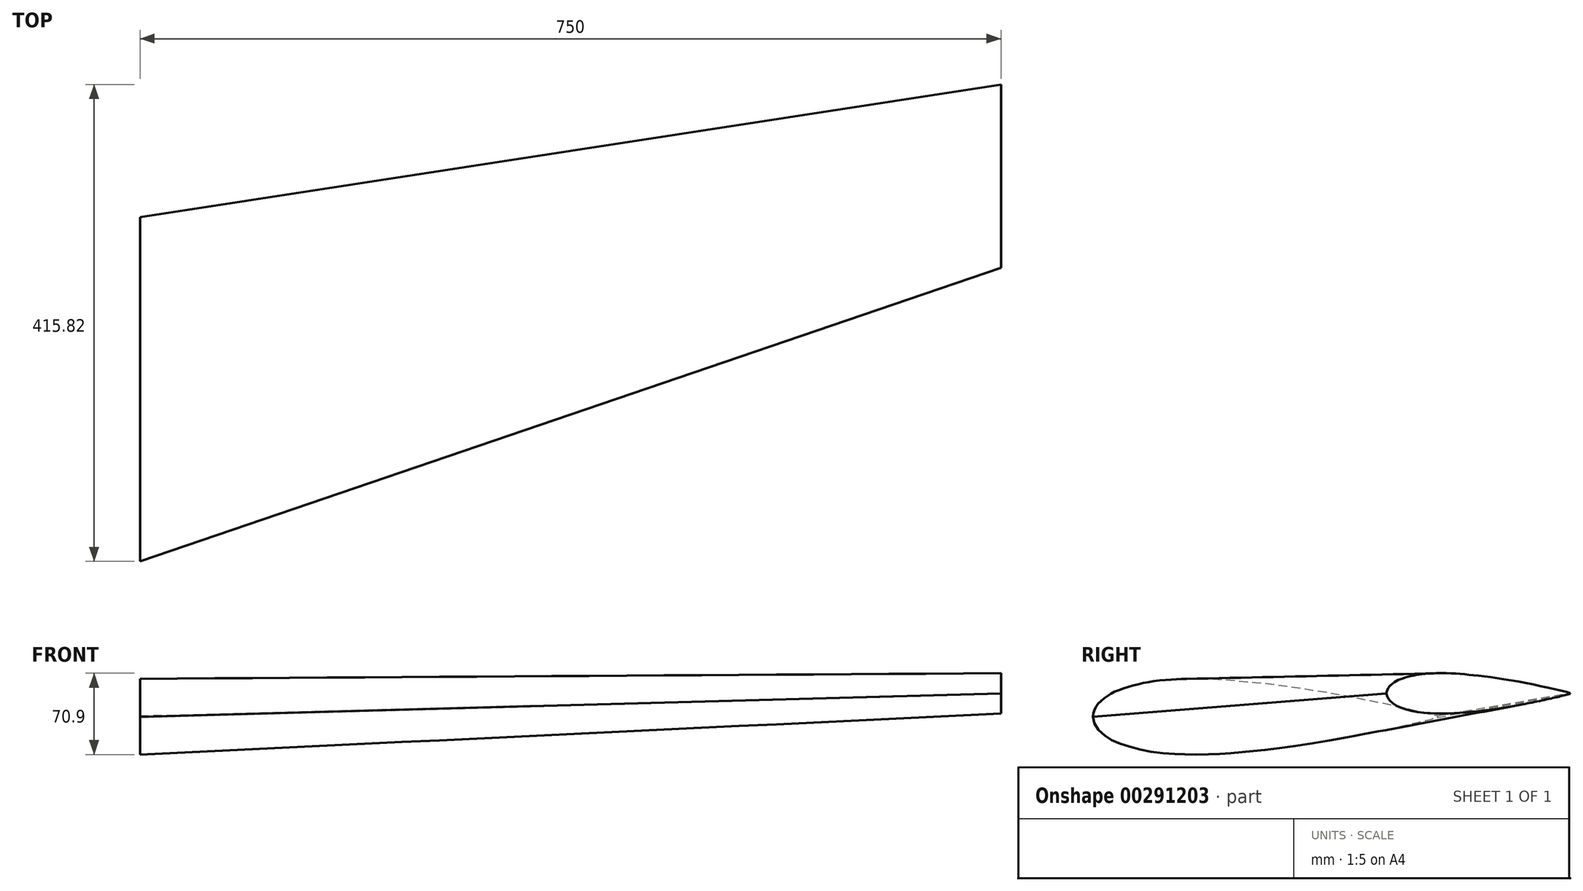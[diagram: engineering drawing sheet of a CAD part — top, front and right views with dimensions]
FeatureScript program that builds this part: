
annotation { "Feature Type Name" : "Feature", "Feature Type Description" : "" }
export const myFeature = defineFeature(function(context is Context, id is Id, definition is map)
    precondition{}
    {
        {
            var Q0;
            Q0=qCreatedBy(makeId("Right.planeOp"),FACE);
            var sketch = newSketch(context, id + "F0", { "sketchPlane" : qUnion([Q0])});
            skLineSegment(sketch, "E0", {"start": v(-150, 0) * mm, "end": v(-150, 0) * mm});
            skLineSegment(sketch, "E1", {"start": v(-150, 0) * mm, "end": v(-150, 0.01) * mm});
            skLineSegment(sketch, "E2", {"start": v(-150, 0.01) * mm, "end": v(-150, 0.02) * mm});
            skLineSegment(sketch, "E3", {"start": v(-150, 0.02) * mm, "end": v(-150, 0.04) * mm});
            skLineSegment(sketch, "E4", {"start": v(-150, 0.04) * mm, "end": v(-150, 0.05) * mm});
            skLineSegment(sketch, "E5", {"start": v(-150, 0.05) * mm, "end": v(-149.99, 0.08) * mm});
            skLineSegment(sketch, "E6", {"start": v(-149.99, 0.08) * mm, "end": v(-149.98, 0.1) * mm});
            skLineSegment(sketch, "E7", {"start": v(-149.98, 0.1) * mm, "end": v(-149.98, 0.14) * mm});
            skLineSegment(sketch, "E8", {"start": v(-149.98, 0.14) * mm, "end": v(-149.97, 0.18) * mm});
            skLineSegment(sketch, "E9", {"start": v(-149.97, 0.18) * mm, "end": v(-149.96, 0.23) * mm});
            skLineSegment(sketch, "E10", {"start": v(-149.96, 0.23) * mm, "end": v(-149.95, 0.29) * mm});
            skLineSegment(sketch, "E11", {"start": v(-149.95, 0.29) * mm, "end": v(-149.94, 0.35) * mm});
            skLineSegment(sketch, "E12", {"start": v(-149.94, 0.35) * mm, "end": v(-149.93, 0.43) * mm});
            skLineSegment(sketch, "E13", {"start": v(-149.93, 0.43) * mm, "end": v(-149.92, 0.51) * mm});
            skLineSegment(sketch, "E14", {"start": v(-149.92, 0.51) * mm, "end": v(-149.9, 0.6) * mm});
            skLineSegment(sketch, "E15", {"start": v(-149.9, 0.6) * mm, "end": v(-149.88, 0.72) * mm});
            skLineSegment(sketch, "E16", {"start": v(-149.88, 0.72) * mm, "end": v(-149.86, 0.84) * mm});
            skLineSegment(sketch, "E17", {"start": v(-149.86, 0.84) * mm, "end": v(-149.84, 0.97) * mm});
            skLineSegment(sketch, "E18", {"start": v(-149.84, 0.97) * mm, "end": v(-149.82, 1.11) * mm});
            skLineSegment(sketch, "E19", {"start": v(-149.82, 1.11) * mm, "end": v(-149.8, 1.27) * mm});
            skLineSegment(sketch, "E20", {"start": v(-149.8, 1.27) * mm, "end": v(-149.76, 1.43) * mm});
            skLineSegment(sketch, "E21", {"start": v(-149.76, 1.43) * mm, "end": v(-149.73, 1.6) * mm});
            skLineSegment(sketch, "E22", {"start": v(-149.73, 1.6) * mm, "end": v(-149.7, 1.79) * mm});
            skLineSegment(sketch, "E23", {"start": v(-149.7, 1.79) * mm, "end": v(-149.66, 1.98) * mm});
            skLineSegment(sketch, "E24", {"start": v(-149.66, 1.98) * mm, "end": v(-149.62, 2.18) * mm});
            skLineSegment(sketch, "E25", {"start": v(-149.62, 2.18) * mm, "end": v(-149.58, 2.4) * mm});
            skLineSegment(sketch, "E26", {"start": v(-149.58, 2.4) * mm, "end": v(-149.54, 2.6) * mm});
            skLineSegment(sketch, "E27", {"start": v(-149.54, 2.6) * mm, "end": v(-149.49, 2.83) * mm});
            skLineSegment(sketch, "E28", {"start": v(-149.49, 2.83) * mm, "end": v(-149.44, 3.05) * mm});
            skLineSegment(sketch, "E29", {"start": v(-149.44, 3.05) * mm, "end": v(-149.38, 3.28) * mm});
            skLineSegment(sketch, "E30", {"start": v(-149.38, 3.28) * mm, "end": v(-149.33, 3.52) * mm});
            skLineSegment(sketch, "E31", {"start": v(-149.33, 3.52) * mm, "end": v(-149.27, 3.76) * mm});
            skLineSegment(sketch, "E32", {"start": v(-149.27, 3.76) * mm, "end": v(-149.2, 4) * mm});
            skLineSegment(sketch, "E33", {"start": v(-149.2, 4) * mm, "end": v(-149.13, 4.24) * mm});
            skLineSegment(sketch, "E34", {"start": v(-149.13, 4.24) * mm, "end": v(-149.06, 4.48) * mm});
            skLineSegment(sketch, "E35", {"start": v(-149.06, 4.48) * mm, "end": v(-148.99, 4.73) * mm});
            skLineSegment(sketch, "E36", {"start": v(-148.99, 4.73) * mm, "end": v(-148.9, 4.97) * mm});
            skLineSegment(sketch, "E37", {"start": v(-148.9, 4.97) * mm, "end": v(-148.82, 5.22) * mm});
            skLineSegment(sketch, "E38", {"start": v(-148.82, 5.22) * mm, "end": v(-148.73, 5.46) * mm});
            skLineSegment(sketch, "E39", {"start": v(-148.73, 5.46) * mm, "end": v(-148.64, 5.7) * mm});
            skLineSegment(sketch, "E40", {"start": v(-148.64, 5.7) * mm, "end": v(-148.54, 5.95) * mm});
            skLineSegment(sketch, "E41", {"start": v(-148.54, 5.95) * mm, "end": v(-148.44, 6.19) * mm});
            skLineSegment(sketch, "E42", {"start": v(-148.44, 6.19) * mm, "end": v(-148.34, 6.43) * mm});
            skLineSegment(sketch, "E43", {"start": v(-148.34, 6.43) * mm, "end": v(-148.23, 6.67) * mm});
            skLineSegment(sketch, "E44", {"start": v(-148.23, 6.67) * mm, "end": v(-148.12, 6.9) * mm});
            skLineSegment(sketch, "E45", {"start": v(-148.12, 6.9) * mm, "end": v(-148, 7.15) * mm});
            skLineSegment(sketch, "E46", {"start": v(-148, 7.15) * mm, "end": v(-147.88, 7.38) * mm});
            skLineSegment(sketch, "E47", {"start": v(-147.88, 7.38) * mm, "end": v(-147.76, 7.62) * mm});
            skLineSegment(sketch, "E48", {"start": v(-147.76, 7.62) * mm, "end": v(-147.63, 7.86) * mm});
            skLineSegment(sketch, "E49", {"start": v(-147.63, 7.86) * mm, "end": v(-147.5, 8.1) * mm});
            skLineSegment(sketch, "E50", {"start": v(-147.5, 8.1) * mm, "end": v(-147.36, 8.33) * mm});
            skLineSegment(sketch, "E51", {"start": v(-147.36, 8.33) * mm, "end": v(-147.22, 8.57) * mm});
            skLineSegment(sketch, "E52", {"start": v(-147.22, 8.57) * mm, "end": v(-147.07, 8.8) * mm});
            skLineSegment(sketch, "E53", {"start": v(-147.07, 8.8) * mm, "end": v(-146.92, 9.03) * mm});
            skLineSegment(sketch, "E54", {"start": v(-146.92, 9.03) * mm, "end": v(-146.77, 9.27) * mm});
            skLineSegment(sketch, "E55", {"start": v(-146.77, 9.27) * mm, "end": v(-146.61, 9.5) * mm});
            skLineSegment(sketch, "E56", {"start": v(-146.61, 9.5) * mm, "end": v(-146.45, 9.73) * mm});
            skLineSegment(sketch, "E57", {"start": v(-146.45, 9.73) * mm, "end": v(-146.29, 9.96) * mm});
            skLineSegment(sketch, "E58", {"start": v(-146.29, 9.96) * mm, "end": v(-146.12, 10.19) * mm});
            skLineSegment(sketch, "E59", {"start": v(-146.12, 10.19) * mm, "end": v(-145.94, 10.42) * mm});
            skLineSegment(sketch, "E60", {"start": v(-145.94, 10.42) * mm, "end": v(-145.77, 10.65) * mm});
            skLineSegment(sketch, "E61", {"start": v(-145.77, 10.65) * mm, "end": v(-145.59, 10.87) * mm});
            skLineSegment(sketch, "E62", {"start": v(-145.59, 10.87) * mm, "end": v(-145.4, 11.1) * mm});
            skLineSegment(sketch, "E63", {"start": v(-145.4, 11.1) * mm, "end": v(-145.21, 11.33) * mm});
            skLineSegment(sketch, "E64", {"start": v(-145.21, 11.33) * mm, "end": v(-145.02, 11.55) * mm});
            skLineSegment(sketch, "E65", {"start": v(-145.02, 11.55) * mm, "end": v(-144.82, 11.77) * mm});
            skLineSegment(sketch, "E66", {"start": v(-144.82, 11.77) * mm, "end": v(-144.62, 12) * mm});
            skLineSegment(sketch, "E67", {"start": v(-144.62, 12) * mm, "end": v(-144.41, 12.22) * mm});
            skLineSegment(sketch, "E68", {"start": v(-144.41, 12.22) * mm, "end": v(-144.2, 12.44) * mm});
            skLineSegment(sketch, "E69", {"start": v(-144.2, 12.44) * mm, "end": v(-144, 12.66) * mm});
            skLineSegment(sketch, "E70", {"start": v(-144, 12.66) * mm, "end": v(-143.78, 12.88) * mm});
            skLineSegment(sketch, "E71", {"start": v(-143.78, 12.88) * mm, "end": v(-143.56, 13.1) * mm});
            skLineSegment(sketch, "E72", {"start": v(-143.56, 13.1) * mm, "end": v(-143.33, 13.32) * mm});
            skLineSegment(sketch, "E73", {"start": v(-143.33, 13.32) * mm, "end": v(-143.1, 13.54) * mm});
            skLineSegment(sketch, "E74", {"start": v(-143.1, 13.54) * mm, "end": v(-142.87, 13.76) * mm});
            skLineSegment(sketch, "E75", {"start": v(-142.87, 13.76) * mm, "end": v(-142.63, 13.97) * mm});
            skLineSegment(sketch, "E76", {"start": v(-142.63, 13.97) * mm, "end": v(-142.4, 14.19) * mm});
            skLineSegment(sketch, "E77", {"start": v(-142.4, 14.19) * mm, "end": v(-142.15, 14.4) * mm});
            skLineSegment(sketch, "E78", {"start": v(-142.15, 14.4) * mm, "end": v(-141.9, 14.62) * mm});
            skLineSegment(sketch, "E79", {"start": v(-141.9, 14.62) * mm, "end": v(-141.65, 14.83) * mm});
            skLineSegment(sketch, "E80", {"start": v(-141.65, 14.83) * mm, "end": v(-141.4, 15.04) * mm});
            skLineSegment(sketch, "E81", {"start": v(-141.4, 15.04) * mm, "end": v(-141.13, 15.25) * mm});
            skLineSegment(sketch, "E82", {"start": v(-141.13, 15.25) * mm, "end": v(-140.87, 15.46) * mm});
            skLineSegment(sketch, "E83", {"start": v(-140.87, 15.46) * mm, "end": v(-140.6, 15.67) * mm});
            skLineSegment(sketch, "E84", {"start": v(-140.6, 15.67) * mm, "end": v(-140.33, 15.88) * mm});
            skLineSegment(sketch, "E85", {"start": v(-140.33, 15.88) * mm, "end": v(-140.05, 16.09) * mm});
            skLineSegment(sketch, "E86", {"start": v(-140.05, 16.09) * mm, "end": v(-139.77, 16.3) * mm});
            skLineSegment(sketch, "E87", {"start": v(-139.77, 16.3) * mm, "end": v(-139.5, 16.5) * mm});
            skLineSegment(sketch, "E88", {"start": v(-139.5, 16.5) * mm, "end": v(-139.2, 16.7) * mm});
            skLineSegment(sketch, "E89", {"start": v(-139.2, 16.7) * mm, "end": v(-138.91, 16.9) * mm});
            skLineSegment(sketch, "E90", {"start": v(-138.91, 16.9) * mm, "end": v(-138.62, 17.1) * mm});
            skLineSegment(sketch, "E91", {"start": v(-138.62, 17.1) * mm, "end": v(-138.32, 17.3) * mm});
            skLineSegment(sketch, "E92", {"start": v(-138.32, 17.3) * mm, "end": v(-138.02, 17.51) * mm});
            skLineSegment(sketch, "E93", {"start": v(-138.02, 17.51) * mm, "end": v(-137.71, 17.7) * mm});
            skLineSegment(sketch, "E94", {"start": v(-137.71, 17.7) * mm, "end": v(-137.4, 17.9) * mm});
            skLineSegment(sketch, "E95", {"start": v(-137.4, 17.9) * mm, "end": v(-137.09, 18.1) * mm});
            skLineSegment(sketch, "E96", {"start": v(-137.09, 18.1) * mm, "end": v(-136.77, 18.3) * mm});
            skLineSegment(sketch, "E97", {"start": v(-136.77, 18.3) * mm, "end": v(-136.45, 18.5) * mm});
            skLineSegment(sketch, "E98", {"start": v(-136.45, 18.5) * mm, "end": v(-136.13, 18.7) * mm});
            skLineSegment(sketch, "E99", {"start": v(-136.13, 18.7) * mm, "end": v(-135.8, 18.89) * mm});
            skLineSegment(sketch, "E100", {"start": v(-135.8, 18.89) * mm, "end": v(-135.46, 19.08) * mm});
            skLineSegment(sketch, "E101", {"start": v(-135.46, 19.08) * mm, "end": v(-135.13, 19.27) * mm});
            skLineSegment(sketch, "E102", {"start": v(-135.13, 19.27) * mm, "end": v(-134.79, 19.46) * mm});
            skLineSegment(sketch, "E103", {"start": v(-134.79, 19.46) * mm, "end": v(-134.45, 19.65) * mm});
            skLineSegment(sketch, "E104", {"start": v(-134.45, 19.65) * mm, "end": v(-134.1, 19.84) * mm});
            skLineSegment(sketch, "E105", {"start": v(-134.1, 19.84) * mm, "end": v(-133.75, 20.02) * mm});
            skLineSegment(sketch, "E106", {"start": v(-133.75, 20.02) * mm, "end": v(-133.4, 20.21) * mm});
            skLineSegment(sketch, "E107", {"start": v(-133.4, 20.21) * mm, "end": v(-133.04, 20.4) * mm});
            skLineSegment(sketch, "E108", {"start": v(-133.04, 20.4) * mm, "end": v(-132.67, 20.58) * mm});
            skLineSegment(sketch, "E109", {"start": v(-132.67, 20.58) * mm, "end": v(-132.3, 20.76) * mm});
            skLineSegment(sketch, "E110", {"start": v(-132.3, 20.76) * mm, "end": v(-131.94, 20.94) * mm});
            skLineSegment(sketch, "E111", {"start": v(-131.94, 20.94) * mm, "end": v(-131.57, 21.12) * mm});
            skLineSegment(sketch, "E112", {"start": v(-131.57, 21.12) * mm, "end": v(-131.2, 21.3) * mm});
            skLineSegment(sketch, "E113", {"start": v(-131.2, 21.3) * mm, "end": v(-130.81, 21.48) * mm});
            skLineSegment(sketch, "E114", {"start": v(-130.81, 21.48) * mm, "end": v(-130.43, 21.66) * mm});
            skLineSegment(sketch, "E115", {"start": v(-130.43, 21.66) * mm, "end": v(-130.04, 21.83) * mm});
            skLineSegment(sketch, "E116", {"start": v(-130.04, 21.83) * mm, "end": v(-129.65, 22) * mm});
            skLineSegment(sketch, "E117", {"start": v(-129.65, 22) * mm, "end": v(-129.26, 22.18) * mm});
            skLineSegment(sketch, "E118", {"start": v(-129.26, 22.18) * mm, "end": v(-128.86, 22.35) * mm});
            skLineSegment(sketch, "E119", {"start": v(-128.86, 22.35) * mm, "end": v(-128.46, 22.53) * mm});
            skLineSegment(sketch, "E120", {"start": v(-128.46, 22.53) * mm, "end": v(-128.05, 22.7) * mm});
            skLineSegment(sketch, "E121", {"start": v(-128.05, 22.7) * mm, "end": v(-127.64, 22.86) * mm});
            skLineSegment(sketch, "E122", {"start": v(-127.64, 22.86) * mm, "end": v(-127.23, 23.03) * mm});
            skLineSegment(sketch, "E123", {"start": v(-127.23, 23.03) * mm, "end": v(-126.82, 23.2) * mm});
            skLineSegment(sketch, "E124", {"start": v(-126.82, 23.2) * mm, "end": v(-126.4, 23.36) * mm});
            skLineSegment(sketch, "E125", {"start": v(-126.4, 23.36) * mm, "end": v(-125.98, 23.53) * mm});
            skLineSegment(sketch, "E126", {"start": v(-125.98, 23.53) * mm, "end": v(-125.55, 23.69) * mm});
            skLineSegment(sketch, "E127", {"start": v(-125.55, 23.69) * mm, "end": v(-125.12, 23.85) * mm});
            skLineSegment(sketch, "E128", {"start": v(-125.12, 23.85) * mm, "end": v(-124.7, 24.01) * mm});
            skLineSegment(sketch, "E129", {"start": v(-124.7, 24.01) * mm, "end": v(-124.25, 24.17) * mm});
            skLineSegment(sketch, "E130", {"start": v(-124.25, 24.17) * mm, "end": v(-123.82, 24.33) * mm});
            skLineSegment(sketch, "E131", {"start": v(-123.82, 24.33) * mm, "end": v(-123.37, 24.48) * mm});
            skLineSegment(sketch, "E132", {"start": v(-123.37, 24.48) * mm, "end": v(-122.93, 24.64) * mm});
            skLineSegment(sketch, "E133", {"start": v(-122.93, 24.64) * mm, "end": v(-122.48, 24.8) * mm});
            skLineSegment(sketch, "E134", {"start": v(-122.48, 24.8) * mm, "end": v(-122.02, 24.95) * mm});
            skLineSegment(sketch, "E135", {"start": v(-122.02, 24.95) * mm, "end": v(-121.57, 25.1) * mm});
            skLineSegment(sketch, "E136", {"start": v(-121.57, 25.1) * mm, "end": v(-121.1, 25.25) * mm});
            skLineSegment(sketch, "E137", {"start": v(-121.1, 25.25) * mm, "end": v(-120.65, 25.4) * mm});
            skLineSegment(sketch, "E138", {"start": v(-120.65, 25.4) * mm, "end": v(-120.18, 25.54) * mm});
            skLineSegment(sketch, "E139", {"start": v(-120.18, 25.54) * mm, "end": v(-119.71, 25.69) * mm});
            skLineSegment(sketch, "E140", {"start": v(-119.71, 25.69) * mm, "end": v(-119.24, 25.83) * mm});
            skLineSegment(sketch, "E141", {"start": v(-119.24, 25.83) * mm, "end": v(-118.76, 25.98) * mm});
            skLineSegment(sketch, "E142", {"start": v(-118.76, 25.98) * mm, "end": v(-118.28, 26.12) * mm});
            skLineSegment(sketch, "E143", {"start": v(-118.28, 26.12) * mm, "end": v(-117.8, 26.26) * mm});
            skLineSegment(sketch, "E144", {"start": v(-117.8, 26.26) * mm, "end": v(-117.31, 26.4) * mm});
            skLineSegment(sketch, "E145", {"start": v(-117.31, 26.4) * mm, "end": v(-116.83, 26.53) * mm});
            skLineSegment(sketch, "E146", {"start": v(-116.83, 26.53) * mm, "end": v(-116.33, 26.67) * mm});
            skLineSegment(sketch, "E147", {"start": v(-116.33, 26.67) * mm, "end": v(-115.84, 26.8) * mm});
            skLineSegment(sketch, "E148", {"start": v(-115.84, 26.8) * mm, "end": v(-115.34, 26.94) * mm});
            skLineSegment(sketch, "E149", {"start": v(-115.34, 26.94) * mm, "end": v(-114.84, 27.07) * mm});
            skLineSegment(sketch, "E150", {"start": v(-114.84, 27.07) * mm, "end": v(-114.33, 27.2) * mm});
            skLineSegment(sketch, "E151", {"start": v(-114.33, 27.2) * mm, "end": v(-113.82, 27.33) * mm});
            skLineSegment(sketch, "E152", {"start": v(-113.82, 27.33) * mm, "end": v(-113.31, 27.46) * mm});
            skLineSegment(sketch, "E153", {"start": v(-113.31, 27.46) * mm, "end": v(-112.8, 27.59) * mm});
            skLineSegment(sketch, "E154", {"start": v(-112.8, 27.59) * mm, "end": v(-112.28, 27.71) * mm});
            skLineSegment(sketch, "E155", {"start": v(-112.28, 27.71) * mm, "end": v(-111.76, 27.84) * mm});
            skLineSegment(sketch, "E156", {"start": v(-111.76, 27.84) * mm, "end": v(-111.24, 27.96) * mm});
            skLineSegment(sketch, "E157", {"start": v(-111.24, 27.96) * mm, "end": v(-110.71, 28.08) * mm});
            skLineSegment(sketch, "E158", {"start": v(-110.71, 28.08) * mm, "end": v(-110.18, 28.2) * mm});
            skLineSegment(sketch, "E159", {"start": v(-110.18, 28.2) * mm, "end": v(-109.65, 28.32) * mm});
            skLineSegment(sketch, "E160", {"start": v(-109.65, 28.32) * mm, "end": v(-109.11, 28.43) * mm});
            skLineSegment(sketch, "E161", {"start": v(-109.11, 28.43) * mm, "end": v(-108.58, 28.55) * mm});
            skLineSegment(sketch, "E162", {"start": v(-108.58, 28.55) * mm, "end": v(-108.03, 28.66) * mm});
            skLineSegment(sketch, "E163", {"start": v(-108.03, 28.66) * mm, "end": v(-107.49, 28.78) * mm});
            skLineSegment(sketch, "E164", {"start": v(-107.49, 28.78) * mm, "end": v(-106.94, 28.89) * mm});
            skLineSegment(sketch, "E165", {"start": v(-106.94, 28.89) * mm, "end": v(-106.4, 29) * mm});
            skLineSegment(sketch, "E166", {"start": v(-106.4, 29) * mm, "end": v(-105.84, 29.1) * mm});
            skLineSegment(sketch, "E167", {"start": v(-105.84, 29.1) * mm, "end": v(-105.28, 29.21) * mm});
            skLineSegment(sketch, "E168", {"start": v(-105.28, 29.21) * mm, "end": v(-104.72, 29.32) * mm});
            skLineSegment(sketch, "E169", {"start": v(-104.72, 29.32) * mm, "end": v(-104.16, 29.42) * mm});
            skLineSegment(sketch, "E170", {"start": v(-104.16, 29.42) * mm, "end": v(-103.6, 29.52) * mm});
            skLineSegment(sketch, "E171", {"start": v(-103.6, 29.52) * mm, "end": v(-103.03, 29.62) * mm});
            skLineSegment(sketch, "E172", {"start": v(-103.03, 29.62) * mm, "end": v(-102.46, 29.72) * mm});
            skLineSegment(sketch, "E173", {"start": v(-102.46, 29.72) * mm, "end": v(-101.89, 29.82) * mm});
            skLineSegment(sketch, "E174", {"start": v(-101.89, 29.82) * mm, "end": v(-101.3, 29.91) * mm});
            skLineSegment(sketch, "E175", {"start": v(-101.3, 29.91) * mm, "end": v(-100.73, 30) * mm});
            skLineSegment(sketch, "E176", {"start": v(-100.73, 30) * mm, "end": v(-100.15, 30.1) * mm});
            skLineSegment(sketch, "E177", {"start": v(-100.15, 30.1) * mm, "end": v(-99.56, 30.2) * mm});
            skLineSegment(sketch, "E178", {"start": v(-99.56, 30.2) * mm, "end": v(-98.98, 30.28) * mm});
            skLineSegment(sketch, "E179", {"start": v(-98.98, 30.28) * mm, "end": v(-98.39, 30.37) * mm});
            skLineSegment(sketch, "E180", {"start": v(-98.39, 30.37) * mm, "end": v(-97.8, 30.46) * mm});
            skLineSegment(sketch, "E181", {"start": v(-97.8, 30.46) * mm, "end": v(-97.2, 30.54) * mm});
            skLineSegment(sketch, "E182", {"start": v(-97.2, 30.54) * mm, "end": v(-96.6, 30.63) * mm});
            skLineSegment(sketch, "E183", {"start": v(-96.6, 30.63) * mm, "end": v(-96, 30.71) * mm});
            skLineSegment(sketch, "E184", {"start": v(-96, 30.71) * mm, "end": v(-95.4, 30.8) * mm});
            skLineSegment(sketch, "E185", {"start": v(-95.4, 30.8) * mm, "end": v(-94.8, 30.87) * mm});
            skLineSegment(sketch, "E186", {"start": v(-94.8, 30.87) * mm, "end": v(-94.18, 30.95) * mm});
            skLineSegment(sketch, "E187", {"start": v(-94.18, 30.95) * mm, "end": v(-93.57, 31.03) * mm});
            skLineSegment(sketch, "E188", {"start": v(-93.57, 31.03) * mm, "end": v(-92.96, 31.1) * mm});
            skLineSegment(sketch, "E189", {"start": v(-92.96, 31.1) * mm, "end": v(-92.34, 31.17) * mm});
            skLineSegment(sketch, "E190", {"start": v(-92.34, 31.17) * mm, "end": v(-91.72, 31.25) * mm});
            skLineSegment(sketch, "E191", {"start": v(-91.72, 31.25) * mm, "end": v(-91.1, 31.32) * mm});
            skLineSegment(sketch, "E192", {"start": v(-91.1, 31.32) * mm, "end": v(-90.48, 31.39) * mm});
            skLineSegment(sketch, "E193", {"start": v(-90.48, 31.39) * mm, "end": v(-89.85, 31.45) * mm});
            skLineSegment(sketch, "E194", {"start": v(-89.85, 31.45) * mm, "end": v(-89.23, 31.52) * mm});
            skLineSegment(sketch, "E195", {"start": v(-89.23, 31.52) * mm, "end": v(-88.6, 31.58) * mm});
            skLineSegment(sketch, "E196", {"start": v(-88.6, 31.58) * mm, "end": v(-87.96, 31.65) * mm});
            skLineSegment(sketch, "E197", {"start": v(-87.96, 31.65) * mm, "end": v(-87.32, 31.7) * mm});
            skLineSegment(sketch, "E198", {"start": v(-87.32, 31.7) * mm, "end": v(-86.69, 31.77) * mm});
            skLineSegment(sketch, "E199", {"start": v(-86.69, 31.77) * mm, "end": v(-86.05, 31.82) * mm});
            skLineSegment(sketch, "E200", {"start": v(-86.05, 31.82) * mm, "end": v(-85.4, 31.88) * mm});
            skLineSegment(sketch, "E201", {"start": v(-85.4, 31.88) * mm, "end": v(-84.76, 31.94) * mm});
            skLineSegment(sketch, "E202", {"start": v(-84.76, 31.94) * mm, "end": v(-84.1, 31.99) * mm});
            skLineSegment(sketch, "E203", {"start": v(-84.1, 31.99) * mm, "end": v(-83.46, 32.04) * mm});
            skLineSegment(sketch, "E204", {"start": v(-83.46, 32.04) * mm, "end": v(-82.8, 32.1) * mm});
            skLineSegment(sketch, "E205", {"start": v(-82.8, 32.1) * mm, "end": v(-82.15, 32.14) * mm});
            skLineSegment(sketch, "E206", {"start": v(-82.15, 32.14) * mm, "end": v(-81.5, 32.19) * mm});
            skLineSegment(sketch, "E207", {"start": v(-81.5, 32.19) * mm, "end": v(-80.84, 32.23) * mm});
            skLineSegment(sketch, "E208", {"start": v(-80.84, 32.23) * mm, "end": v(-80.18, 32.28) * mm});
            skLineSegment(sketch, "E209", {"start": v(-80.18, 32.28) * mm, "end": v(-79.51, 32.32) * mm});
            skLineSegment(sketch, "E210", {"start": v(-79.51, 32.32) * mm, "end": v(-78.85, 32.36) * mm});
            skLineSegment(sketch, "E211", {"start": v(-78.85, 32.36) * mm, "end": v(-78.18, 32.4) * mm});
            skLineSegment(sketch, "E212", {"start": v(-78.18, 32.4) * mm, "end": v(-77.5, 32.44) * mm});
            skLineSegment(sketch, "E213", {"start": v(-77.5, 32.44) * mm, "end": v(-76.84, 32.48) * mm});
            skLineSegment(sketch, "E214", {"start": v(-76.84, 32.48) * mm, "end": v(-76.16, 32.51) * mm});
            skLineSegment(sketch, "E215", {"start": v(-76.16, 32.51) * mm, "end": v(-75.49, 32.55) * mm});
            skLineSegment(sketch, "E216", {"start": v(-75.49, 32.55) * mm, "end": v(-74.8, 32.58) * mm});
            skLineSegment(sketch, "E217", {"start": v(-74.8, 32.58) * mm, "end": v(-74.13, 32.6) * mm});
            skLineSegment(sketch, "E218", {"start": v(-74.13, 32.6) * mm, "end": v(-73.45, 32.64) * mm});
            skLineSegment(sketch, "E219", {"start": v(-73.45, 32.64) * mm, "end": v(-72.76, 32.67) * mm});
            skLineSegment(sketch, "E220", {"start": v(-72.76, 32.67) * mm, "end": v(-72.07, 32.7) * mm});
            skLineSegment(sketch, "E221", {"start": v(-72.07, 32.7) * mm, "end": v(-71.39, 32.72) * mm});
            skLineSegment(sketch, "E222", {"start": v(-71.39, 32.72) * mm, "end": v(-70.7, 32.74) * mm});
            skLineSegment(sketch, "E223", {"start": v(-70.7, 32.74) * mm, "end": v(-70, 32.76) * mm});
            skLineSegment(sketch, "E224", {"start": v(-70, 32.76) * mm, "end": v(-69.3, 32.78) * mm});
            skLineSegment(sketch, "E225", {"start": v(-69.3, 32.78) * mm, "end": v(-68.61, 32.8) * mm});
            skLineSegment(sketch, "E226", {"start": v(-68.61, 32.8) * mm, "end": v(-67.92, 32.82) * mm});
            skLineSegment(sketch, "E227", {"start": v(-67.92, 32.82) * mm, "end": v(-67.22, 32.84) * mm});
            skLineSegment(sketch, "E228", {"start": v(-67.22, 32.84) * mm, "end": v(-66.51, 32.85) * mm});
            skLineSegment(sketch, "E229", {"start": v(-66.51, 32.85) * mm, "end": v(-65.8, 32.86) * mm});
            skLineSegment(sketch, "E230", {"start": v(-65.8, 32.86) * mm, "end": v(-65.1, 32.87) * mm});
            skLineSegment(sketch, "E231", {"start": v(-65.1, 32.87) * mm, "end": v(-64.4, 32.88) * mm});
            skLineSegment(sketch, "E232", {"start": v(-64.4, 32.88) * mm, "end": v(-63.69, 32.9) * mm});
            skLineSegment(sketch, "E233", {"start": v(-63.69, 32.9) * mm, "end": v(-62.98, 32.9) * mm});
            skLineSegment(sketch, "E234", {"start": v(-62.98, 32.9) * mm, "end": v(-62.27, 32.9) * mm});
            skLineSegment(sketch, "E235", {"start": v(-62.27, 32.9) * mm, "end": v(-61.55, 32.9) * mm});
            skLineSegment(sketch, "E236", {"start": v(-61.55, 32.9) * mm, "end": v(-60.84, 32.91) * mm});
            skLineSegment(sketch, "E237", {"start": v(-60.84, 32.91) * mm, "end": v(-60.12, 32.91) * mm});
            skLineSegment(sketch, "E238", {"start": v(-60.12, 32.91) * mm, "end": v(-59.4, 32.91) * mm});
            skLineSegment(sketch, "E239", {"start": v(-59.4, 32.91) * mm, "end": v(-58.68, 32.91) * mm});
            skLineSegment(sketch, "E240", {"start": v(-58.68, 32.91) * mm, "end": v(-57.96, 32.9) * mm});
            skLineSegment(sketch, "E241", {"start": v(-57.96, 32.9) * mm, "end": v(-57.23, 32.9) * mm});
            skLineSegment(sketch, "E242", {"start": v(-57.23, 32.9) * mm, "end": v(-56.5, 32.9) * mm});
            skLineSegment(sketch, "E243", {"start": v(-56.5, 32.9) * mm, "end": v(-55.78, 32.9) * mm});
            skLineSegment(sketch, "E244", {"start": v(-55.78, 32.9) * mm, "end": v(-55.05, 32.88) * mm});
            skLineSegment(sketch, "E245", {"start": v(-55.05, 32.88) * mm, "end": v(-54.32, 32.87) * mm});
            skLineSegment(sketch, "E246", {"start": v(-54.32, 32.87) * mm, "end": v(-53.59, 32.86) * mm});
            skLineSegment(sketch, "E247", {"start": v(-53.59, 32.86) * mm, "end": v(-52.86, 32.85) * mm});
            skLineSegment(sketch, "E248", {"start": v(-52.86, 32.85) * mm, "end": v(-52.12, 32.84) * mm});
            skLineSegment(sketch, "E249", {"start": v(-52.12, 32.84) * mm, "end": v(-51.39, 32.82) * mm});
            skLineSegment(sketch, "E250", {"start": v(-51.39, 32.82) * mm, "end": v(-50.65, 32.8) * mm});
            skLineSegment(sketch, "E251", {"start": v(-50.65, 32.8) * mm, "end": v(-49.9, 32.79) * mm});
            skLineSegment(sketch, "E252", {"start": v(-49.9, 32.79) * mm, "end": v(-49.17, 32.77) * mm});
            skLineSegment(sketch, "E253", {"start": v(-49.17, 32.77) * mm, "end": v(-48.43, 32.75) * mm});
            skLineSegment(sketch, "E254", {"start": v(-48.43, 32.75) * mm, "end": v(-47.69, 32.72) * mm});
            skLineSegment(sketch, "E255", {"start": v(-47.69, 32.72) * mm, "end": v(-46.94, 32.7) * mm});
            skLineSegment(sketch, "E256", {"start": v(-46.94, 32.7) * mm, "end": v(-46.2, 32.68) * mm});
            skLineSegment(sketch, "E257", {"start": v(-46.2, 32.68) * mm, "end": v(-45.45, 32.65) * mm});
            skLineSegment(sketch, "E258", {"start": v(-45.45, 32.65) * mm, "end": v(-44.7, 32.62) * mm});
            skLineSegment(sketch, "E259", {"start": v(-44.7, 32.62) * mm, "end": v(-43.95, 32.6) * mm});
            skLineSegment(sketch, "E260", {"start": v(-43.95, 32.6) * mm, "end": v(-43.2, 32.56) * mm});
            skLineSegment(sketch, "E261", {"start": v(-43.2, 32.56) * mm, "end": v(-42.45, 32.53) * mm});
            skLineSegment(sketch, "E262", {"start": v(-42.45, 32.53) * mm, "end": v(-41.7, 32.5) * mm});
            skLineSegment(sketch, "E263", {"start": v(-41.7, 32.5) * mm, "end": v(-40.94, 32.47) * mm});
            skLineSegment(sketch, "E264", {"start": v(-40.94, 32.47) * mm, "end": v(-40.19, 32.43) * mm});
            skLineSegment(sketch, "E265", {"start": v(-40.19, 32.43) * mm, "end": v(-39.43, 32.4) * mm});
            skLineSegment(sketch, "E266", {"start": v(-39.43, 32.4) * mm, "end": v(-38.68, 32.36) * mm});
            skLineSegment(sketch, "E267", {"start": v(-38.68, 32.36) * mm, "end": v(-37.92, 32.32) * mm});
            skLineSegment(sketch, "E268", {"start": v(-37.92, 32.32) * mm, "end": v(-37.16, 32.28) * mm});
            skLineSegment(sketch, "E269", {"start": v(-37.16, 32.28) * mm, "end": v(-36.4, 32.24) * mm});
            skLineSegment(sketch, "E270", {"start": v(-36.4, 32.24) * mm, "end": v(-35.64, 32.2) * mm});
            skLineSegment(sketch, "E271", {"start": v(-35.64, 32.2) * mm, "end": v(-34.87, 32.15) * mm});
            skLineSegment(sketch, "E272", {"start": v(-34.87, 32.15) * mm, "end": v(-34.11, 32.1) * mm});
            skLineSegment(sketch, "E273", {"start": v(-34.11, 32.1) * mm, "end": v(-33.35, 32.06) * mm});
            skLineSegment(sketch, "E274", {"start": v(-33.35, 32.06) * mm, "end": v(-32.58, 32.01) * mm});
            skLineSegment(sketch, "E275", {"start": v(-32.58, 32.01) * mm, "end": v(-31.82, 31.96) * mm});
            skLineSegment(sketch, "E276", {"start": v(-31.82, 31.96) * mm, "end": v(-31.05, 31.91) * mm});
            skLineSegment(sketch, "E277", {"start": v(-31.05, 31.91) * mm, "end": v(-30.28, 31.86) * mm});
            skLineSegment(sketch, "E278", {"start": v(-30.28, 31.86) * mm, "end": v(-29.51, 31.8) * mm});
            skLineSegment(sketch, "E279", {"start": v(-29.51, 31.8) * mm, "end": v(-28.74, 31.76) * mm});
            skLineSegment(sketch, "E280", {"start": v(-28.74, 31.76) * mm, "end": v(-27.97, 31.7) * mm});
            skLineSegment(sketch, "E281", {"start": v(-27.97, 31.7) * mm, "end": v(-27.2, 31.65) * mm});
            skLineSegment(sketch, "E282", {"start": v(-27.2, 31.65) * mm, "end": v(-26.43, 31.59) * mm});
            skLineSegment(sketch, "E283", {"start": v(-26.43, 31.59) * mm, "end": v(-25.66, 31.53) * mm});
            skLineSegment(sketch, "E284", {"start": v(-25.66, 31.53) * mm, "end": v(-24.89, 31.47) * mm});
            skLineSegment(sketch, "E285", {"start": v(-24.89, 31.47) * mm, "end": v(-24.11, 31.41) * mm});
            skLineSegment(sketch, "E286", {"start": v(-24.11, 31.41) * mm, "end": v(-23.34, 31.35) * mm});
            skLineSegment(sketch, "E287", {"start": v(-23.34, 31.35) * mm, "end": v(-22.56, 31.29) * mm});
            skLineSegment(sketch, "E288", {"start": v(-22.56, 31.29) * mm, "end": v(-21.79, 31.23) * mm});
            skLineSegment(sketch, "E289", {"start": v(-21.79, 31.23) * mm, "end": v(-21.01, 31.16) * mm});
            skLineSegment(sketch, "E290", {"start": v(-21.01, 31.16) * mm, "end": v(-20.23, 31.1) * mm});
            skLineSegment(sketch, "E291", {"start": v(-20.23, 31.1) * mm, "end": v(-19.46, 31.03) * mm});
            skLineSegment(sketch, "E292", {"start": v(-19.46, 31.03) * mm, "end": v(-18.68, 30.96) * mm});
            skLineSegment(sketch, "E293", {"start": v(-18.68, 30.96) * mm, "end": v(-17.9, 30.9) * mm});
            skLineSegment(sketch, "E294", {"start": v(-17.9, 30.9) * mm, "end": v(-17.12, 30.82) * mm});
            skLineSegment(sketch, "E295", {"start": v(-17.12, 30.82) * mm, "end": v(-16.34, 30.75) * mm});
            skLineSegment(sketch, "E296", {"start": v(-16.34, 30.75) * mm, "end": v(-15.56, 30.68) * mm});
            skLineSegment(sketch, "E297", {"start": v(-15.56, 30.68) * mm, "end": v(-14.78, 30.6) * mm});
            skLineSegment(sketch, "E298", {"start": v(-14.78, 30.6) * mm, "end": v(-14, 30.54) * mm});
            skLineSegment(sketch, "E299", {"start": v(-14, 30.54) * mm, "end": v(-13.22, 30.46) * mm});
            skLineSegment(sketch, "E300", {"start": v(-13.22, 30.46) * mm, "end": v(-12.44, 30.39) * mm});
            skLineSegment(sketch, "E301", {"start": v(-12.44, 30.39) * mm, "end": v(-11.66, 30.3) * mm});
            skLineSegment(sketch, "E302", {"start": v(-11.66, 30.3) * mm, "end": v(-10.88, 30.23) * mm});
            skLineSegment(sketch, "E303", {"start": v(-10.88, 30.23) * mm, "end": v(-10.1, 30.15) * mm});
            skLineSegment(sketch, "E304", {"start": v(-10.1, 30.15) * mm, "end": v(-9.31, 30.07) * mm});
            skLineSegment(sketch, "E305", {"start": v(-9.31, 30.07) * mm, "end": v(-8.53, 30) * mm});
            skLineSegment(sketch, "E306", {"start": v(-8.53, 30) * mm, "end": v(-7.74, 29.91) * mm});
            skLineSegment(sketch, "E307", {"start": v(-7.74, 29.91) * mm, "end": v(-6.96, 29.83) * mm});
            skLineSegment(sketch, "E308", {"start": v(-6.96, 29.83) * mm, "end": v(-6.18, 29.75) * mm});
            skLineSegment(sketch, "E309", {"start": v(-6.18, 29.75) * mm, "end": v(-5.4, 29.66) * mm});
            skLineSegment(sketch, "E310", {"start": v(-5.4, 29.66) * mm, "end": v(-4.61, 29.58) * mm});
            skLineSegment(sketch, "E311", {"start": v(-4.61, 29.58) * mm, "end": v(-3.83, 29.5) * mm});
            skLineSegment(sketch, "E312", {"start": v(-3.83, 29.5) * mm, "end": v(-3.04, 29.4) * mm});
            skLineSegment(sketch, "E313", {"start": v(-3.04, 29.4) * mm, "end": v(-2.26, 29.32) * mm});
            skLineSegment(sketch, "E314", {"start": v(-2.26, 29.32) * mm, "end": v(-1.47, 29.23) * mm});
            skLineSegment(sketch, "E315", {"start": v(-1.47, 29.23) * mm, "end": v(-0.69, 29.14) * mm});
            skLineSegment(sketch, "E316", {"start": v(-0.69, 29.14) * mm, "end": v(0.1, 29.05) * mm});
            skLineSegment(sketch, "E317", {"start": v(0.1, 29.05) * mm, "end": v(0.88, 28.96) * mm});
            skLineSegment(sketch, "E318", {"start": v(0.88, 28.96) * mm, "end": v(1.66, 28.87) * mm});
            skLineSegment(sketch, "E319", {"start": v(1.66, 28.87) * mm, "end": v(2.45, 28.78) * mm});
            skLineSegment(sketch, "E320", {"start": v(2.45, 28.78) * mm, "end": v(3.23, 28.68) * mm});
            skLineSegment(sketch, "E321", {"start": v(3.23, 28.68) * mm, "end": v(4.02, 28.59) * mm});
            skLineSegment(sketch, "E322", {"start": v(4.02, 28.59) * mm, "end": v(4.8, 28.5) * mm});
            skLineSegment(sketch, "E323", {"start": v(4.8, 28.5) * mm, "end": v(5.58, 28.4) * mm});
            skLineSegment(sketch, "E324", {"start": v(5.58, 28.4) * mm, "end": v(6.37, 28.3) * mm});
            skLineSegment(sketch, "E325", {"start": v(6.37, 28.3) * mm, "end": v(7.15, 28.2) * mm});
            skLineSegment(sketch, "E326", {"start": v(7.15, 28.2) * mm, "end": v(7.93, 28.1) * mm});
            skLineSegment(sketch, "E327", {"start": v(7.93, 28.1) * mm, "end": v(8.72, 28) * mm});
            skLineSegment(sketch, "E328", {"start": v(8.72, 28) * mm, "end": v(9.5, 27.9) * mm});
            skLineSegment(sketch, "E329", {"start": v(9.5, 27.9) * mm, "end": v(10.28, 27.8) * mm});
            skLineSegment(sketch, "E330", {"start": v(10.28, 27.8) * mm, "end": v(11.06, 27.7) * mm});
            skLineSegment(sketch, "E331", {"start": v(11.06, 27.7) * mm, "end": v(11.85, 27.6) * mm});
            skLineSegment(sketch, "E332", {"start": v(11.85, 27.6) * mm, "end": v(12.63, 27.5) * mm});
            skLineSegment(sketch, "E333", {"start": v(12.63, 27.5) * mm, "end": v(13.4, 27.4) * mm});
            skLineSegment(sketch, "E334", {"start": v(13.4, 27.4) * mm, "end": v(14.2, 27.3) * mm});
            skLineSegment(sketch, "E335", {"start": v(14.2, 27.3) * mm, "end": v(14.97, 27.2) * mm});
            skLineSegment(sketch, "E336", {"start": v(14.97, 27.2) * mm, "end": v(15.75, 27.1) * mm});
            skLineSegment(sketch, "E337", {"start": v(15.75, 27.1) * mm, "end": v(16.53, 26.98) * mm});
            skLineSegment(sketch, "E338", {"start": v(16.53, 26.98) * mm, "end": v(17.31, 26.88) * mm});
            skLineSegment(sketch, "E339", {"start": v(17.31, 26.88) * mm, "end": v(18.09, 26.77) * mm});
            skLineSegment(sketch, "E340", {"start": v(18.09, 26.77) * mm, "end": v(18.87, 26.66) * mm});
            skLineSegment(sketch, "E341", {"start": v(18.87, 26.66) * mm, "end": v(19.64, 26.56) * mm});
            skLineSegment(sketch, "E342", {"start": v(19.64, 26.56) * mm, "end": v(20.42, 26.45) * mm});
            skLineSegment(sketch, "E343", {"start": v(20.42, 26.45) * mm, "end": v(21.2, 26.34) * mm});
            skLineSegment(sketch, "E344", {"start": v(21.2, 26.34) * mm, "end": v(21.97, 26.23) * mm});
            skLineSegment(sketch, "E345", {"start": v(21.97, 26.23) * mm, "end": v(22.75, 26.12) * mm});
            skLineSegment(sketch, "E346", {"start": v(22.75, 26.12) * mm, "end": v(23.53, 26) * mm});
            skLineSegment(sketch, "E347", {"start": v(23.53, 26) * mm, "end": v(24.3, 25.9) * mm});
            skLineSegment(sketch, "E348", {"start": v(24.3, 25.9) * mm, "end": v(25.07, 25.79) * mm});
            skLineSegment(sketch, "E349", {"start": v(25.07, 25.79) * mm, "end": v(25.85, 25.67) * mm});
            skLineSegment(sketch, "E350", {"start": v(25.85, 25.67) * mm, "end": v(26.62, 25.56) * mm});
            skLineSegment(sketch, "E351", {"start": v(26.62, 25.56) * mm, "end": v(27.39, 25.45) * mm});
            skLineSegment(sketch, "E352", {"start": v(27.39, 25.45) * mm, "end": v(28.16, 25.33) * mm});
            skLineSegment(sketch, "E353", {"start": v(28.16, 25.33) * mm, "end": v(28.93, 25.22) * mm});
            skLineSegment(sketch, "E354", {"start": v(28.93, 25.22) * mm, "end": v(29.7, 25.1) * mm});
            skLineSegment(sketch, "E355", {"start": v(29.7, 25.1) * mm, "end": v(30.47, 24.99) * mm});
            skLineSegment(sketch, "E356", {"start": v(30.47, 24.99) * mm, "end": v(31.23, 24.87) * mm});
            skLineSegment(sketch, "E357", {"start": v(31.23, 24.87) * mm, "end": v(32, 24.76) * mm});
            skLineSegment(sketch, "E358", {"start": v(32, 24.76) * mm, "end": v(32.77, 24.64) * mm});
            skLineSegment(sketch, "E359", {"start": v(32.77, 24.64) * mm, "end": v(33.53, 24.52) * mm});
            skLineSegment(sketch, "E360", {"start": v(33.53, 24.52) * mm, "end": v(34.3, 24.4) * mm});
            skLineSegment(sketch, "E361", {"start": v(34.3, 24.4) * mm, "end": v(35.06, 24.29) * mm});
            skLineSegment(sketch, "E362", {"start": v(35.06, 24.29) * mm, "end": v(35.82, 24.17) * mm});
            skLineSegment(sketch, "E363", {"start": v(35.82, 24.17) * mm, "end": v(36.58, 24.05) * mm});
            skLineSegment(sketch, "E364", {"start": v(36.58, 24.05) * mm, "end": v(37.34, 23.93) * mm});
            skLineSegment(sketch, "E365", {"start": v(37.34, 23.93) * mm, "end": v(38.1, 23.8) * mm});
            skLineSegment(sketch, "E366", {"start": v(38.1, 23.8) * mm, "end": v(38.86, 23.69) * mm});
            skLineSegment(sketch, "E367", {"start": v(38.86, 23.69) * mm, "end": v(39.62, 23.57) * mm});
            skLineSegment(sketch, "E368", {"start": v(39.62, 23.57) * mm, "end": v(40.37, 23.45) * mm});
            skLineSegment(sketch, "E369", {"start": v(40.37, 23.45) * mm, "end": v(41.13, 23.33) * mm});
            skLineSegment(sketch, "E370", {"start": v(41.13, 23.33) * mm, "end": v(41.88, 23.2) * mm});
            skLineSegment(sketch, "E371", {"start": v(41.88, 23.2) * mm, "end": v(42.63, 23.08) * mm});
            skLineSegment(sketch, "E372", {"start": v(42.63, 23.08) * mm, "end": v(43.38, 22.96) * mm});
            skLineSegment(sketch, "E373", {"start": v(43.38, 22.96) * mm, "end": v(44.13, 22.84) * mm});
            skLineSegment(sketch, "E374", {"start": v(44.13, 22.84) * mm, "end": v(44.88, 22.71) * mm});
            skLineSegment(sketch, "E375", {"start": v(44.88, 22.71) * mm, "end": v(45.63, 22.6) * mm});
            skLineSegment(sketch, "E376", {"start": v(45.63, 22.6) * mm, "end": v(46.38, 22.47) * mm});
            skLineSegment(sketch, "E377", {"start": v(46.38, 22.47) * mm, "end": v(47.12, 22.34) * mm});
            skLineSegment(sketch, "E378", {"start": v(47.12, 22.34) * mm, "end": v(47.86, 22.22) * mm});
            skLineSegment(sketch, "E379", {"start": v(47.86, 22.22) * mm, "end": v(48.6, 22.1) * mm});
            skLineSegment(sketch, "E380", {"start": v(48.6, 22.1) * mm, "end": v(49.35, 21.97) * mm});
            skLineSegment(sketch, "E381", {"start": v(49.35, 21.97) * mm, "end": v(50.09, 21.84) * mm});
            skLineSegment(sketch, "E382", {"start": v(50.09, 21.84) * mm, "end": v(50.83, 21.72) * mm});
            skLineSegment(sketch, "E383", {"start": v(50.83, 21.72) * mm, "end": v(51.56, 21.6) * mm});
            skLineSegment(sketch, "E384", {"start": v(51.56, 21.6) * mm, "end": v(52.3, 21.47) * mm});
            skLineSegment(sketch, "E385", {"start": v(52.3, 21.47) * mm, "end": v(53.03, 21.34) * mm});
            skLineSegment(sketch, "E386", {"start": v(53.03, 21.34) * mm, "end": v(53.77, 21.22) * mm});
            skLineSegment(sketch, "E387", {"start": v(53.77, 21.22) * mm, "end": v(54.5, 21.09) * mm});
            skLineSegment(sketch, "E388", {"start": v(54.5, 21.09) * mm, "end": v(55.23, 20.96) * mm});
            skLineSegment(sketch, "E389", {"start": v(55.23, 20.96) * mm, "end": v(55.96, 20.84) * mm});
            skLineSegment(sketch, "E390", {"start": v(55.96, 20.84) * mm, "end": v(56.68, 20.7) * mm});
            skLineSegment(sketch, "E391", {"start": v(56.68, 20.7) * mm, "end": v(57.4, 20.58) * mm});
            skLineSegment(sketch, "E392", {"start": v(57.4, 20.58) * mm, "end": v(58.13, 20.45) * mm});
            skLineSegment(sketch, "E393", {"start": v(58.13, 20.45) * mm, "end": v(58.85, 20.33) * mm});
            skLineSegment(sketch, "E394", {"start": v(58.85, 20.33) * mm, "end": v(59.57, 20.2) * mm});
            skLineSegment(sketch, "E395", {"start": v(59.57, 20.2) * mm, "end": v(60.3, 20.07) * mm});
            skLineSegment(sketch, "E396", {"start": v(60.3, 20.07) * mm, "end": v(61, 19.94) * mm});
            skLineSegment(sketch, "E397", {"start": v(61, 19.94) * mm, "end": v(61.72, 19.81) * mm});
            skLineSegment(sketch, "E398", {"start": v(61.72, 19.81) * mm, "end": v(62.44, 19.69) * mm});
            skLineSegment(sketch, "E399", {"start": v(62.44, 19.69) * mm, "end": v(63.15, 19.56) * mm});
            skLineSegment(sketch, "E400", {"start": v(63.15, 19.56) * mm, "end": v(63.86, 19.43) * mm});
            skLineSegment(sketch, "E401", {"start": v(63.86, 19.43) * mm, "end": v(64.57, 19.3) * mm});
            skLineSegment(sketch, "E402", {"start": v(64.57, 19.3) * mm, "end": v(65.27, 19.17) * mm});
            skLineSegment(sketch, "E403", {"start": v(65.27, 19.17) * mm, "end": v(65.98, 19.04) * mm});
            skLineSegment(sketch, "E404", {"start": v(65.98, 19.04) * mm, "end": v(66.68, 18.91) * mm});
            skLineSegment(sketch, "E405", {"start": v(66.68, 18.91) * mm, "end": v(67.38, 18.78) * mm});
            skLineSegment(sketch, "E406", {"start": v(67.38, 18.78) * mm, "end": v(68.08, 18.65) * mm});
            skLineSegment(sketch, "E407", {"start": v(68.08, 18.65) * mm, "end": v(68.78, 18.53) * mm});
            skLineSegment(sketch, "E408", {"start": v(68.78, 18.53) * mm, "end": v(69.48, 18.4) * mm});
            skLineSegment(sketch, "E409", {"start": v(69.48, 18.4) * mm, "end": v(70.17, 18.27) * mm});
            skLineSegment(sketch, "E410", {"start": v(70.17, 18.27) * mm, "end": v(70.86, 18.14) * mm});
            skLineSegment(sketch, "E411", {"start": v(70.86, 18.14) * mm, "end": v(71.55, 18) * mm});
            skLineSegment(sketch, "E412", {"start": v(71.55, 18) * mm, "end": v(72.24, 17.88) * mm});
            skLineSegment(sketch, "E413", {"start": v(72.24, 17.88) * mm, "end": v(72.93, 17.75) * mm});
            skLineSegment(sketch, "E414", {"start": v(72.93, 17.75) * mm, "end": v(73.61, 17.62) * mm});
            skLineSegment(sketch, "E415", {"start": v(73.61, 17.62) * mm, "end": v(74.3, 17.5) * mm});
            skLineSegment(sketch, "E416", {"start": v(74.3, 17.5) * mm, "end": v(74.97, 17.36) * mm});
            skLineSegment(sketch, "E417", {"start": v(74.97, 17.36) * mm, "end": v(75.65, 17.23) * mm});
            skLineSegment(sketch, "E418", {"start": v(75.65, 17.23) * mm, "end": v(76.33, 17.1) * mm});
            skLineSegment(sketch, "E419", {"start": v(76.33, 17.1) * mm, "end": v(77, 16.97) * mm});
            skLineSegment(sketch, "E420", {"start": v(77, 16.97) * mm, "end": v(77.67, 16.84) * mm});
            skLineSegment(sketch, "E421", {"start": v(77.67, 16.84) * mm, "end": v(78.34, 16.72) * mm});
            skLineSegment(sketch, "E422", {"start": v(78.34, 16.72) * mm, "end": v(79, 16.59) * mm});
            skLineSegment(sketch, "E423", {"start": v(79, 16.59) * mm, "end": v(79.67, 16.46) * mm});
            skLineSegment(sketch, "E424", {"start": v(79.67, 16.46) * mm, "end": v(80.34, 16.33) * mm});
            skLineSegment(sketch, "E425", {"start": v(80.34, 16.33) * mm, "end": v(81, 16.2) * mm});
            skLineSegment(sketch, "E426", {"start": v(81, 16.2) * mm, "end": v(81.66, 16.07) * mm});
            skLineSegment(sketch, "E427", {"start": v(81.66, 16.07) * mm, "end": v(82.31, 15.94) * mm});
            skLineSegment(sketch, "E428", {"start": v(82.31, 15.94) * mm, "end": v(82.97, 15.81) * mm});
            skLineSegment(sketch, "E429", {"start": v(82.97, 15.81) * mm, "end": v(83.62, 15.68) * mm});
            skLineSegment(sketch, "E430", {"start": v(83.62, 15.68) * mm, "end": v(84.27, 15.56) * mm});
            skLineSegment(sketch, "E431", {"start": v(84.27, 15.56) * mm, "end": v(84.91, 15.43) * mm});
            skLineSegment(sketch, "E432", {"start": v(84.91, 15.43) * mm, "end": v(85.56, 15.3) * mm});
            skLineSegment(sketch, "E433", {"start": v(85.56, 15.3) * mm, "end": v(86.2, 15.17) * mm});
            skLineSegment(sketch, "E434", {"start": v(86.2, 15.17) * mm, "end": v(86.84, 15.04) * mm});
            skLineSegment(sketch, "E435", {"start": v(86.84, 15.04) * mm, "end": v(87.48, 14.91) * mm});
            skLineSegment(sketch, "E436", {"start": v(87.48, 14.91) * mm, "end": v(88.11, 14.79) * mm});
            skLineSegment(sketch, "E437", {"start": v(88.11, 14.79) * mm, "end": v(88.75, 14.66) * mm});
            skLineSegment(sketch, "E438", {"start": v(88.75, 14.66) * mm, "end": v(89.38, 14.53) * mm});
            skLineSegment(sketch, "E439", {"start": v(89.38, 14.53) * mm, "end": v(90, 14.4) * mm});
            skLineSegment(sketch, "E440", {"start": v(90, 14.4) * mm, "end": v(90.63, 14.28) * mm});
            skLineSegment(sketch, "E441", {"start": v(90.63, 14.28) * mm, "end": v(91.25, 14.15) * mm});
            skLineSegment(sketch, "E442", {"start": v(91.25, 14.15) * mm, "end": v(91.87, 14.02) * mm});
            skLineSegment(sketch, "E443", {"start": v(91.87, 14.02) * mm, "end": v(92.5, 13.9) * mm});
            skLineSegment(sketch, "E444", {"start": v(92.5, 13.9) * mm, "end": v(93.1, 13.77) * mm});
            skLineSegment(sketch, "E445", {"start": v(93.1, 13.77) * mm, "end": v(93.72, 13.65) * mm});
            skLineSegment(sketch, "E446", {"start": v(93.72, 13.65) * mm, "end": v(94.33, 13.52) * mm});
            skLineSegment(sketch, "E447", {"start": v(94.33, 13.52) * mm, "end": v(94.94, 13.4) * mm});
            skLineSegment(sketch, "E448", {"start": v(94.94, 13.4) * mm, "end": v(95.54, 13.27) * mm});
            skLineSegment(sketch, "E449", {"start": v(95.54, 13.27) * mm, "end": v(96.15, 13.14) * mm});
            skLineSegment(sketch, "E450", {"start": v(96.15, 13.14) * mm, "end": v(96.75, 13.02) * mm});
            skLineSegment(sketch, "E451", {"start": v(96.75, 13.02) * mm, "end": v(97.34, 12.9) * mm});
            skLineSegment(sketch, "E452", {"start": v(97.34, 12.9) * mm, "end": v(97.94, 12.77) * mm});
            skLineSegment(sketch, "E453", {"start": v(97.94, 12.77) * mm, "end": v(98.53, 12.65) * mm});
            skLineSegment(sketch, "E454", {"start": v(98.53, 12.65) * mm, "end": v(99.12, 12.52) * mm});
            skLineSegment(sketch, "E455", {"start": v(99.12, 12.52) * mm, "end": v(99.7, 12.4) * mm});
            skLineSegment(sketch, "E456", {"start": v(99.7, 12.4) * mm, "end": v(100.29, 12.28) * mm});
            skLineSegment(sketch, "E457", {"start": v(100.29, 12.28) * mm, "end": v(100.87, 12.15) * mm});
            skLineSegment(sketch, "E458", {"start": v(100.87, 12.15) * mm, "end": v(101.45, 12.03) * mm});
            skLineSegment(sketch, "E459", {"start": v(101.45, 12.03) * mm, "end": v(102.02, 11.9) * mm});
            skLineSegment(sketch, "E460", {"start": v(102.02, 11.9) * mm, "end": v(102.6, 11.79) * mm});
            skLineSegment(sketch, "E461", {"start": v(102.6, 11.79) * mm, "end": v(103.17, 11.66) * mm});
            skLineSegment(sketch, "E462", {"start": v(103.17, 11.66) * mm, "end": v(103.73, 11.54) * mm});
            skLineSegment(sketch, "E463", {"start": v(103.73, 11.54) * mm, "end": v(104.3, 11.42) * mm});
            skLineSegment(sketch, "E464", {"start": v(104.3, 11.42) * mm, "end": v(104.86, 11.3) * mm});
            skLineSegment(sketch, "E465", {"start": v(104.86, 11.3) * mm, "end": v(105.42, 11.18) * mm});
            skLineSegment(sketch, "E466", {"start": v(105.42, 11.18) * mm, "end": v(105.97, 11.06) * mm});
            skLineSegment(sketch, "E467", {"start": v(105.97, 11.06) * mm, "end": v(106.53, 10.94) * mm});
            skLineSegment(sketch, "E468", {"start": v(106.53, 10.94) * mm, "end": v(107.07, 10.82) * mm});
            skLineSegment(sketch, "E469", {"start": v(107.07, 10.82) * mm, "end": v(107.62, 10.7) * mm});
            skLineSegment(sketch, "E470", {"start": v(107.62, 10.7) * mm, "end": v(108.17, 10.59) * mm});
            skLineSegment(sketch, "E471", {"start": v(108.17, 10.59) * mm, "end": v(108.7, 10.47) * mm});
            skLineSegment(sketch, "E472", {"start": v(108.7, 10.47) * mm, "end": v(109.24, 10.35) * mm});
            skLineSegment(sketch, "E473", {"start": v(109.24, 10.35) * mm, "end": v(109.78, 10.23) * mm});
            skLineSegment(sketch, "E474", {"start": v(109.78, 10.23) * mm, "end": v(110.31, 10.12) * mm});
            skLineSegment(sketch, "E475", {"start": v(110.31, 10.12) * mm, "end": v(110.84, 10) * mm});
            skLineSegment(sketch, "E476", {"start": v(110.84, 10) * mm, "end": v(111.37, 9.89) * mm});
            skLineSegment(sketch, "E477", {"start": v(111.37, 9.89) * mm, "end": v(111.89, 9.77) * mm});
            skLineSegment(sketch, "E478", {"start": v(111.89, 9.77) * mm, "end": v(112.4, 9.65) * mm});
            skLineSegment(sketch, "E479", {"start": v(112.4, 9.65) * mm, "end": v(112.92, 9.54) * mm});
            skLineSegment(sketch, "E480", {"start": v(112.92, 9.54) * mm, "end": v(113.44, 9.43) * mm});
            skLineSegment(sketch, "E481", {"start": v(113.44, 9.43) * mm, "end": v(113.95, 9.31) * mm});
            skLineSegment(sketch, "E482", {"start": v(113.95, 9.31) * mm, "end": v(114.45, 9.2) * mm});
            skLineSegment(sketch, "E483", {"start": v(114.45, 9.2) * mm, "end": v(114.96, 9.09) * mm});
            skLineSegment(sketch, "E484", {"start": v(114.96, 9.09) * mm, "end": v(115.46, 8.98) * mm});
            skLineSegment(sketch, "E485", {"start": v(115.46, 8.98) * mm, "end": v(115.96, 8.86) * mm});
            skLineSegment(sketch, "E486", {"start": v(115.96, 8.86) * mm, "end": v(116.45, 8.75) * mm});
            skLineSegment(sketch, "E487", {"start": v(116.45, 8.75) * mm, "end": v(116.94, 8.64) * mm});
            skLineSegment(sketch, "E488", {"start": v(116.94, 8.64) * mm, "end": v(117.43, 8.53) * mm});
            skLineSegment(sketch, "E489", {"start": v(117.43, 8.53) * mm, "end": v(117.92, 8.42) * mm});
            skLineSegment(sketch, "E490", {"start": v(117.92, 8.42) * mm, "end": v(118.4, 8.31) * mm});
            skLineSegment(sketch, "E491", {"start": v(118.4, 8.31) * mm, "end": v(118.88, 8.2) * mm});
            skLineSegment(sketch, "E492", {"start": v(118.88, 8.2) * mm, "end": v(119.35, 8.1) * mm});
            skLineSegment(sketch, "E493", {"start": v(119.35, 8.1) * mm, "end": v(119.82, 7.99) * mm});
            skLineSegment(sketch, "E494", {"start": v(119.82, 7.99) * mm, "end": v(120.3, 7.88) * mm});
            skLineSegment(sketch, "E495", {"start": v(120.3, 7.88) * mm, "end": v(120.76, 7.78) * mm});
            skLineSegment(sketch, "E496", {"start": v(120.76, 7.78) * mm, "end": v(121.22, 7.67) * mm});
            skLineSegment(sketch, "E497", {"start": v(121.22, 7.67) * mm, "end": v(121.68, 7.57) * mm});
            skLineSegment(sketch, "E498", {"start": v(121.68, 7.57) * mm, "end": v(122.13, 7.46) * mm});
            skLineSegment(sketch, "E499", {"start": v(122.13, 7.46) * mm, "end": v(122.59, 7.36) * mm});
            skLineSegment(sketch, "E500", {"start": v(122.59, 7.36) * mm, "end": v(123.03, 7.25) * mm});
            skLineSegment(sketch, "E501", {"start": v(123.03, 7.25) * mm, "end": v(123.48, 7.15) * mm});
            skLineSegment(sketch, "E502", {"start": v(123.48, 7.15) * mm, "end": v(123.92, 7.05) * mm});
            skLineSegment(sketch, "E503", {"start": v(123.92, 7.05) * mm, "end": v(124.36, 6.95) * mm});
            skLineSegment(sketch, "E504", {"start": v(124.36, 6.95) * mm, "end": v(124.8, 6.85) * mm});
            skLineSegment(sketch, "E505", {"start": v(124.8, 6.85) * mm, "end": v(125.23, 6.75) * mm});
            skLineSegment(sketch, "E506", {"start": v(125.23, 6.75) * mm, "end": v(125.65, 6.65) * mm});
            skLineSegment(sketch, "E507", {"start": v(125.65, 6.65) * mm, "end": v(126.08, 6.55) * mm});
            skLineSegment(sketch, "E508", {"start": v(126.08, 6.55) * mm, "end": v(126.5, 6.45) * mm});
            skLineSegment(sketch, "E509", {"start": v(126.5, 6.45) * mm, "end": v(126.92, 6.35) * mm});
            skLineSegment(sketch, "E510", {"start": v(126.92, 6.35) * mm, "end": v(127.33, 6.25) * mm});
            skLineSegment(sketch, "E511", {"start": v(127.33, 6.25) * mm, "end": v(127.74, 6.16) * mm});
            skLineSegment(sketch, "E512", {"start": v(127.74, 6.16) * mm, "end": v(128.15, 6.06) * mm});
            skLineSegment(sketch, "E513", {"start": v(128.15, 6.06) * mm, "end": v(128.56, 5.97) * mm});
            skLineSegment(sketch, "E514", {"start": v(128.56, 5.97) * mm, "end": v(128.96, 5.87) * mm});
            skLineSegment(sketch, "E515", {"start": v(128.96, 5.87) * mm, "end": v(129.35, 5.78) * mm});
            skLineSegment(sketch, "E516", {"start": v(129.35, 5.78) * mm, "end": v(129.75, 5.69) * mm});
            skLineSegment(sketch, "E517", {"start": v(129.75, 5.69) * mm, "end": v(130.13, 5.6) * mm});
            skLineSegment(sketch, "E518", {"start": v(130.13, 5.6) * mm, "end": v(130.52, 5.5) * mm});
            skLineSegment(sketch, "E519", {"start": v(130.52, 5.5) * mm, "end": v(130.9, 5.41) * mm});
            skLineSegment(sketch, "E520", {"start": v(130.9, 5.41) * mm, "end": v(131.28, 5.32) * mm});
            skLineSegment(sketch, "E521", {"start": v(131.28, 5.32) * mm, "end": v(131.66, 5.23) * mm});
            skLineSegment(sketch, "E522", {"start": v(131.66, 5.23) * mm, "end": v(132.03, 5.14) * mm});
            skLineSegment(sketch, "E523", {"start": v(132.03, 5.14) * mm, "end": v(132.4, 5.05) * mm});
            skLineSegment(sketch, "E524", {"start": v(132.4, 5.05) * mm, "end": v(132.76, 4.97) * mm});
            skLineSegment(sketch, "E525", {"start": v(132.76, 4.97) * mm, "end": v(133.12, 4.88) * mm});
            skLineSegment(sketch, "E526", {"start": v(133.12, 4.88) * mm, "end": v(133.48, 4.8) * mm});
            skLineSegment(sketch, "E527", {"start": v(133.48, 4.8) * mm, "end": v(133.83, 4.7) * mm});
            skLineSegment(sketch, "E528", {"start": v(133.83, 4.7) * mm, "end": v(134.18, 4.63) * mm});
            skLineSegment(sketch, "E529", {"start": v(134.18, 4.63) * mm, "end": v(134.53, 4.54) * mm});
            skLineSegment(sketch, "E530", {"start": v(134.53, 4.54) * mm, "end": v(134.87, 4.46) * mm});
            skLineSegment(sketch, "E531", {"start": v(134.87, 4.46) * mm, "end": v(135.21, 4.38) * mm});
            skLineSegment(sketch, "E532", {"start": v(135.21, 4.38) * mm, "end": v(135.55, 4.3) * mm});
            skLineSegment(sketch, "E533", {"start": v(135.55, 4.3) * mm, "end": v(135.88, 4.22) * mm});
            skLineSegment(sketch, "E534", {"start": v(135.88, 4.22) * mm, "end": v(136.2, 4.14) * mm});
            skLineSegment(sketch, "E535", {"start": v(136.2, 4.14) * mm, "end": v(136.53, 4.06) * mm});
            skLineSegment(sketch, "E536", {"start": v(136.53, 4.06) * mm, "end": v(136.85, 3.98) * mm});
            skLineSegment(sketch, "E537", {"start": v(136.85, 3.98) * mm, "end": v(137.16, 3.9) * mm});
            skLineSegment(sketch, "E538", {"start": v(137.16, 3.9) * mm, "end": v(137.48, 3.83) * mm});
            skLineSegment(sketch, "E539", {"start": v(137.48, 3.83) * mm, "end": v(137.79, 3.75) * mm});
            skLineSegment(sketch, "E540", {"start": v(137.79, 3.75) * mm, "end": v(138.1, 3.68) * mm});
            skLineSegment(sketch, "E541", {"start": v(138.1, 3.68) * mm, "end": v(138.4, 3.6) * mm});
            skLineSegment(sketch, "E542", {"start": v(138.4, 3.6) * mm, "end": v(138.69, 3.53) * mm});
            skLineSegment(sketch, "E543", {"start": v(138.69, 3.53) * mm, "end": v(138.98, 3.46) * mm});
            skLineSegment(sketch, "E544", {"start": v(138.98, 3.46) * mm, "end": v(139.27, 3.39) * mm});
            skLineSegment(sketch, "E545", {"start": v(139.27, 3.39) * mm, "end": v(139.56, 3.32) * mm});
            skLineSegment(sketch, "E546", {"start": v(139.56, 3.32) * mm, "end": v(139.84, 3.25) * mm});
            skLineSegment(sketch, "E547", {"start": v(139.84, 3.25) * mm, "end": v(140.12, 3.18) * mm});
            skLineSegment(sketch, "E548", {"start": v(140.12, 3.18) * mm, "end": v(140.4, 3.11) * mm});
            skLineSegment(sketch, "E549", {"start": v(140.4, 3.11) * mm, "end": v(140.66, 3.04) * mm});
            skLineSegment(sketch, "E550", {"start": v(140.66, 3.04) * mm, "end": v(140.93, 2.98) * mm});
            skLineSegment(sketch, "E551", {"start": v(140.93, 2.98) * mm, "end": v(141.2, 2.91) * mm});
            skLineSegment(sketch, "E552", {"start": v(141.2, 2.91) * mm, "end": v(141.45, 2.85) * mm});
            skLineSegment(sketch, "E553", {"start": v(141.45, 2.85) * mm, "end": v(141.7, 2.79) * mm});
            skLineSegment(sketch, "E554", {"start": v(141.7, 2.79) * mm, "end": v(141.96, 2.72) * mm});
            skLineSegment(sketch, "E555", {"start": v(141.96, 2.72) * mm, "end": v(142.2, 2.66) * mm});
            skLineSegment(sketch, "E556", {"start": v(142.2, 2.66) * mm, "end": v(142.45, 2.6) * mm});
            skLineSegment(sketch, "E557", {"start": v(142.45, 2.6) * mm, "end": v(142.69, 2.54) * mm});
            skLineSegment(sketch, "E558", {"start": v(142.69, 2.54) * mm, "end": v(142.93, 2.48) * mm});
            skLineSegment(sketch, "E559", {"start": v(142.93, 2.48) * mm, "end": v(143.16, 2.43) * mm});
            skLineSegment(sketch, "E560", {"start": v(143.16, 2.43) * mm, "end": v(143.39, 2.37) * mm});
            skLineSegment(sketch, "E561", {"start": v(143.39, 2.37) * mm, "end": v(143.6, 2.31) * mm});
            skLineSegment(sketch, "E562", {"start": v(143.6, 2.31) * mm, "end": v(143.83, 2.26) * mm});
            skLineSegment(sketch, "E563", {"start": v(143.83, 2.26) * mm, "end": v(144.04, 2.2) * mm});
            skLineSegment(sketch, "E564", {"start": v(144.04, 2.2) * mm, "end": v(144.26, 2.15) * mm});
            skLineSegment(sketch, "E565", {"start": v(144.26, 2.15) * mm, "end": v(144.46, 2.1) * mm});
            skLineSegment(sketch, "E566", {"start": v(144.46, 2.1) * mm, "end": v(144.67, 2.05) * mm});
            skLineSegment(sketch, "E567", {"start": v(144.67, 2.05) * mm, "end": v(144.87, 2) * mm});
            skLineSegment(sketch, "E568", {"start": v(144.87, 2) * mm, "end": v(145.07, 1.95) * mm});
            skLineSegment(sketch, "E569", {"start": v(145.07, 1.95) * mm, "end": v(145.26, 1.9) * mm});
            skLineSegment(sketch, "E570", {"start": v(145.26, 1.9) * mm, "end": v(145.45, 1.85) * mm});
            skLineSegment(sketch, "E571", {"start": v(145.45, 1.85) * mm, "end": v(145.63, 1.8) * mm});
            skLineSegment(sketch, "E572", {"start": v(145.63, 1.8) * mm, "end": v(145.8, 1.76) * mm});
            skLineSegment(sketch, "E573", {"start": v(145.8, 1.76) * mm, "end": v(145.99, 1.71) * mm});
            skLineSegment(sketch, "E574", {"start": v(145.99, 1.71) * mm, "end": v(146.16, 1.67) * mm});
            skLineSegment(sketch, "E575", {"start": v(146.16, 1.67) * mm, "end": v(146.33, 1.63) * mm});
            skLineSegment(sketch, "E576", {"start": v(146.33, 1.63) * mm, "end": v(146.5, 1.59) * mm});
            skLineSegment(sketch, "E577", {"start": v(146.5, 1.59) * mm, "end": v(146.65, 1.55) * mm});
            skLineSegment(sketch, "E578", {"start": v(146.65, 1.55) * mm, "end": v(146.8, 1.5) * mm});
            skLineSegment(sketch, "E579", {"start": v(146.8, 1.5) * mm, "end": v(146.96, 1.47) * mm});
            skLineSegment(sketch, "E580", {"start": v(146.96, 1.47) * mm, "end": v(147.1, 1.43) * mm});
            skLineSegment(sketch, "E581", {"start": v(147.1, 1.43) * mm, "end": v(147.25, 1.4) * mm});
            skLineSegment(sketch, "E582", {"start": v(147.25, 1.4) * mm, "end": v(147.39, 1.36) * mm});
            skLineSegment(sketch, "E583", {"start": v(147.39, 1.36) * mm, "end": v(147.52, 1.33) * mm});
            skLineSegment(sketch, "E584", {"start": v(147.52, 1.33) * mm, "end": v(147.65, 1.3) * mm});
            skLineSegment(sketch, "E585", {"start": v(147.65, 1.3) * mm, "end": v(147.77, 1.26) * mm});
            skLineSegment(sketch, "E586", {"start": v(147.77, 1.26) * mm, "end": v(147.9, 1.23) * mm});
            skLineSegment(sketch, "E587", {"start": v(147.9, 1.23) * mm, "end": v(148, 1.2) * mm});
            skLineSegment(sketch, "E588", {"start": v(148, 1.2) * mm, "end": v(148.12, 1.17) * mm});
            skLineSegment(sketch, "E589", {"start": v(148.12, 1.17) * mm, "end": v(148.22, 1.15) * mm});
            skLineSegment(sketch, "E590", {"start": v(148.22, 1.15) * mm, "end": v(148.32, 1.12) * mm});
            skLineSegment(sketch, "E591", {"start": v(148.32, 1.12) * mm, "end": v(148.41, 1.1) * mm});
            skLineSegment(sketch, "E592", {"start": v(148.41, 1.1) * mm, "end": v(148.5, 1.08) * mm});
            skLineSegment(sketch, "E593", {"start": v(148.5, 1.08) * mm, "end": v(148.58, 1.06) * mm});
            skLineSegment(sketch, "E594", {"start": v(148.58, 1.06) * mm, "end": v(148.66, 1.04) * mm});
            skLineSegment(sketch, "E595", {"start": v(148.66, 1.04) * mm, "end": v(148.73, 1.02) * mm});
            skLineSegment(sketch, "E596", {"start": v(148.73, 1.02) * mm, "end": v(148.8, 1) * mm});
            skLineSegment(sketch, "E597", {"start": v(148.8, 1) * mm, "end": v(148.85, 0.99) * mm});
            skLineSegment(sketch, "E598", {"start": v(148.85, 0.99) * mm, "end": v(148.9, 0.97) * mm});
            skLineSegment(sketch, "E599", {"start": v(148.9, 0.97) * mm, "end": v(148.95, 0.96) * mm});
            skLineSegment(sketch, "E600", {"start": v(148.95, 0.96) * mm, "end": v(148.99, 0.95) * mm});
            skLineSegment(sketch, "E601", {"start": v(148.99, 0.95) * mm, "end": v(149.03, 0.94) * mm});
            skLineSegment(sketch, "E602", {"start": v(149.03, 0.94) * mm, "end": v(149.06, 0.93) * mm});
            skLineSegment(sketch, "E603", {"start": v(149.06, 0.93) * mm, "end": v(149.09, 0.93) * mm});
            skLineSegment(sketch, "E604", {"start": v(149.09, 0.93) * mm, "end": v(149.1, 0.92) * mm});
            skLineSegment(sketch, "E605", {"start": v(149.1, 0.92) * mm, "end": v(149.13, 0.92) * mm});
            skLineSegment(sketch, "E606", {"start": v(149.13, 0.92) * mm, "end": v(149.15, 0.91) * mm});
            skLineSegment(sketch, "E607", {"start": v(149.15, 0.91) * mm, "end": v(149.16, 0.9) * mm});
            skLineSegment(sketch, "E608", {"start": v(149.16, 0.9) * mm, "end": v(149.17, 0.9) * mm});
            skLineSegment(sketch, "E609", {"start": v(149.17, 0.9) * mm, "end": v(149.18, 0.9) * mm});
            skLineSegment(sketch, "E610", {"start": v(149.18, 0.9) * mm, "end": v(149.19, 0.9) * mm});
            skLineSegment(sketch, "E611", {"start": v(149.19, 0.9) * mm, "end": v(149.2, 0.9) * mm});
            skLineSegment(sketch, "E612", {"start": v(149.2, 0.9) * mm, "end": v(149.2, 0.9) * mm});
            skLineSegment(sketch, "E613", {"start": v(149.2, 0.9) * mm, "end": v(150, 0.7) * mm});
            skLineSegment(sketch, "E614", {"start": v(-150, 0) * mm, "end": v(-150, -0.01) * mm});
            skLineSegment(sketch, "E615", {"start": v(-150, -0.01) * mm, "end": v(-150, -0.02) * mm});
            skLineSegment(sketch, "E616", {"start": v(-150, -0.02) * mm, "end": v(-150, -0.04) * mm});
            skLineSegment(sketch, "E617", {"start": v(-150, -0.04) * mm, "end": v(-150, -0.05) * mm});
            skLineSegment(sketch, "E618", {"start": v(-150, -0.05) * mm, "end": v(-149.99, -0.08) * mm});
            skLineSegment(sketch, "E619", {"start": v(-149.99, -0.08) * mm, "end": v(-149.98, -0.1) * mm});
            skLineSegment(sketch, "E620", {"start": v(-149.98, -0.1) * mm, "end": v(-149.98, -0.14) * mm});
            skLineSegment(sketch, "E621", {"start": v(-149.98, -0.14) * mm, "end": v(-149.97, -0.18) * mm});
            skLineSegment(sketch, "E622", {"start": v(-149.97, -0.18) * mm, "end": v(-149.96, -0.23) * mm});
            skLineSegment(sketch, "E623", {"start": v(-149.96, -0.23) * mm, "end": v(-149.95, -0.29) * mm});
            skLineSegment(sketch, "E624", {"start": v(-149.95, -0.29) * mm, "end": v(-149.94, -0.35) * mm});
            skLineSegment(sketch, "E625", {"start": v(-149.94, -0.35) * mm, "end": v(-149.93, -0.43) * mm});
            skLineSegment(sketch, "E626", {"start": v(-149.93, -0.43) * mm, "end": v(-149.92, -0.51) * mm});
            skLineSegment(sketch, "E627", {"start": v(-149.92, -0.51) * mm, "end": v(-149.9, -0.6) * mm});
            skLineSegment(sketch, "E628", {"start": v(-149.9, -0.6) * mm, "end": v(-149.88, -0.72) * mm});
            skLineSegment(sketch, "E629", {"start": v(-149.88, -0.72) * mm, "end": v(-149.86, -0.84) * mm});
            skLineSegment(sketch, "E630", {"start": v(-149.86, -0.84) * mm, "end": v(-149.84, -0.97) * mm});
            skLineSegment(sketch, "E631", {"start": v(-149.84, -0.97) * mm, "end": v(-149.82, -1.11) * mm});
            skLineSegment(sketch, "E632", {"start": v(-149.82, -1.11) * mm, "end": v(-149.8, -1.27) * mm});
            skLineSegment(sketch, "E633", {"start": v(-149.8, -1.27) * mm, "end": v(-149.76, -1.43) * mm});
            skLineSegment(sketch, "E634", {"start": v(-149.76, -1.43) * mm, "end": v(-149.73, -1.6) * mm});
            skLineSegment(sketch, "E635", {"start": v(-149.73, -1.6) * mm, "end": v(-149.7, -1.79) * mm});
            skLineSegment(sketch, "E636", {"start": v(-149.7, -1.79) * mm, "end": v(-149.66, -1.98) * mm});
            skLineSegment(sketch, "E637", {"start": v(-149.66, -1.98) * mm, "end": v(-149.62, -2.18) * mm});
            skLineSegment(sketch, "E638", {"start": v(-149.62, -2.18) * mm, "end": v(-149.58, -2.4) * mm});
            skLineSegment(sketch, "E639", {"start": v(-149.58, -2.4) * mm, "end": v(-149.54, -2.6) * mm});
            skLineSegment(sketch, "E640", {"start": v(-149.54, -2.6) * mm, "end": v(-149.49, -2.83) * mm});
            skLineSegment(sketch, "E641", {"start": v(-149.49, -2.83) * mm, "end": v(-149.44, -3.05) * mm});
            skLineSegment(sketch, "E642", {"start": v(-149.44, -3.05) * mm, "end": v(-149.38, -3.28) * mm});
            skLineSegment(sketch, "E643", {"start": v(-149.38, -3.28) * mm, "end": v(-149.33, -3.52) * mm});
            skLineSegment(sketch, "E644", {"start": v(-149.33, -3.52) * mm, "end": v(-149.27, -3.76) * mm});
            skLineSegment(sketch, "E645", {"start": v(-149.27, -3.76) * mm, "end": v(-149.2, -4) * mm});
            skLineSegment(sketch, "E646", {"start": v(-149.2, -4) * mm, "end": v(-149.13, -4.24) * mm});
            skLineSegment(sketch, "E647", {"start": v(-149.13, -4.24) * mm, "end": v(-149.06, -4.48) * mm});
            skLineSegment(sketch, "E648", {"start": v(-149.06, -4.48) * mm, "end": v(-148.99, -4.73) * mm});
            skLineSegment(sketch, "E649", {"start": v(-148.99, -4.73) * mm, "end": v(-148.9, -4.97) * mm});
            skLineSegment(sketch, "E650", {"start": v(-148.9, -4.97) * mm, "end": v(-148.82, -5.22) * mm});
            skLineSegment(sketch, "E651", {"start": v(-148.82, -5.22) * mm, "end": v(-148.73, -5.46) * mm});
            skLineSegment(sketch, "E652", {"start": v(-148.73, -5.46) * mm, "end": v(-148.64, -5.7) * mm});
            skLineSegment(sketch, "E653", {"start": v(-148.64, -5.7) * mm, "end": v(-148.54, -5.95) * mm});
            skLineSegment(sketch, "E654", {"start": v(-148.54, -5.95) * mm, "end": v(-148.44, -6.19) * mm});
            skLineSegment(sketch, "E655", {"start": v(-148.44, -6.19) * mm, "end": v(-148.34, -6.43) * mm});
            skLineSegment(sketch, "E656", {"start": v(-148.34, -6.43) * mm, "end": v(-148.23, -6.67) * mm});
            skLineSegment(sketch, "E657", {"start": v(-148.23, -6.67) * mm, "end": v(-148.12, -6.9) * mm});
            skLineSegment(sketch, "E658", {"start": v(-148.12, -6.9) * mm, "end": v(-148, -7.15) * mm});
            skLineSegment(sketch, "E659", {"start": v(-148, -7.15) * mm, "end": v(-147.88, -7.38) * mm});
            skLineSegment(sketch, "E660", {"start": v(-147.88, -7.38) * mm, "end": v(-147.76, -7.62) * mm});
            skLineSegment(sketch, "E661", {"start": v(-147.76, -7.62) * mm, "end": v(-147.63, -7.86) * mm});
            skLineSegment(sketch, "E662", {"start": v(-147.63, -7.86) * mm, "end": v(-147.5, -8.1) * mm});
            skLineSegment(sketch, "E663", {"start": v(-147.5, -8.1) * mm, "end": v(-147.36, -8.33) * mm});
            skLineSegment(sketch, "E664", {"start": v(-147.36, -8.33) * mm, "end": v(-147.22, -8.57) * mm});
            skLineSegment(sketch, "E665", {"start": v(-147.22, -8.57) * mm, "end": v(-147.07, -8.8) * mm});
            skLineSegment(sketch, "E666", {"start": v(-147.07, -8.8) * mm, "end": v(-146.92, -9.03) * mm});
            skLineSegment(sketch, "E667", {"start": v(-146.92, -9.03) * mm, "end": v(-146.77, -9.27) * mm});
            skLineSegment(sketch, "E668", {"start": v(-146.77, -9.27) * mm, "end": v(-146.61, -9.5) * mm});
            skLineSegment(sketch, "E669", {"start": v(-146.61, -9.5) * mm, "end": v(-146.45, -9.73) * mm});
            skLineSegment(sketch, "E670", {"start": v(-146.45, -9.73) * mm, "end": v(-146.29, -9.96) * mm});
            skLineSegment(sketch, "E671", {"start": v(-146.29, -9.96) * mm, "end": v(-146.12, -10.19) * mm});
            skLineSegment(sketch, "E672", {"start": v(-146.12, -10.19) * mm, "end": v(-145.94, -10.42) * mm});
            skLineSegment(sketch, "E673", {"start": v(-145.94, -10.42) * mm, "end": v(-145.77, -10.65) * mm});
            skLineSegment(sketch, "E674", {"start": v(-145.77, -10.65) * mm, "end": v(-145.59, -10.87) * mm});
            skLineSegment(sketch, "E675", {"start": v(-145.59, -10.87) * mm, "end": v(-145.4, -11.1) * mm});
            skLineSegment(sketch, "E676", {"start": v(-145.4, -11.1) * mm, "end": v(-145.21, -11.33) * mm});
            skLineSegment(sketch, "E677", {"start": v(-145.21, -11.33) * mm, "end": v(-145.02, -11.55) * mm});
            skLineSegment(sketch, "E678", {"start": v(-145.02, -11.55) * mm, "end": v(-144.82, -11.77) * mm});
            skLineSegment(sketch, "E679", {"start": v(-144.82, -11.77) * mm, "end": v(-144.62, -12) * mm});
            skLineSegment(sketch, "E680", {"start": v(-144.62, -12) * mm, "end": v(-144.41, -12.22) * mm});
            skLineSegment(sketch, "E681", {"start": v(-144.41, -12.22) * mm, "end": v(-144.2, -12.44) * mm});
            skLineSegment(sketch, "E682", {"start": v(-144.2, -12.44) * mm, "end": v(-144, -12.66) * mm});
            skLineSegment(sketch, "E683", {"start": v(-144, -12.66) * mm, "end": v(-143.78, -12.88) * mm});
            skLineSegment(sketch, "E684", {"start": v(-143.78, -12.88) * mm, "end": v(-143.56, -13.1) * mm});
            skLineSegment(sketch, "E685", {"start": v(-143.56, -13.1) * mm, "end": v(-143.33, -13.32) * mm});
            skLineSegment(sketch, "E686", {"start": v(-143.33, -13.32) * mm, "end": v(-143.1, -13.54) * mm});
            skLineSegment(sketch, "E687", {"start": v(-143.1, -13.54) * mm, "end": v(-142.87, -13.76) * mm});
            skLineSegment(sketch, "E688", {"start": v(-142.87, -13.76) * mm, "end": v(-142.63, -13.97) * mm});
            skLineSegment(sketch, "E689", {"start": v(-142.63, -13.97) * mm, "end": v(-142.4, -14.19) * mm});
            skLineSegment(sketch, "E690", {"start": v(-142.4, -14.19) * mm, "end": v(-142.15, -14.4) * mm});
            skLineSegment(sketch, "E691", {"start": v(-142.15, -14.4) * mm, "end": v(-141.9, -14.62) * mm});
            skLineSegment(sketch, "E692", {"start": v(-141.9, -14.62) * mm, "end": v(-141.65, -14.83) * mm});
            skLineSegment(sketch, "E693", {"start": v(-141.65, -14.83) * mm, "end": v(-141.4, -15.04) * mm});
            skLineSegment(sketch, "E694", {"start": v(-141.4, -15.04) * mm, "end": v(-141.13, -15.25) * mm});
            skLineSegment(sketch, "E695", {"start": v(-141.13, -15.25) * mm, "end": v(-140.87, -15.46) * mm});
            skLineSegment(sketch, "E696", {"start": v(-140.45, -13.88) * mm, "end": v(-140.2, -14.08) * mm});
            skLineSegment(sketch, "E697", {"start": v(-140.87, -15.46) * mm, "end": v(-140.6, -15.67) * mm});
            skLineSegment(sketch, "E698", {"start": v(-140.2, -14.08) * mm, "end": v(-139.94, -14.28) * mm});
            skLineSegment(sketch, "E699", {"start": v(-140.6, -15.67) * mm, "end": v(-140.33, -15.88) * mm});
            skLineSegment(sketch, "E700", {"start": v(-139.94, -14.28) * mm, "end": v(-139.69, -14.48) * mm});
            skLineSegment(sketch, "E701", {"start": v(-140.33, -15.88) * mm, "end": v(-140.05, -16.09) * mm});
            skLineSegment(sketch, "E702", {"start": v(-139.69, -14.48) * mm, "end": v(-139.43, -14.68) * mm});
            skLineSegment(sketch, "E703", {"start": v(-140.05, -16.09) * mm, "end": v(-139.77, -16.3) * mm});
            skLineSegment(sketch, "E704", {"start": v(-139.43, -14.68) * mm, "end": v(-139.16, -14.88) * mm});
            skLineSegment(sketch, "E705", {"start": v(-139.77, -16.3) * mm, "end": v(-139.5, -16.5) * mm});
            skLineSegment(sketch, "E706", {"start": v(-139.16, -14.88) * mm, "end": v(-138.9, -15.08) * mm});
            skLineSegment(sketch, "E707", {"start": v(-139.5, -16.5) * mm, "end": v(-139.2, -16.7) * mm});
            skLineSegment(sketch, "E708", {"start": v(-138.9, -15.08) * mm, "end": v(-138.62, -15.28) * mm});
            skLineSegment(sketch, "E709", {"start": v(-139.2, -16.7) * mm, "end": v(-138.91, -16.9) * mm});
            skLineSegment(sketch, "E710", {"start": v(-138.62, -15.28) * mm, "end": v(-138.34, -15.47) * mm});
            skLineSegment(sketch, "E711", {"start": v(-138.91, -16.9) * mm, "end": v(-138.62, -17.1) * mm});
            skLineSegment(sketch, "E712", {"start": v(-138.34, -15.47) * mm, "end": v(-138.06, -15.67) * mm});
            skLineSegment(sketch, "E713", {"start": v(-138.62, -17.1) * mm, "end": v(-138.32, -17.3) * mm});
            skLineSegment(sketch, "E714", {"start": v(-138.06, -15.67) * mm, "end": v(-137.78, -15.87) * mm});
            skLineSegment(sketch, "E715", {"start": v(-138.32, -17.3) * mm, "end": v(-138.02, -17.51) * mm});
            skLineSegment(sketch, "E716", {"start": v(-137.78, -15.87) * mm, "end": v(-137.5, -16.06) * mm});
            skLineSegment(sketch, "E717", {"start": v(-138.02, -17.51) * mm, "end": v(-137.71, -17.7) * mm});
            skLineSegment(sketch, "E718", {"start": v(-137.5, -16.06) * mm, "end": v(-137.2, -16.25) * mm});
            skLineSegment(sketch, "E719", {"start": v(-137.71, -17.7) * mm, "end": v(-137.4, -17.9) * mm});
            skLineSegment(sketch, "E720", {"start": v(-137.2, -16.25) * mm, "end": v(-136.9, -16.45) * mm});
            skLineSegment(sketch, "E721", {"start": v(-137.4, -17.9) * mm, "end": v(-137.09, -18.1) * mm});
            skLineSegment(sketch, "E722", {"start": v(-136.9, -16.45) * mm, "end": v(-136.6, -16.64) * mm});
            skLineSegment(sketch, "E723", {"start": v(-137.09, -18.1) * mm, "end": v(-136.77, -18.3) * mm});
            skLineSegment(sketch, "E724", {"start": v(-136.6, -16.64) * mm, "end": v(-136.3, -16.83) * mm});
            skLineSegment(sketch, "E725", {"start": v(-136.77, -18.3) * mm, "end": v(-136.45, -18.5) * mm});
            skLineSegment(sketch, "E726", {"start": v(-136.3, -16.83) * mm, "end": v(-136, -17.02) * mm});
            skLineSegment(sketch, "E727", {"start": v(-136.45, -18.5) * mm, "end": v(-136.13, -18.7) * mm});
            skLineSegment(sketch, "E728", {"start": v(-136, -17.02) * mm, "end": v(-135.68, -17.21) * mm});
            skLineSegment(sketch, "E729", {"start": v(-136.13, -18.7) * mm, "end": v(-135.8, -18.89) * mm});
            skLineSegment(sketch, "E730", {"start": v(-135.68, -17.21) * mm, "end": v(-135.36, -17.4) * mm});
            skLineSegment(sketch, "E731", {"start": v(-135.8, -18.89) * mm, "end": v(-135.46, -19.08) * mm});
            skLineSegment(sketch, "E732", {"start": v(-135.36, -17.4) * mm, "end": v(-135.05, -17.59) * mm});
            skLineSegment(sketch, "E733", {"start": v(-135.46, -19.08) * mm, "end": v(-135.13, -19.27) * mm});
            skLineSegment(sketch, "E734", {"start": v(-135.05, -17.59) * mm, "end": v(-134.72, -17.77) * mm});
            skLineSegment(sketch, "E735", {"start": v(-135.13, -19.27) * mm, "end": v(-134.79, -19.46) * mm});
            skLineSegment(sketch, "E736", {"start": v(-134.72, -17.77) * mm, "end": v(-134.4, -17.96) * mm});
            skLineSegment(sketch, "E737", {"start": v(-134.79, -19.46) * mm, "end": v(-134.45, -19.65) * mm});
            skLineSegment(sketch, "E738", {"start": v(-134.4, -17.96) * mm, "end": v(-134.07, -18.15) * mm});
            skLineSegment(sketch, "E739", {"start": v(-134.45, -19.65) * mm, "end": v(-134.1, -19.84) * mm});
            skLineSegment(sketch, "E740", {"start": v(-134.07, -18.15) * mm, "end": v(-133.73, -18.33) * mm});
            skLineSegment(sketch, "E741", {"start": v(-134.1, -19.84) * mm, "end": v(-133.75, -20.02) * mm});
            skLineSegment(sketch, "E742", {"start": v(-133.73, -18.33) * mm, "end": v(-133.4, -18.51) * mm});
            skLineSegment(sketch, "E743", {"start": v(-133.75, -20.02) * mm, "end": v(-133.4, -20.21) * mm});
            skLineSegment(sketch, "E744", {"start": v(-133.4, -18.51) * mm, "end": v(-133.05, -18.7) * mm});
            skLineSegment(sketch, "E745", {"start": v(-133.4, -20.21) * mm, "end": v(-133.04, -20.4) * mm});
            skLineSegment(sketch, "E746", {"start": v(-133.05, -18.7) * mm, "end": v(-132.7, -18.88) * mm});
            skLineSegment(sketch, "E747", {"start": v(-133.04, -20.4) * mm, "end": v(-132.67, -20.58) * mm});
            skLineSegment(sketch, "E748", {"start": v(-132.7, -18.88) * mm, "end": v(-132.36, -19.06) * mm});
            skLineSegment(sketch, "E749", {"start": v(-132.67, -20.58) * mm, "end": v(-132.3, -20.76) * mm});
            skLineSegment(sketch, "E750", {"start": v(-132.36, -19.06) * mm, "end": v(-132, -19.24) * mm});
            skLineSegment(sketch, "E751", {"start": v(-132.3, -20.76) * mm, "end": v(-131.94, -20.94) * mm});
            skLineSegment(sketch, "E752", {"start": v(-132, -19.24) * mm, "end": v(-131.65, -19.42) * mm});
            skLineSegment(sketch, "E753", {"start": v(-131.94, -20.94) * mm, "end": v(-131.57, -21.12) * mm});
            skLineSegment(sketch, "E754", {"start": v(-131.65, -19.42) * mm, "end": v(-131.29, -19.6) * mm});
            skLineSegment(sketch, "E755", {"start": v(-131.57, -21.12) * mm, "end": v(-131.2, -21.3) * mm});
            skLineSegment(sketch, "E756", {"start": v(-131.29, -19.6) * mm, "end": v(-130.92, -19.77) * mm});
            skLineSegment(sketch, "E757", {"start": v(-131.2, -21.3) * mm, "end": v(-130.81, -21.48) * mm});
            skLineSegment(sketch, "E758", {"start": v(-130.92, -19.77) * mm, "end": v(-130.55, -19.94) * mm});
            skLineSegment(sketch, "E759", {"start": v(-130.81, -21.48) * mm, "end": v(-130.43, -21.66) * mm});
            skLineSegment(sketch, "E760", {"start": v(-130.55, -19.94) * mm, "end": v(-130.18, -20.12) * mm});
            skLineSegment(sketch, "E761", {"start": v(-130.43, -21.66) * mm, "end": v(-130.04, -21.83) * mm});
            skLineSegment(sketch, "E762", {"start": v(-130.18, -20.12) * mm, "end": v(-129.8, -20.3) * mm});
            skLineSegment(sketch, "E763", {"start": v(-130.04, -21.83) * mm, "end": v(-129.65, -22) * mm});
            skLineSegment(sketch, "E764", {"start": v(-129.8, -20.3) * mm, "end": v(-129.43, -20.46) * mm});
            skLineSegment(sketch, "E765", {"start": v(-129.65, -22) * mm, "end": v(-129.26, -22.18) * mm});
            skLineSegment(sketch, "E766", {"start": v(-129.43, -20.46) * mm, "end": v(-129.05, -20.64) * mm});
            skLineSegment(sketch, "E767", {"start": v(-129.26, -22.18) * mm, "end": v(-128.86, -22.35) * mm});
            skLineSegment(sketch, "E768", {"start": v(-129.05, -20.64) * mm, "end": v(-128.66, -20.8) * mm});
            skLineSegment(sketch, "E769", {"start": v(-128.86, -22.35) * mm, "end": v(-128.46, -22.53) * mm});
            skLineSegment(sketch, "E770", {"start": v(-128.66, -20.8) * mm, "end": v(-128.27, -20.97) * mm});
            skLineSegment(sketch, "E771", {"start": v(-128.46, -22.53) * mm, "end": v(-128.05, -22.7) * mm});
            skLineSegment(sketch, "E772", {"start": v(-128.27, -20.97) * mm, "end": v(-127.88, -21.14) * mm});
            skLineSegment(sketch, "E773", {"start": v(-128.05, -22.7) * mm, "end": v(-127.64, -22.86) * mm});
            skLineSegment(sketch, "E774", {"start": v(-127.88, -21.14) * mm, "end": v(-127.48, -21.3) * mm});
            skLineSegment(sketch, "E775", {"start": v(-127.64, -22.86) * mm, "end": v(-127.23, -23.03) * mm});
            skLineSegment(sketch, "E776", {"start": v(-127.48, -21.3) * mm, "end": v(-127.08, -21.47) * mm});
            skLineSegment(sketch, "E777", {"start": v(-127.23, -23.03) * mm, "end": v(-126.82, -23.2) * mm});
            skLineSegment(sketch, "E778", {"start": v(-127.08, -21.47) * mm, "end": v(-126.68, -21.64) * mm});
            skLineSegment(sketch, "E779", {"start": v(-126.82, -23.2) * mm, "end": v(-126.4, -23.36) * mm});
            skLineSegment(sketch, "E780", {"start": v(-126.68, -21.64) * mm, "end": v(-126.27, -21.8) * mm});
            skLineSegment(sketch, "E781", {"start": v(-126.4, -23.36) * mm, "end": v(-125.98, -23.53) * mm});
            skLineSegment(sketch, "E782", {"start": v(-126.27, -21.8) * mm, "end": v(-125.86, -21.96) * mm});
            skLineSegment(sketch, "E783", {"start": v(-125.98, -23.53) * mm, "end": v(-125.55, -23.69) * mm});
            skLineSegment(sketch, "E784", {"start": v(-125.86, -21.96) * mm, "end": v(-125.44, -22.13) * mm});
            skLineSegment(sketch, "E785", {"start": v(-125.55, -23.69) * mm, "end": v(-125.12, -23.85) * mm});
            skLineSegment(sketch, "E786", {"start": v(-125.44, -22.13) * mm, "end": v(-125.02, -22.29) * mm});
            skLineSegment(sketch, "E787", {"start": v(-125.12, -23.85) * mm, "end": v(-124.7, -24.01) * mm});
            skLineSegment(sketch, "E788", {"start": v(-125.02, -22.29) * mm, "end": v(-124.6, -22.44) * mm});
            skLineSegment(sketch, "E789", {"start": v(-124.7, -24.01) * mm, "end": v(-124.25, -24.17) * mm});
            skLineSegment(sketch, "E790", {"start": v(-124.6, -22.44) * mm, "end": v(-124.18, -22.6) * mm});
            skLineSegment(sketch, "E791", {"start": v(-124.25, -24.17) * mm, "end": v(-123.82, -24.33) * mm});
            skLineSegment(sketch, "E792", {"start": v(-124.18, -22.6) * mm, "end": v(-123.75, -22.76) * mm});
            skLineSegment(sketch, "E793", {"start": v(-123.82, -24.33) * mm, "end": v(-123.37, -24.48) * mm});
            skLineSegment(sketch, "E794", {"start": v(-123.75, -22.76) * mm, "end": v(-123.32, -22.91) * mm});
            skLineSegment(sketch, "E795", {"start": v(-123.37, -24.48) * mm, "end": v(-122.93, -24.64) * mm});
            skLineSegment(sketch, "E796", {"start": v(-123.32, -22.91) * mm, "end": v(-122.88, -23.07) * mm});
            skLineSegment(sketch, "E797", {"start": v(-122.93, -24.64) * mm, "end": v(-122.48, -24.8) * mm});
            skLineSegment(sketch, "E798", {"start": v(-122.88, -23.07) * mm, "end": v(-122.44, -23.22) * mm});
            skLineSegment(sketch, "E799", {"start": v(-122.48, -24.8) * mm, "end": v(-122.02, -24.95) * mm});
            skLineSegment(sketch, "E800", {"start": v(-122.44, -23.22) * mm, "end": v(-122, -23.37) * mm});
            skLineSegment(sketch, "E801", {"start": v(-122.02, -24.95) * mm, "end": v(-121.57, -25.1) * mm});
            skLineSegment(sketch, "E802", {"start": v(-122, -23.37) * mm, "end": v(-121.55, -23.52) * mm});
            skLineSegment(sketch, "E803", {"start": v(-121.57, -25.1) * mm, "end": v(-121.1, -25.25) * mm});
            skLineSegment(sketch, "E804", {"start": v(-121.55, -23.52) * mm, "end": v(-121.1, -23.67) * mm});
            skLineSegment(sketch, "E805", {"start": v(-121.1, -25.25) * mm, "end": v(-120.65, -25.4) * mm});
            skLineSegment(sketch, "E806", {"start": v(-121.1, -23.67) * mm, "end": v(-120.65, -23.82) * mm});
            skLineSegment(sketch, "E807", {"start": v(-120.65, -25.4) * mm, "end": v(-120.18, -25.54) * mm});
            skLineSegment(sketch, "E808", {"start": v(-120.65, -23.82) * mm, "end": v(-120.2, -23.96) * mm});
            skLineSegment(sketch, "E809", {"start": v(-120.18, -25.54) * mm, "end": v(-119.71, -25.69) * mm});
            skLineSegment(sketch, "E810", {"start": v(-120.2, -23.96) * mm, "end": v(-119.73, -24.1) * mm});
            skLineSegment(sketch, "E811", {"start": v(-119.71, -25.69) * mm, "end": v(-119.24, -25.83) * mm});
            skLineSegment(sketch, "E812", {"start": v(-119.73, -24.1) * mm, "end": v(-119.27, -24.25) * mm});
            skLineSegment(sketch, "E813", {"start": v(-119.24, -25.83) * mm, "end": v(-118.76, -25.98) * mm});
            skLineSegment(sketch, "E814", {"start": v(-119.27, -24.25) * mm, "end": v(-118.8, -24.4) * mm});
            skLineSegment(sketch, "E815", {"start": v(-118.76, -25.98) * mm, "end": v(-118.28, -26.12) * mm});
            skLineSegment(sketch, "E816", {"start": v(-118.8, -24.4) * mm, "end": v(-118.34, -24.54) * mm});
            skLineSegment(sketch, "E817", {"start": v(-118.28, -26.12) * mm, "end": v(-117.8, -26.26) * mm});
            skLineSegment(sketch, "E818", {"start": v(-118.34, -24.54) * mm, "end": v(-117.86, -24.68) * mm});
            skLineSegment(sketch, "E819", {"start": v(-117.8, -26.26) * mm, "end": v(-117.31, -26.4) * mm});
            skLineSegment(sketch, "E820", {"start": v(-117.86, -24.68) * mm, "end": v(-117.39, -24.82) * mm});
            skLineSegment(sketch, "E821", {"start": v(-117.31, -26.4) * mm, "end": v(-116.83, -26.53) * mm});
            skLineSegment(sketch, "E822", {"start": v(-117.39, -24.82) * mm, "end": v(-116.9, -24.95) * mm});
            skLineSegment(sketch, "E823", {"start": v(-116.83, -26.53) * mm, "end": v(-116.33, -26.67) * mm});
            skLineSegment(sketch, "E824", {"start": v(-116.9, -24.95) * mm, "end": v(-116.42, -25.09) * mm});
            skLineSegment(sketch, "E825", {"start": v(-116.33, -26.67) * mm, "end": v(-115.84, -26.8) * mm});
            skLineSegment(sketch, "E826", {"start": v(-116.42, -25.09) * mm, "end": v(-115.94, -25.22) * mm});
            skLineSegment(sketch, "E827", {"start": v(-115.84, -26.8) * mm, "end": v(-115.34, -26.94) * mm});
            skLineSegment(sketch, "E828", {"start": v(-115.94, -25.22) * mm, "end": v(-115.45, -25.36) * mm});
            skLineSegment(sketch, "E829", {"start": v(-115.34, -26.94) * mm, "end": v(-114.84, -27.07) * mm});
            skLineSegment(sketch, "E830", {"start": v(-115.45, -25.36) * mm, "end": v(-114.96, -25.49) * mm});
            skLineSegment(sketch, "E831", {"start": v(-114.84, -27.07) * mm, "end": v(-114.33, -27.2) * mm});
            skLineSegment(sketch, "E832", {"start": v(-114.96, -25.49) * mm, "end": v(-114.46, -25.62) * mm});
            skLineSegment(sketch, "E833", {"start": v(-114.33, -27.2) * mm, "end": v(-113.82, -27.33) * mm});
            skLineSegment(sketch, "E834", {"start": v(-114.46, -25.62) * mm, "end": v(-113.96, -25.75) * mm});
            skLineSegment(sketch, "E835", {"start": v(-113.82, -27.33) * mm, "end": v(-113.31, -27.46) * mm});
            skLineSegment(sketch, "E836", {"start": v(-113.96, -25.75) * mm, "end": v(-113.46, -25.88) * mm});
            skLineSegment(sketch, "E837", {"start": v(-113.31, -27.46) * mm, "end": v(-112.8, -27.59) * mm});
            skLineSegment(sketch, "E838", {"start": v(-113.46, -25.88) * mm, "end": v(-112.95, -26) * mm});
            skLineSegment(sketch, "E839", {"start": v(-112.8, -27.59) * mm, "end": v(-112.28, -27.71) * mm});
            skLineSegment(sketch, "E840", {"start": v(-112.95, -26) * mm, "end": v(-112.45, -26.13) * mm});
            skLineSegment(sketch, "E841", {"start": v(-112.28, -27.71) * mm, "end": v(-111.76, -27.84) * mm});
            skLineSegment(sketch, "E842", {"start": v(-112.45, -26.13) * mm, "end": v(-111.93, -26.25) * mm});
            skLineSegment(sketch, "E843", {"start": v(-111.76, -27.84) * mm, "end": v(-111.24, -27.96) * mm});
            skLineSegment(sketch, "E844", {"start": v(-111.93, -26.25) * mm, "end": v(-111.42, -26.38) * mm});
            skLineSegment(sketch, "E845", {"start": v(-111.24, -27.96) * mm, "end": v(-110.71, -28.08) * mm});
            skLineSegment(sketch, "E846", {"start": v(-111.42, -26.38) * mm, "end": v(-110.9, -26.5) * mm});
            skLineSegment(sketch, "E847", {"start": v(-110.71, -28.08) * mm, "end": v(-110.18, -28.2) * mm});
            skLineSegment(sketch, "E848", {"start": v(-110.9, -26.5) * mm, "end": v(-110.38, -26.62) * mm});
            skLineSegment(sketch, "E849", {"start": v(-110.18, -28.2) * mm, "end": v(-109.65, -28.32) * mm});
            skLineSegment(sketch, "E850", {"start": v(-110.38, -26.62) * mm, "end": v(-109.86, -26.74) * mm});
            skLineSegment(sketch, "E851", {"start": v(-109.65, -28.32) * mm, "end": v(-109.11, -28.43) * mm});
            skLineSegment(sketch, "E852", {"start": v(-109.86, -26.74) * mm, "end": v(-109.33, -26.85) * mm});
            skLineSegment(sketch, "E853", {"start": v(-109.11, -28.43) * mm, "end": v(-108.58, -28.55) * mm});
            skLineSegment(sketch, "E854", {"start": v(-109.33, -26.85) * mm, "end": v(-108.8, -26.97) * mm});
            skLineSegment(sketch, "E855", {"start": v(-108.58, -28.55) * mm, "end": v(-108.03, -28.66) * mm});
            skLineSegment(sketch, "E856", {"start": v(-108.8, -26.97) * mm, "end": v(-108.27, -27.08) * mm});
            skLineSegment(sketch, "E857", {"start": v(-108.03, -28.66) * mm, "end": v(-107.49, -28.78) * mm});
            skLineSegment(sketch, "E858", {"start": v(-108.27, -27.08) * mm, "end": v(-107.73, -27.2) * mm});
            skLineSegment(sketch, "E859", {"start": v(-107.49, -28.78) * mm, "end": v(-106.94, -28.89) * mm});
            skLineSegment(sketch, "E860", {"start": v(-107.73, -27.2) * mm, "end": v(-107.2, -27.3) * mm});
            skLineSegment(sketch, "E861", {"start": v(-106.94, -28.89) * mm, "end": v(-106.4, -29) * mm});
            skLineSegment(sketch, "E862", {"start": v(-107.2, -27.3) * mm, "end": v(-106.65, -27.42) * mm});
            skLineSegment(sketch, "E863", {"start": v(-106.4, -29) * mm, "end": v(-105.84, -29.1) * mm});
            skLineSegment(sketch, "E864", {"start": v(-106.65, -27.42) * mm, "end": v(-106.1, -27.52) * mm});
            skLineSegment(sketch, "E865", {"start": v(-105.84, -29.1) * mm, "end": v(-105.28, -29.21) * mm});
            skLineSegment(sketch, "E866", {"start": v(-106.1, -27.52) * mm, "end": v(-105.56, -27.63) * mm});
            skLineSegment(sketch, "E867", {"start": v(-105.28, -29.21) * mm, "end": v(-104.72, -29.32) * mm});
            skLineSegment(sketch, "E868", {"start": v(-105.56, -27.63) * mm, "end": v(-105, -27.74) * mm});
            skLineSegment(sketch, "E869", {"start": v(-104.72, -29.32) * mm, "end": v(-104.16, -29.42) * mm});
            skLineSegment(sketch, "E870", {"start": v(-105, -27.74) * mm, "end": v(-104.45, -27.84) * mm});
            skLineSegment(sketch, "E871", {"start": v(-104.16, -29.42) * mm, "end": v(-103.6, -29.52) * mm});
            skLineSegment(sketch, "E872", {"start": v(-104.45, -27.84) * mm, "end": v(-103.9, -27.94) * mm});
            skLineSegment(sketch, "E873", {"start": v(-103.6, -29.52) * mm, "end": v(-103.03, -29.62) * mm});
            skLineSegment(sketch, "E874", {"start": v(-103.9, -27.94) * mm, "end": v(-103.34, -28.04) * mm});
            skLineSegment(sketch, "E875", {"start": v(-103.03, -29.62) * mm, "end": v(-102.46, -29.72) * mm});
            skLineSegment(sketch, "E876", {"start": v(-103.34, -28.04) * mm, "end": v(-102.77, -28.14) * mm});
            skLineSegment(sketch, "E877", {"start": v(-102.46, -29.72) * mm, "end": v(-101.89, -29.82) * mm});
            skLineSegment(sketch, "E878", {"start": v(-102.77, -28.14) * mm, "end": v(-102.2, -28.24) * mm});
            skLineSegment(sketch, "E879", {"start": v(-101.89, -29.82) * mm, "end": v(-101.3, -29.91) * mm});
            skLineSegment(sketch, "E880", {"start": v(-102.2, -28.24) * mm, "end": v(-101.64, -28.34) * mm});
            skLineSegment(sketch, "E881", {"start": v(-101.3, -29.91) * mm, "end": v(-100.73, -30) * mm});
            skLineSegment(sketch, "E882", {"start": v(-101.64, -28.34) * mm, "end": v(-101.07, -28.43) * mm});
            skLineSegment(sketch, "E883", {"start": v(-100.73, -30) * mm, "end": v(-100.15, -30.1) * mm});
            skLineSegment(sketch, "E884", {"start": v(-101.07, -28.43) * mm, "end": v(-100.5, -28.53) * mm});
            skLineSegment(sketch, "E885", {"start": v(-100.15, -30.1) * mm, "end": v(-99.56, -30.2) * mm});
            skLineSegment(sketch, "E886", {"start": v(-100.5, -28.53) * mm, "end": v(-99.92, -28.62) * mm});
            skLineSegment(sketch, "E887", {"start": v(-99.56, -30.2) * mm, "end": v(-98.98, -30.28) * mm});
            skLineSegment(sketch, "E888", {"start": v(-99.92, -28.62) * mm, "end": v(-99.34, -28.71) * mm});
            skLineSegment(sketch, "E889", {"start": v(-98.98, -30.28) * mm, "end": v(-98.39, -30.37) * mm});
            skLineSegment(sketch, "E890", {"start": v(-99.34, -28.71) * mm, "end": v(-98.75, -28.8) * mm});
            skLineSegment(sketch, "E891", {"start": v(-98.39, -30.37) * mm, "end": v(-97.8, -30.46) * mm});
            skLineSegment(sketch, "E892", {"start": v(-98.75, -28.8) * mm, "end": v(-98.17, -28.89) * mm});
            skLineSegment(sketch, "E893", {"start": v(-97.8, -30.46) * mm, "end": v(-97.2, -30.54) * mm});
            skLineSegment(sketch, "E894", {"start": v(-98.17, -28.89) * mm, "end": v(-97.58, -28.97) * mm});
            skLineSegment(sketch, "E895", {"start": v(-97.2, -30.54) * mm, "end": v(-96.6, -30.63) * mm});
            skLineSegment(sketch, "E896", {"start": v(-97.58, -28.97) * mm, "end": v(-97, -29.06) * mm});
            skLineSegment(sketch, "E897", {"start": v(-96.6, -30.63) * mm, "end": v(-96, -30.71) * mm});
            skLineSegment(sketch, "E898", {"start": v(-97, -29.06) * mm, "end": v(-96.4, -29.14) * mm});
            skLineSegment(sketch, "E899", {"start": v(-96, -30.71) * mm, "end": v(-95.4, -30.8) * mm});
            skLineSegment(sketch, "E900", {"start": v(-96.4, -29.14) * mm, "end": v(-95.8, -29.22) * mm});
            skLineSegment(sketch, "E901", {"start": v(-95.4, -30.8) * mm, "end": v(-94.8, -30.87) * mm});
            skLineSegment(sketch, "E902", {"start": v(-95.8, -29.22) * mm, "end": v(-95.2, -29.3) * mm});
            skLineSegment(sketch, "E903", {"start": v(-94.8, -30.87) * mm, "end": v(-94.18, -30.95) * mm});
            skLineSegment(sketch, "E904", {"start": v(-95.2, -29.3) * mm, "end": v(-94.6, -29.38) * mm});
            skLineSegment(sketch, "E905", {"start": v(-94.18, -30.95) * mm, "end": v(-93.57, -31.03) * mm});
            skLineSegment(sketch, "E906", {"start": v(-94.6, -29.38) * mm, "end": v(-94, -29.46) * mm});
            skLineSegment(sketch, "E907", {"start": v(-93.57, -31.03) * mm, "end": v(-92.96, -31.1) * mm});
            skLineSegment(sketch, "E908", {"start": v(-94, -29.46) * mm, "end": v(-93.4, -29.54) * mm});
            skLineSegment(sketch, "E909", {"start": v(-92.96, -31.1) * mm, "end": v(-92.34, -31.17) * mm});
            skLineSegment(sketch, "E910", {"start": v(-93.4, -29.54) * mm, "end": v(-92.78, -29.61) * mm});
            skLineSegment(sketch, "E911", {"start": v(-92.34, -31.17) * mm, "end": v(-91.72, -31.25) * mm});
            skLineSegment(sketch, "E912", {"start": v(-92.78, -29.61) * mm, "end": v(-92.17, -29.68) * mm});
            skLineSegment(sketch, "E913", {"start": v(-91.72, -31.25) * mm, "end": v(-91.1, -31.32) * mm});
            skLineSegment(sketch, "E914", {"start": v(-92.17, -29.68) * mm, "end": v(-91.56, -29.76) * mm});
            skLineSegment(sketch, "E915", {"start": v(-91.1, -31.32) * mm, "end": v(-90.48, -31.39) * mm});
            skLineSegment(sketch, "E916", {"start": v(-91.56, -29.76) * mm, "end": v(-90.94, -29.83) * mm});
            skLineSegment(sketch, "E917", {"start": v(-90.48, -31.39) * mm, "end": v(-89.85, -31.45) * mm});
            skLineSegment(sketch, "E918", {"start": v(-90.94, -29.83) * mm, "end": v(-90.32, -29.9) * mm});
            skLineSegment(sketch, "E919", {"start": v(-89.85, -31.45) * mm, "end": v(-89.23, -31.52) * mm});
            skLineSegment(sketch, "E920", {"start": v(-90.32, -29.9) * mm, "end": v(-89.7, -29.96) * mm});
            skLineSegment(sketch, "E921", {"start": v(-89.23, -31.52) * mm, "end": v(-88.6, -31.58) * mm});
            skLineSegment(sketch, "E922", {"start": v(-89.7, -29.96) * mm, "end": v(-89.07, -30.03) * mm});
            skLineSegment(sketch, "E923", {"start": v(-88.6, -31.58) * mm, "end": v(-87.96, -31.65) * mm});
            skLineSegment(sketch, "E924", {"start": v(-89.07, -30.03) * mm, "end": v(-88.45, -30.09) * mm});
            skLineSegment(sketch, "E925", {"start": v(-87.96, -31.65) * mm, "end": v(-87.32, -31.7) * mm});
            skLineSegment(sketch, "E926", {"start": v(-88.45, -30.09) * mm, "end": v(-87.82, -30.15) * mm});
            skLineSegment(sketch, "E927", {"start": v(-87.32, -31.7) * mm, "end": v(-86.69, -31.77) * mm});
            skLineSegment(sketch, "E928", {"start": v(-87.82, -30.15) * mm, "end": v(-87.19, -30.21) * mm});
            skLineSegment(sketch, "E929", {"start": v(-86.69, -31.77) * mm, "end": v(-86.05, -31.82) * mm});
            skLineSegment(sketch, "E930", {"start": v(-87.19, -30.21) * mm, "end": v(-86.55, -30.27) * mm});
            skLineSegment(sketch, "E931", {"start": v(-86.05, -31.82) * mm, "end": v(-85.4, -31.88) * mm});
            skLineSegment(sketch, "E932", {"start": v(-86.55, -30.27) * mm, "end": v(-85.91, -30.33) * mm});
            skLineSegment(sketch, "E933", {"start": v(-85.4, -31.88) * mm, "end": v(-84.76, -31.94) * mm});
            skLineSegment(sketch, "E934", {"start": v(-85.91, -30.33) * mm, "end": v(-85.28, -30.39) * mm});
            skLineSegment(sketch, "E935", {"start": v(-84.76, -31.94) * mm, "end": v(-84.1, -31.99) * mm});
            skLineSegment(sketch, "E936", {"start": v(-85.28, -30.39) * mm, "end": v(-84.63, -30.44) * mm});
            skLineSegment(sketch, "E937", {"start": v(-84.1, -31.99) * mm, "end": v(-83.46, -32.04) * mm});
            skLineSegment(sketch, "E938", {"start": v(-84.63, -30.44) * mm, "end": v(-84, -30.5) * mm});
            skLineSegment(sketch, "E939", {"start": v(-83.46, -32.04) * mm, "end": v(-82.8, -32.1) * mm});
            skLineSegment(sketch, "E940", {"start": v(-84, -30.5) * mm, "end": v(-83.34, -30.55) * mm});
            skLineSegment(sketch, "E941", {"start": v(-82.8, -32.1) * mm, "end": v(-82.15, -32.14) * mm});
            skLineSegment(sketch, "E942", {"start": v(-83.34, -30.55) * mm, "end": v(-82.7, -30.6) * mm});
            skLineSegment(sketch, "E943", {"start": v(-82.15, -32.14) * mm, "end": v(-81.5, -32.19) * mm});
            skLineSegment(sketch, "E944", {"start": v(-82.7, -30.6) * mm, "end": v(-82.04, -30.64) * mm});
            skLineSegment(sketch, "E945", {"start": v(-81.5, -32.19) * mm, "end": v(-80.84, -32.23) * mm});
            skLineSegment(sketch, "E946", {"start": v(-82.04, -30.64) * mm, "end": v(-81.4, -30.7) * mm});
            skLineSegment(sketch, "E947", {"start": v(-80.84, -32.23) * mm, "end": v(-80.18, -32.28) * mm});
            skLineSegment(sketch, "E948", {"start": v(-81.4, -30.7) * mm, "end": v(-80.74, -30.74) * mm});
            skLineSegment(sketch, "E949", {"start": v(-80.18, -32.28) * mm, "end": v(-79.51, -32.32) * mm});
            skLineSegment(sketch, "E950", {"start": v(-80.74, -30.74) * mm, "end": v(-80.08, -30.78) * mm});
            skLineSegment(sketch, "E951", {"start": v(-79.51, -32.32) * mm, "end": v(-78.85, -32.36) * mm});
            skLineSegment(sketch, "E952", {"start": v(-80.08, -30.78) * mm, "end": v(-79.42, -30.82) * mm});
            skLineSegment(sketch, "E953", {"start": v(-78.85, -32.36) * mm, "end": v(-78.18, -32.4) * mm});
            skLineSegment(sketch, "E954", {"start": v(-79.42, -30.82) * mm, "end": v(-78.76, -30.87) * mm});
            skLineSegment(sketch, "E955", {"start": v(-78.18, -32.4) * mm, "end": v(-77.5, -32.44) * mm});
            skLineSegment(sketch, "E956", {"start": v(-78.76, -30.87) * mm, "end": v(-78.1, -30.9) * mm});
            skLineSegment(sketch, "E957", {"start": v(-77.5, -32.44) * mm, "end": v(-76.84, -32.48) * mm});
            skLineSegment(sketch, "E958", {"start": v(-78.1, -30.9) * mm, "end": v(-77.43, -30.94) * mm});
            skLineSegment(sketch, "E959", {"start": v(-76.84, -32.48) * mm, "end": v(-76.16, -32.51) * mm});
            skLineSegment(sketch, "E960", {"start": v(-77.43, -30.94) * mm, "end": v(-76.76, -30.98) * mm});
            skLineSegment(sketch, "E961", {"start": v(-76.16, -32.51) * mm, "end": v(-75.49, -32.55) * mm});
            skLineSegment(sketch, "E962", {"start": v(-76.76, -30.98) * mm, "end": v(-76.09, -31.01) * mm});
            skLineSegment(sketch, "E963", {"start": v(-75.49, -32.55) * mm, "end": v(-74.8, -32.58) * mm});
            skLineSegment(sketch, "E964", {"start": v(-76.09, -31.01) * mm, "end": v(-75.42, -31.05) * mm});
            skLineSegment(sketch, "E965", {"start": v(-74.8, -32.58) * mm, "end": v(-74.13, -32.6) * mm});
            skLineSegment(sketch, "E966", {"start": v(-75.42, -31.05) * mm, "end": v(-74.74, -31.08) * mm});
            skLineSegment(sketch, "E967", {"start": v(-74.13, -32.6) * mm, "end": v(-73.45, -32.64) * mm});
            skLineSegment(sketch, "E968", {"start": v(-74.74, -31.08) * mm, "end": v(-74.06, -31.11) * mm});
            skLineSegment(sketch, "E969", {"start": v(-73.45, -32.64) * mm, "end": v(-72.76, -32.67) * mm});
            skLineSegment(sketch, "E970", {"start": v(-74.06, -31.11) * mm, "end": v(-73.38, -31.14) * mm});
            skLineSegment(sketch, "E971", {"start": v(-72.76, -32.67) * mm, "end": v(-72.07, -32.7) * mm});
            skLineSegment(sketch, "E972", {"start": v(-73.38, -31.14) * mm, "end": v(-72.7, -31.17) * mm});
            skLineSegment(sketch, "E973", {"start": v(-72.07, -32.7) * mm, "end": v(-71.39, -32.72) * mm});
            skLineSegment(sketch, "E974", {"start": v(-72.7, -31.17) * mm, "end": v(-72.02, -31.2) * mm});
            skLineSegment(sketch, "E975", {"start": v(-71.39, -32.72) * mm, "end": v(-70.7, -32.74) * mm});
            skLineSegment(sketch, "E976", {"start": v(-72.02, -31.2) * mm, "end": v(-71.34, -31.22) * mm});
            skLineSegment(sketch, "E977", {"start": v(-70.7, -32.74) * mm, "end": v(-70, -32.76) * mm});
            skLineSegment(sketch, "E978", {"start": v(-71.34, -31.22) * mm, "end": v(-70.65, -31.24) * mm});
            skLineSegment(sketch, "E979", {"start": v(-70, -32.76) * mm, "end": v(-69.3, -32.78) * mm});
            skLineSegment(sketch, "E980", {"start": v(-70.65, -31.24) * mm, "end": v(-69.96, -31.26) * mm});
            skLineSegment(sketch, "E981", {"start": v(-69.3, -32.78) * mm, "end": v(-68.61, -32.8) * mm});
            skLineSegment(sketch, "E982", {"start": v(-69.96, -31.26) * mm, "end": v(-69.27, -31.28) * mm});
            skLineSegment(sketch, "E983", {"start": v(-68.61, -32.8) * mm, "end": v(-67.92, -32.82) * mm});
            skLineSegment(sketch, "E984", {"start": v(-69.27, -31.28) * mm, "end": v(-68.58, -31.3) * mm});
            skLineSegment(sketch, "E985", {"start": v(-67.92, -32.82) * mm, "end": v(-67.22, -32.84) * mm});
            skLineSegment(sketch, "E986", {"start": v(-68.58, -31.3) * mm, "end": v(-67.88, -31.32) * mm});
            skLineSegment(sketch, "E987", {"start": v(-67.22, -32.84) * mm, "end": v(-66.51, -32.85) * mm});
            skLineSegment(sketch, "E988", {"start": v(-67.88, -31.32) * mm, "end": v(-67.18, -31.34) * mm});
            skLineSegment(sketch, "E989", {"start": v(-66.51, -32.85) * mm, "end": v(-65.8, -32.86) * mm});
            skLineSegment(sketch, "E990", {"start": v(-67.18, -31.34) * mm, "end": v(-66.49, -31.35) * mm});
            skLineSegment(sketch, "E991", {"start": v(-65.8, -32.86) * mm, "end": v(-65.1, -32.87) * mm});
            skLineSegment(sketch, "E992", {"start": v(-66.49, -31.35) * mm, "end": v(-65.79, -31.36) * mm});
            skLineSegment(sketch, "E993", {"start": v(-65.1, -32.87) * mm, "end": v(-64.4, -32.88) * mm});
            skLineSegment(sketch, "E994", {"start": v(-65.79, -31.36) * mm, "end": v(-65.08, -31.37) * mm});
            skLineSegment(sketch, "E995", {"start": v(-64.4, -32.88) * mm, "end": v(-63.69, -32.9) * mm});
            skLineSegment(sketch, "E996", {"start": v(-65.08, -31.37) * mm, "end": v(-64.38, -31.38) * mm});
            skLineSegment(sketch, "E997", {"start": v(-63.69, -32.9) * mm, "end": v(-62.98, -32.9) * mm});
            skLineSegment(sketch, "E998", {"start": v(-64.38, -31.38) * mm, "end": v(-63.67, -31.4) * mm});
            skLineSegment(sketch, "E999", {"start": v(-62.98, -32.9) * mm, "end": v(-62.27, -32.9) * mm});
            skLineSegment(sketch, "E1000", {"start": v(-63.67, -31.4) * mm, "end": v(-62.97, -31.4) * mm});
            skLineSegment(sketch, "E1001", {"start": v(-62.27, -32.9) * mm, "end": v(-61.55, -32.9) * mm});
            skLineSegment(sketch, "E1002", {"start": v(-62.97, -31.4) * mm, "end": v(-62.26, -31.4) * mm});
            skLineSegment(sketch, "E1003", {"start": v(-61.55, -32.9) * mm, "end": v(-60.84, -32.91) * mm});
            skLineSegment(sketch, "E1004", {"start": v(-62.26, -31.4) * mm, "end": v(-61.55, -31.4) * mm});
            skLineSegment(sketch, "E1005", {"start": v(-60.84, -32.91) * mm, "end": v(-60.12, -32.91) * mm});
            skLineSegment(sketch, "E1006", {"start": v(-61.55, -31.4) * mm, "end": v(-60.83, -31.41) * mm});
            skLineSegment(sketch, "E1007", {"start": v(-60.12, -32.91) * mm, "end": v(-59.4, -32.91) * mm});
            skLineSegment(sketch, "E1008", {"start": v(-60.83, -31.41) * mm, "end": v(-60.12, -31.41) * mm});
            skLineSegment(sketch, "E1009", {"start": v(-59.4, -32.91) * mm, "end": v(-58.68, -32.91) * mm});
            skLineSegment(sketch, "E1010", {"start": v(-60.12, -31.41) * mm, "end": v(-59.4, -31.41) * mm});
            skLineSegment(sketch, "E1011", {"start": v(-58.68, -32.91) * mm, "end": v(-57.96, -32.9) * mm});
            skLineSegment(sketch, "E1012", {"start": v(-59.4, -31.41) * mm, "end": v(-58.67, -31.41) * mm});
            skLineSegment(sketch, "E1013", {"start": v(-57.96, -32.9) * mm, "end": v(-57.23, -32.9) * mm});
            skLineSegment(sketch, "E1014", {"start": v(-58.67, -31.41) * mm, "end": v(-57.95, -31.4) * mm});
            skLineSegment(sketch, "E1015", {"start": v(-57.23, -32.9) * mm, "end": v(-56.5, -32.9) * mm});
            skLineSegment(sketch, "E1016", {"start": v(-57.95, -31.4) * mm, "end": v(-57.22, -31.4) * mm});
            skLineSegment(sketch, "E1017", {"start": v(-56.5, -32.9) * mm, "end": v(-55.78, -32.9) * mm});
            skLineSegment(sketch, "E1018", {"start": v(-57.22, -31.4) * mm, "end": v(-56.5, -31.4) * mm});
            skLineSegment(sketch, "E1019", {"start": v(-55.78, -32.9) * mm, "end": v(-55.05, -32.88) * mm});
            skLineSegment(sketch, "E1020", {"start": v(-56.5, -31.4) * mm, "end": v(-55.76, -31.4) * mm});
            skLineSegment(sketch, "E1021", {"start": v(-55.05, -32.88) * mm, "end": v(-54.32, -32.87) * mm});
            skLineSegment(sketch, "E1022", {"start": v(-55.76, -31.4) * mm, "end": v(-55.03, -31.38) * mm});
            skLineSegment(sketch, "E1023", {"start": v(-54.32, -32.87) * mm, "end": v(-53.59, -32.86) * mm});
            skLineSegment(sketch, "E1024", {"start": v(-55.03, -31.38) * mm, "end": v(-54.3, -31.37) * mm});
            skLineSegment(sketch, "E1025", {"start": v(-53.59, -32.86) * mm, "end": v(-52.86, -32.85) * mm});
            skLineSegment(sketch, "E1026", {"start": v(-54.3, -31.37) * mm, "end": v(-53.56, -31.36) * mm});
            skLineSegment(sketch, "E1027", {"start": v(-52.86, -32.85) * mm, "end": v(-52.12, -32.84) * mm});
            skLineSegment(sketch, "E1028", {"start": v(-53.56, -31.36) * mm, "end": v(-52.83, -31.35) * mm});
            skLineSegment(sketch, "E1029", {"start": v(-52.12, -32.84) * mm, "end": v(-51.39, -32.82) * mm});
            skLineSegment(sketch, "E1030", {"start": v(-52.83, -31.35) * mm, "end": v(-52.1, -31.34) * mm});
            skLineSegment(sketch, "E1031", {"start": v(-51.39, -32.82) * mm, "end": v(-50.65, -32.8) * mm});
            skLineSegment(sketch, "E1032", {"start": v(-52.1, -31.34) * mm, "end": v(-51.35, -31.32) * mm});
            skLineSegment(sketch, "E1033", {"start": v(-50.65, -32.8) * mm, "end": v(-49.9, -32.79) * mm});
            skLineSegment(sketch, "E1034", {"start": v(-51.35, -31.32) * mm, "end": v(-50.61, -31.3) * mm});
            skLineSegment(sketch, "E1035", {"start": v(-49.9, -32.79) * mm, "end": v(-49.17, -32.77) * mm});
            skLineSegment(sketch, "E1036", {"start": v(-50.61, -31.3) * mm, "end": v(-49.87, -31.29) * mm});
            skLineSegment(sketch, "E1037", {"start": v(-49.17, -32.77) * mm, "end": v(-48.43, -32.75) * mm});
            skLineSegment(sketch, "E1038", {"start": v(-49.87, -31.29) * mm, "end": v(-49.13, -31.27) * mm});
            skLineSegment(sketch, "E1039", {"start": v(-48.43, -32.75) * mm, "end": v(-47.69, -32.72) * mm});
            skLineSegment(sketch, "E1040", {"start": v(-49.13, -31.27) * mm, "end": v(-48.38, -31.25) * mm});
            skLineSegment(sketch, "E1041", {"start": v(-47.69, -32.72) * mm, "end": v(-46.94, -32.7) * mm});
            skLineSegment(sketch, "E1042", {"start": v(-48.38, -31.25) * mm, "end": v(-47.64, -31.22) * mm});
            skLineSegment(sketch, "E1043", {"start": v(-46.94, -32.7) * mm, "end": v(-46.2, -32.68) * mm});
            skLineSegment(sketch, "E1044", {"start": v(-47.64, -31.22) * mm, "end": v(-46.9, -31.2) * mm});
            skLineSegment(sketch, "E1045", {"start": v(-46.2, -32.68) * mm, "end": v(-45.45, -32.65) * mm});
            skLineSegment(sketch, "E1046", {"start": v(-46.9, -31.2) * mm, "end": v(-46.14, -31.18) * mm});
            skLineSegment(sketch, "E1047", {"start": v(-45.45, -32.65) * mm, "end": v(-44.7, -32.62) * mm});
            skLineSegment(sketch, "E1048", {"start": v(-46.14, -31.18) * mm, "end": v(-45.4, -31.15) * mm});
            skLineSegment(sketch, "E1049", {"start": v(-44.7, -32.62) * mm, "end": v(-43.95, -32.6) * mm});
            skLineSegment(sketch, "E1050", {"start": v(-45.4, -31.15) * mm, "end": v(-44.64, -31.12) * mm});
            skLineSegment(sketch, "E1051", {"start": v(-43.95, -32.6) * mm, "end": v(-43.2, -32.56) * mm});
            skLineSegment(sketch, "E1052", {"start": v(-44.64, -31.12) * mm, "end": v(-43.9, -31.1) * mm});
            skLineSegment(sketch, "E1053", {"start": v(-43.2, -32.56) * mm, "end": v(-42.45, -32.53) * mm});
            skLineSegment(sketch, "E1054", {"start": v(-43.9, -31.1) * mm, "end": v(-43.14, -31.06) * mm});
            skLineSegment(sketch, "E1055", {"start": v(-42.45, -32.53) * mm, "end": v(-41.7, -32.5) * mm});
            skLineSegment(sketch, "E1056", {"start": v(-43.14, -31.06) * mm, "end": v(-42.39, -31.03) * mm});
            skLineSegment(sketch, "E1057", {"start": v(-41.7, -32.5) * mm, "end": v(-40.94, -32.47) * mm});
            skLineSegment(sketch, "E1058", {"start": v(-42.39, -31.03) * mm, "end": v(-41.63, -31) * mm});
            skLineSegment(sketch, "E1059", {"start": v(-40.94, -32.47) * mm, "end": v(-40.19, -32.43) * mm});
            skLineSegment(sketch, "E1060", {"start": v(-41.63, -31) * mm, "end": v(-40.87, -30.97) * mm});
            skLineSegment(sketch, "E1061", {"start": v(-40.19, -32.43) * mm, "end": v(-39.43, -32.4) * mm});
            skLineSegment(sketch, "E1062", {"start": v(-40.87, -30.97) * mm, "end": v(-40.12, -30.93) * mm});
            skLineSegment(sketch, "E1063", {"start": v(-39.43, -32.4) * mm, "end": v(-38.68, -32.36) * mm});
            skLineSegment(sketch, "E1064", {"start": v(-40.12, -30.93) * mm, "end": v(-39.36, -30.9) * mm});
            skLineSegment(sketch, "E1065", {"start": v(-38.68, -32.36) * mm, "end": v(-37.92, -32.32) * mm});
            skLineSegment(sketch, "E1066", {"start": v(-39.36, -30.9) * mm, "end": v(-38.6, -30.86) * mm});
            skLineSegment(sketch, "E1067", {"start": v(-37.92, -32.32) * mm, "end": v(-37.16, -32.28) * mm});
            skLineSegment(sketch, "E1068", {"start": v(-38.6, -30.86) * mm, "end": v(-37.84, -30.82) * mm});
            skLineSegment(sketch, "E1069", {"start": v(-37.16, -32.28) * mm, "end": v(-36.4, -32.24) * mm});
            skLineSegment(sketch, "E1070", {"start": v(-37.84, -30.82) * mm, "end": v(-37.08, -30.78) * mm});
            skLineSegment(sketch, "E1071", {"start": v(-36.4, -32.24) * mm, "end": v(-35.64, -32.2) * mm});
            skLineSegment(sketch, "E1072", {"start": v(-37.08, -30.78) * mm, "end": v(-36.31, -30.74) * mm});
            skLineSegment(sketch, "E1073", {"start": v(-35.64, -32.2) * mm, "end": v(-34.87, -32.15) * mm});
            skLineSegment(sketch, "E1074", {"start": v(-36.31, -30.74) * mm, "end": v(-35.55, -30.7) * mm});
            skLineSegment(sketch, "E1075", {"start": v(-34.87, -32.15) * mm, "end": v(-34.11, -32.1) * mm});
            skLineSegment(sketch, "E1076", {"start": v(-35.55, -30.7) * mm, "end": v(-34.79, -30.65) * mm});
            skLineSegment(sketch, "E1077", {"start": v(-34.11, -32.1) * mm, "end": v(-33.35, -32.06) * mm});
            skLineSegment(sketch, "E1078", {"start": v(-34.79, -30.65) * mm, "end": v(-34.02, -30.6) * mm});
            skLineSegment(sketch, "E1079", {"start": v(-33.35, -32.06) * mm, "end": v(-32.58, -32.01) * mm});
            skLineSegment(sketch, "E1080", {"start": v(-34.02, -30.6) * mm, "end": v(-33.25, -30.56) * mm});
            skLineSegment(sketch, "E1081", {"start": v(-32.58, -32.01) * mm, "end": v(-31.82, -31.96) * mm});
            skLineSegment(sketch, "E1082", {"start": v(-33.25, -30.56) * mm, "end": v(-32.49, -30.51) * mm});
            skLineSegment(sketch, "E1083", {"start": v(-31.82, -31.96) * mm, "end": v(-31.05, -31.91) * mm});
            skLineSegment(sketch, "E1084", {"start": v(-32.49, -30.51) * mm, "end": v(-31.72, -30.47) * mm});
            skLineSegment(sketch, "E1085", {"start": v(-31.05, -31.91) * mm, "end": v(-30.28, -31.86) * mm});
            skLineSegment(sketch, "E1086", {"start": v(-31.72, -30.47) * mm, "end": v(-30.95, -30.42) * mm});
            skLineSegment(sketch, "E1087", {"start": v(-30.28, -31.86) * mm, "end": v(-29.51, -31.8) * mm});
            skLineSegment(sketch, "E1088", {"start": v(-30.95, -30.42) * mm, "end": v(-30.18, -30.37) * mm});
            skLineSegment(sketch, "E1089", {"start": v(-29.51, -31.8) * mm, "end": v(-28.74, -31.76) * mm});
            skLineSegment(sketch, "E1090", {"start": v(-30.18, -30.37) * mm, "end": v(-29.4, -30.31) * mm});
            skLineSegment(sketch, "E1091", {"start": v(-28.74, -31.76) * mm, "end": v(-27.97, -31.7) * mm});
            skLineSegment(sketch, "E1092", {"start": v(-29.4, -30.31) * mm, "end": v(-28.64, -30.26) * mm});
            skLineSegment(sketch, "E1093", {"start": v(-27.97, -31.7) * mm, "end": v(-27.2, -31.65) * mm});
            skLineSegment(sketch, "E1094", {"start": v(-28.64, -30.26) * mm, "end": v(-27.87, -30.2) * mm});
            skLineSegment(sketch, "E1095", {"start": v(-27.2, -31.65) * mm, "end": v(-26.43, -31.59) * mm});
            skLineSegment(sketch, "E1096", {"start": v(-27.87, -30.2) * mm, "end": v(-27.1, -30.15) * mm});
            skLineSegment(sketch, "E1097", {"start": v(-26.43, -31.59) * mm, "end": v(-25.66, -31.53) * mm});
            skLineSegment(sketch, "E1098", {"start": v(-27.1, -30.15) * mm, "end": v(-26.32, -30.1) * mm});
            skLineSegment(sketch, "E1099", {"start": v(-25.66, -31.53) * mm, "end": v(-24.89, -31.47) * mm});
            skLineSegment(sketch, "E1100", {"start": v(-26.32, -30.1) * mm, "end": v(-25.55, -30.04) * mm});
            skLineSegment(sketch, "E1101", {"start": v(-24.89, -31.47) * mm, "end": v(-24.11, -31.41) * mm});
            skLineSegment(sketch, "E1102", {"start": v(-25.55, -30.04) * mm, "end": v(-24.77, -29.98) * mm});
            skLineSegment(sketch, "E1103", {"start": v(-24.11, -31.41) * mm, "end": v(-23.34, -31.35) * mm});
            skLineSegment(sketch, "E1104", {"start": v(-24.77, -29.98) * mm, "end": v(-24, -29.92) * mm});
            skLineSegment(sketch, "E1105", {"start": v(-23.34, -31.35) * mm, "end": v(-22.56, -31.29) * mm});
            skLineSegment(sketch, "E1106", {"start": v(-24, -29.92) * mm, "end": v(-23.22, -29.86) * mm});
            skLineSegment(sketch, "E1107", {"start": v(-22.56, -31.29) * mm, "end": v(-21.79, -31.23) * mm});
            skLineSegment(sketch, "E1108", {"start": v(-23.22, -29.86) * mm, "end": v(-22.44, -29.8) * mm});
            skLineSegment(sketch, "E1109", {"start": v(-21.79, -31.23) * mm, "end": v(-21.01, -31.16) * mm});
            skLineSegment(sketch, "E1110", {"start": v(-22.44, -29.8) * mm, "end": v(-21.66, -29.73) * mm});
            skLineSegment(sketch, "E1111", {"start": v(-21.01, -31.16) * mm, "end": v(-20.23, -31.1) * mm});
            skLineSegment(sketch, "E1112", {"start": v(-21.66, -29.73) * mm, "end": v(-20.89, -29.67) * mm});
            skLineSegment(sketch, "E1113", {"start": v(-20.23, -31.1) * mm, "end": v(-19.46, -31.03) * mm});
            skLineSegment(sketch, "E1114", {"start": v(-20.89, -29.67) * mm, "end": v(-20.1, -29.6) * mm});
            skLineSegment(sketch, "E1115", {"start": v(-19.46, -31.03) * mm, "end": v(-18.68, -30.96) * mm});
            skLineSegment(sketch, "E1116", {"start": v(-20.1, -29.6) * mm, "end": v(-19.33, -29.54) * mm});
            skLineSegment(sketch, "E1117", {"start": v(-18.68, -30.96) * mm, "end": v(-17.9, -30.9) * mm});
            skLineSegment(sketch, "E1118", {"start": v(-19.33, -29.54) * mm, "end": v(-18.55, -29.47) * mm});
            skLineSegment(sketch, "E1119", {"start": v(-17.9, -30.9) * mm, "end": v(-17.12, -30.82) * mm});
            skLineSegment(sketch, "E1120", {"start": v(-18.55, -29.47) * mm, "end": v(-17.77, -29.4) * mm});
            skLineSegment(sketch, "E1121", {"start": v(-17.12, -30.82) * mm, "end": v(-16.34, -30.75) * mm});
            skLineSegment(sketch, "E1122", {"start": v(-17.77, -29.4) * mm, "end": v(-16.99, -29.33) * mm});
            skLineSegment(sketch, "E1123", {"start": v(-16.34, -30.75) * mm, "end": v(-15.56, -30.68) * mm});
            skLineSegment(sketch, "E1124", {"start": v(-16.99, -29.33) * mm, "end": v(-16.2, -29.26) * mm});
            skLineSegment(sketch, "E1125", {"start": v(-15.56, -30.68) * mm, "end": v(-14.78, -30.6) * mm});
            skLineSegment(sketch, "E1126", {"start": v(-16.2, -29.26) * mm, "end": v(-15.42, -29.19) * mm});
            skLineSegment(sketch, "E1127", {"start": v(-14.78, -30.6) * mm, "end": v(-14, -30.54) * mm});
            skLineSegment(sketch, "E1128", {"start": v(-15.42, -29.19) * mm, "end": v(-14.64, -29.12) * mm});
            skLineSegment(sketch, "E1129", {"start": v(-14, -30.54) * mm, "end": v(-13.22, -30.46) * mm});
            skLineSegment(sketch, "E1130", {"start": v(-14.64, -29.12) * mm, "end": v(-13.86, -29.04) * mm});
            skLineSegment(sketch, "E1131", {"start": v(-13.22, -30.46) * mm, "end": v(-12.44, -30.39) * mm});
            skLineSegment(sketch, "E1132", {"start": v(-13.86, -29.04) * mm, "end": v(-13.08, -28.97) * mm});
            skLineSegment(sketch, "E1133", {"start": v(-12.44, -30.39) * mm, "end": v(-11.66, -30.3) * mm});
            skLineSegment(sketch, "E1134", {"start": v(-13.08, -28.97) * mm, "end": v(-12.3, -28.9) * mm});
            skLineSegment(sketch, "E1135", {"start": v(-11.66, -30.3) * mm, "end": v(-10.88, -30.23) * mm});
            skLineSegment(sketch, "E1136", {"start": v(-12.3, -28.9) * mm, "end": v(-11.5, -28.82) * mm});
            skLineSegment(sketch, "E1137", {"start": v(-10.88, -30.23) * mm, "end": v(-10.1, -30.15) * mm});
            skLineSegment(sketch, "E1138", {"start": v(-11.5, -28.82) * mm, "end": v(-10.73, -28.74) * mm});
            skLineSegment(sketch, "E1139", {"start": v(-10.1, -30.15) * mm, "end": v(-9.31, -30.07) * mm});
            skLineSegment(sketch, "E1140", {"start": v(-10.73, -28.74) * mm, "end": v(-9.94, -28.66) * mm});
            skLineSegment(sketch, "E1141", {"start": v(-9.31, -30.07) * mm, "end": v(-8.53, -30) * mm});
            skLineSegment(sketch, "E1142", {"start": v(-9.94, -28.66) * mm, "end": v(-9.16, -28.58) * mm});
            skLineSegment(sketch, "E1143", {"start": v(-8.53, -30) * mm, "end": v(-7.74, -29.91) * mm});
            skLineSegment(sketch, "E1144", {"start": v(-9.16, -28.58) * mm, "end": v(-8.37, -28.5) * mm});
            skLineSegment(sketch, "E1145", {"start": v(-7.74, -29.91) * mm, "end": v(-6.96, -29.83) * mm});
            skLineSegment(sketch, "E1146", {"start": v(-8.37, -28.5) * mm, "end": v(-7.59, -28.42) * mm});
            skLineSegment(sketch, "E1147", {"start": v(-6.96, -29.83) * mm, "end": v(-6.18, -29.75) * mm});
            skLineSegment(sketch, "E1148", {"start": v(-7.59, -28.42) * mm, "end": v(-6.8, -28.34) * mm});
            skLineSegment(sketch, "E1149", {"start": v(-6.18, -29.75) * mm, "end": v(-5.4, -29.66) * mm});
            skLineSegment(sketch, "E1150", {"start": v(-6.8, -28.34) * mm, "end": v(-6.02, -28.26) * mm});
            skLineSegment(sketch, "E1151", {"start": v(-5.4, -29.66) * mm, "end": v(-4.61, -29.58) * mm});
            skLineSegment(sketch, "E1152", {"start": v(-6.02, -28.26) * mm, "end": v(-5.23, -28.17) * mm});
            skLineSegment(sketch, "E1153", {"start": v(-4.61, -29.58) * mm, "end": v(-3.83, -29.5) * mm});
            skLineSegment(sketch, "E1154", {"start": v(-5.23, -28.17) * mm, "end": v(-4.45, -28.09) * mm});
            skLineSegment(sketch, "E1155", {"start": v(-3.83, -29.5) * mm, "end": v(-3.04, -29.4) * mm});
            skLineSegment(sketch, "E1156", {"start": v(-4.45, -28.09) * mm, "end": v(-3.66, -28) * mm});
            skLineSegment(sketch, "E1157", {"start": v(-3.04, -29.4) * mm, "end": v(-2.26, -29.32) * mm});
            skLineSegment(sketch, "E1158", {"start": v(-3.66, -28) * mm, "end": v(-2.88, -27.92) * mm});
            skLineSegment(sketch, "E1159", {"start": v(-2.26, -29.32) * mm, "end": v(-1.47, -29.23) * mm});
            skLineSegment(sketch, "E1160", {"start": v(-2.88, -27.92) * mm, "end": v(-2.1, -27.83) * mm});
            skLineSegment(sketch, "E1161", {"start": v(-1.47, -29.23) * mm, "end": v(-0.69, -29.14) * mm});
            skLineSegment(sketch, "E1162", {"start": v(-2.1, -27.83) * mm, "end": v(-1.3, -27.74) * mm});
            skLineSegment(sketch, "E1163", {"start": v(-0.69, -29.14) * mm, "end": v(0.1, -29.05) * mm});
            skLineSegment(sketch, "E1164", {"start": v(-1.3, -27.74) * mm, "end": v(-0.52, -27.65) * mm});
            skLineSegment(sketch, "E1165", {"start": v(0.1, -29.05) * mm, "end": v(0.88, -28.96) * mm});
            skLineSegment(sketch, "E1166", {"start": v(-0.52, -27.65) * mm, "end": v(0.27, -27.56) * mm});
            skLineSegment(sketch, "E1167", {"start": v(0.88, -28.96) * mm, "end": v(1.66, -28.87) * mm});
            skLineSegment(sketch, "E1168", {"start": v(0.27, -27.56) * mm, "end": v(1.05, -27.47) * mm});
            skLineSegment(sketch, "E1169", {"start": v(1.66, -28.87) * mm, "end": v(2.45, -28.78) * mm});
            skLineSegment(sketch, "E1170", {"start": v(1.05, -27.47) * mm, "end": v(1.84, -27.38) * mm});
            skLineSegment(sketch, "E1171", {"start": v(2.45, -28.78) * mm, "end": v(3.23, -28.68) * mm});
            skLineSegment(sketch, "E1172", {"start": v(1.84, -27.38) * mm, "end": v(2.62, -27.29) * mm});
            skLineSegment(sketch, "E1173", {"start": v(3.23, -28.68) * mm, "end": v(4.02, -28.59) * mm});
            skLineSegment(sketch, "E1174", {"start": v(2.62, -27.29) * mm, "end": v(3.41, -27.2) * mm});
            skLineSegment(sketch, "E1175", {"start": v(4.02, -28.59) * mm, "end": v(4.8, -28.5) * mm});
            skLineSegment(sketch, "E1176", {"start": v(3.41, -27.2) * mm, "end": v(4.2, -27.1) * mm});
            skLineSegment(sketch, "E1177", {"start": v(4.8, -28.5) * mm, "end": v(5.58, -28.4) * mm});
            skLineSegment(sketch, "E1178", {"start": v(4.2, -27.1) * mm, "end": v(4.98, -27) * mm});
            skLineSegment(sketch, "E1179", {"start": v(5.58, -28.4) * mm, "end": v(6.37, -28.3) * mm});
            skLineSegment(sketch, "E1180", {"start": v(4.98, -27) * mm, "end": v(5.77, -26.9) * mm});
            skLineSegment(sketch, "E1181", {"start": v(6.37, -28.3) * mm, "end": v(7.15, -28.2) * mm});
            skLineSegment(sketch, "E1182", {"start": v(5.77, -26.9) * mm, "end": v(6.55, -26.81) * mm});
            skLineSegment(sketch, "E1183", {"start": v(7.15, -28.2) * mm, "end": v(7.93, -28.1) * mm});
            skLineSegment(sketch, "E1184", {"start": v(6.55, -26.81) * mm, "end": v(7.34, -26.72) * mm});
            skLineSegment(sketch, "E1185", {"start": v(7.93, -28.1) * mm, "end": v(8.72, -28) * mm});
            skLineSegment(sketch, "E1186", {"start": v(7.34, -26.72) * mm, "end": v(8.12, -26.62) * mm});
            skLineSegment(sketch, "E1187", {"start": v(8.72, -28) * mm, "end": v(9.5, -27.9) * mm});
            skLineSegment(sketch, "E1188", {"start": v(8.12, -26.62) * mm, "end": v(8.9, -26.52) * mm});
            skLineSegment(sketch, "E1189", {"start": v(9.5, -27.9) * mm, "end": v(10.28, -27.8) * mm});
            skLineSegment(sketch, "E1190", {"start": v(8.9, -26.52) * mm, "end": v(9.69, -26.42) * mm});
            skLineSegment(sketch, "E1191", {"start": v(10.28, -27.8) * mm, "end": v(11.06, -27.7) * mm});
            skLineSegment(sketch, "E1192", {"start": v(9.69, -26.42) * mm, "end": v(10.47, -26.32) * mm});
            skLineSegment(sketch, "E1193", {"start": v(11.06, -27.7) * mm, "end": v(11.85, -27.6) * mm});
            skLineSegment(sketch, "E1194", {"start": v(10.47, -26.32) * mm, "end": v(11.26, -26.22) * mm});
            skLineSegment(sketch, "E1195", {"start": v(11.85, -27.6) * mm, "end": v(12.63, -27.5) * mm});
            skLineSegment(sketch, "E1196", {"start": v(11.26, -26.22) * mm, "end": v(12.04, -26.12) * mm});
            skLineSegment(sketch, "E1197", {"start": v(12.63, -27.5) * mm, "end": v(13.4, -27.4) * mm});
            skLineSegment(sketch, "E1198", {"start": v(12.04, -26.12) * mm, "end": v(12.82, -26.02) * mm});
            skLineSegment(sketch, "E1199", {"start": v(13.4, -27.4) * mm, "end": v(14.2, -27.3) * mm});
            skLineSegment(sketch, "E1200", {"start": v(12.82, -26.02) * mm, "end": v(13.6, -25.92) * mm});
            skLineSegment(sketch, "E1201", {"start": v(14.2, -27.3) * mm, "end": v(14.97, -27.2) * mm});
            skLineSegment(sketch, "E1202", {"start": v(13.6, -25.92) * mm, "end": v(14.39, -25.81) * mm});
            skLineSegment(sketch, "E1203", {"start": v(14.97, -27.2) * mm, "end": v(15.75, -27.1) * mm});
            skLineSegment(sketch, "E1204", {"start": v(14.39, -25.81) * mm, "end": v(15.17, -25.7) * mm});
            skLineSegment(sketch, "E1205", {"start": v(15.75, -27.1) * mm, "end": v(16.53, -26.98) * mm});
            skLineSegment(sketch, "E1206", {"start": v(15.17, -25.7) * mm, "end": v(15.95, -25.6) * mm});
            skLineSegment(sketch, "E1207", {"start": v(16.53, -26.98) * mm, "end": v(17.31, -26.88) * mm});
            skLineSegment(sketch, "E1208", {"start": v(15.95, -25.6) * mm, "end": v(16.73, -25.5) * mm});
            skLineSegment(sketch, "E1209", {"start": v(17.31, -26.88) * mm, "end": v(18.09, -26.77) * mm});
            skLineSegment(sketch, "E1210", {"start": v(16.73, -25.5) * mm, "end": v(17.51, -25.4) * mm});
            skLineSegment(sketch, "E1211", {"start": v(18.09, -26.77) * mm, "end": v(18.87, -26.66) * mm});
            skLineSegment(sketch, "E1212", {"start": v(17.51, -25.4) * mm, "end": v(18.3, -25.29) * mm});
            skLineSegment(sketch, "E1213", {"start": v(18.87, -26.66) * mm, "end": v(19.64, -26.56) * mm});
            skLineSegment(sketch, "E1214", {"start": v(18.3, -25.29) * mm, "end": v(19.07, -25.18) * mm});
            skLineSegment(sketch, "E1215", {"start": v(19.64, -26.56) * mm, "end": v(20.42, -26.45) * mm});
            skLineSegment(sketch, "E1216", {"start": v(19.07, -25.18) * mm, "end": v(19.85, -25.07) * mm});
            skLineSegment(sketch, "E1217", {"start": v(20.42, -26.45) * mm, "end": v(21.2, -26.34) * mm});
            skLineSegment(sketch, "E1218", {"start": v(19.85, -25.07) * mm, "end": v(20.63, -24.96) * mm});
            skLineSegment(sketch, "E1219", {"start": v(21.2, -26.34) * mm, "end": v(21.97, -26.23) * mm});
            skLineSegment(sketch, "E1220", {"start": v(20.63, -24.96) * mm, "end": v(21.4, -24.85) * mm});
            skLineSegment(sketch, "E1221", {"start": v(21.97, -26.23) * mm, "end": v(22.75, -26.12) * mm});
            skLineSegment(sketch, "E1222", {"start": v(21.4, -24.85) * mm, "end": v(22.19, -24.74) * mm});
            skLineSegment(sketch, "E1223", {"start": v(22.75, -26.12) * mm, "end": v(23.53, -26) * mm});
            skLineSegment(sketch, "E1224", {"start": v(22.19, -24.74) * mm, "end": v(22.96, -24.63) * mm});
            skLineSegment(sketch, "E1225", {"start": v(23.53, -26) * mm, "end": v(24.3, -25.9) * mm});
            skLineSegment(sketch, "E1226", {"start": v(22.96, -24.63) * mm, "end": v(23.74, -24.52) * mm});
            skLineSegment(sketch, "E1227", {"start": v(24.3, -25.9) * mm, "end": v(25.07, -25.79) * mm});
            skLineSegment(sketch, "E1228", {"start": v(23.74, -24.52) * mm, "end": v(24.51, -24.41) * mm});
            skLineSegment(sketch, "E1229", {"start": v(25.07, -25.79) * mm, "end": v(25.85, -25.67) * mm});
            skLineSegment(sketch, "E1230", {"start": v(24.51, -24.41) * mm, "end": v(25.29, -24.3) * mm});
            skLineSegment(sketch, "E1231", {"start": v(25.85, -25.67) * mm, "end": v(26.62, -25.56) * mm});
            skLineSegment(sketch, "E1232", {"start": v(25.29, -24.3) * mm, "end": v(26.06, -24.19) * mm});
            skLineSegment(sketch, "E1233", {"start": v(26.62, -25.56) * mm, "end": v(27.39, -25.45) * mm});
            skLineSegment(sketch, "E1234", {"start": v(26.06, -24.19) * mm, "end": v(26.84, -24.08) * mm});
            skLineSegment(sketch, "E1235", {"start": v(27.39, -25.45) * mm, "end": v(28.16, -25.33) * mm});
            skLineSegment(sketch, "E1236", {"start": v(26.84, -24.08) * mm, "end": v(27.6, -23.96) * mm});
            skLineSegment(sketch, "E1237", {"start": v(28.16, -25.33) * mm, "end": v(28.93, -25.22) * mm});
            skLineSegment(sketch, "E1238", {"start": v(27.6, -23.96) * mm, "end": v(28.38, -23.85) * mm});
            skLineSegment(sketch, "E1239", {"start": v(28.93, -25.22) * mm, "end": v(29.7, -25.1) * mm});
            skLineSegment(sketch, "E1240", {"start": v(28.38, -23.85) * mm, "end": v(29.15, -23.73) * mm});
            skLineSegment(sketch, "E1241", {"start": v(29.7, -25.1) * mm, "end": v(30.47, -24.99) * mm});
            skLineSegment(sketch, "E1242", {"start": v(29.15, -23.73) * mm, "end": v(29.92, -23.62) * mm});
            skLineSegment(sketch, "E1243", {"start": v(30.47, -24.99) * mm, "end": v(31.23, -24.87) * mm});
            skLineSegment(sketch, "E1244", {"start": v(29.92, -23.62) * mm, "end": v(30.7, -23.5) * mm});
            skLineSegment(sketch, "E1245", {"start": v(31.23, -24.87) * mm, "end": v(32, -24.76) * mm});
            skLineSegment(sketch, "E1246", {"start": v(30.7, -23.5) * mm, "end": v(31.46, -23.39) * mm});
            skLineSegment(sketch, "E1247", {"start": v(32, -24.76) * mm, "end": v(32.77, -24.64) * mm});
            skLineSegment(sketch, "E1248", {"start": v(31.46, -23.39) * mm, "end": v(32.23, -23.27) * mm});
            skLineSegment(sketch, "E1249", {"start": v(32.77, -24.64) * mm, "end": v(33.53, -24.52) * mm});
            skLineSegment(sketch, "E1250", {"start": v(32.23, -23.27) * mm, "end": v(33, -23.16) * mm});
            skLineSegment(sketch, "E1251", {"start": v(33.53, -24.52) * mm, "end": v(34.3, -24.4) * mm});
            skLineSegment(sketch, "E1252", {"start": v(33, -23.16) * mm, "end": v(33.76, -23.04) * mm});
            skLineSegment(sketch, "E1253", {"start": v(34.3, -24.4) * mm, "end": v(35.06, -24.29) * mm});
            skLineSegment(sketch, "E1254", {"start": v(33.76, -23.04) * mm, "end": v(34.53, -22.92) * mm});
            skLineSegment(sketch, "E1255", {"start": v(35.06, -24.29) * mm, "end": v(35.82, -24.17) * mm});
            skLineSegment(sketch, "E1256", {"start": v(34.53, -22.92) * mm, "end": v(35.29, -22.8) * mm});
            skLineSegment(sketch, "E1257", {"start": v(35.82, -24.17) * mm, "end": v(36.58, -24.05) * mm});
            skLineSegment(sketch, "E1258", {"start": v(35.29, -22.8) * mm, "end": v(36.05, -22.68) * mm});
            skLineSegment(sketch, "E1259", {"start": v(36.58, -24.05) * mm, "end": v(37.34, -23.93) * mm});
            skLineSegment(sketch, "E1260", {"start": v(36.05, -22.68) * mm, "end": v(36.81, -22.57) * mm});
            skLineSegment(sketch, "E1261", {"start": v(37.34, -23.93) * mm, "end": v(38.1, -23.8) * mm});
            skLineSegment(sketch, "E1262", {"start": v(36.81, -22.57) * mm, "end": v(37.58, -22.45) * mm});
            skLineSegment(sketch, "E1263", {"start": v(38.1, -23.8) * mm, "end": v(38.86, -23.69) * mm});
            skLineSegment(sketch, "E1264", {"start": v(37.58, -22.45) * mm, "end": v(38.34, -22.33) * mm});
            skLineSegment(sketch, "E1265", {"start": v(38.86, -23.69) * mm, "end": v(39.62, -23.57) * mm});
            skLineSegment(sketch, "E1266", {"start": v(38.34, -22.33) * mm, "end": v(39.1, -22.2) * mm});
            skLineSegment(sketch, "E1267", {"start": v(39.62, -23.57) * mm, "end": v(40.37, -23.45) * mm});
            skLineSegment(sketch, "E1268", {"start": v(39.1, -22.2) * mm, "end": v(39.85, -22.09) * mm});
            skLineSegment(sketch, "E1269", {"start": v(40.37, -23.45) * mm, "end": v(41.13, -23.33) * mm});
            skLineSegment(sketch, "E1270", {"start": v(39.85, -22.09) * mm, "end": v(40.6, -21.97) * mm});
            skLineSegment(sketch, "E1271", {"start": v(41.13, -23.33) * mm, "end": v(41.88, -23.2) * mm});
            skLineSegment(sketch, "E1272", {"start": v(40.6, -21.97) * mm, "end": v(41.36, -21.84) * mm});
            skLineSegment(sketch, "E1273", {"start": v(41.88, -23.2) * mm, "end": v(42.63, -23.08) * mm});
            skLineSegment(sketch, "E1274", {"start": v(41.36, -21.84) * mm, "end": v(42.12, -21.72) * mm});
            skLineSegment(sketch, "E1275", {"start": v(42.63, -23.08) * mm, "end": v(43.38, -22.96) * mm});
            skLineSegment(sketch, "E1276", {"start": v(42.12, -21.72) * mm, "end": v(42.87, -21.6) * mm});
            skLineSegment(sketch, "E1277", {"start": v(43.38, -22.96) * mm, "end": v(44.13, -22.84) * mm});
            skLineSegment(sketch, "E1278", {"start": v(42.87, -21.6) * mm, "end": v(43.63, -21.48) * mm});
            skLineSegment(sketch, "E1279", {"start": v(44.13, -22.84) * mm, "end": v(44.88, -22.71) * mm});
            skLineSegment(sketch, "E1280", {"start": v(43.63, -21.48) * mm, "end": v(44.38, -21.36) * mm});
            skLineSegment(sketch, "E1281", {"start": v(44.88, -22.71) * mm, "end": v(45.63, -22.6) * mm});
            skLineSegment(sketch, "E1282", {"start": v(44.38, -21.36) * mm, "end": v(45.13, -21.23) * mm});
            skLineSegment(sketch, "E1283", {"start": v(45.63, -22.6) * mm, "end": v(46.38, -22.47) * mm});
            skLineSegment(sketch, "E1284", {"start": v(45.13, -21.23) * mm, "end": v(45.87, -21.11) * mm});
            skLineSegment(sketch, "E1285", {"start": v(46.38, -22.47) * mm, "end": v(47.12, -22.34) * mm});
            skLineSegment(sketch, "E1286", {"start": v(45.87, -21.11) * mm, "end": v(46.62, -20.99) * mm});
            skLineSegment(sketch, "E1287", {"start": v(47.12, -22.34) * mm, "end": v(47.86, -22.22) * mm});
            skLineSegment(sketch, "E1288", {"start": v(46.62, -20.99) * mm, "end": v(47.37, -20.86) * mm});
            skLineSegment(sketch, "E1289", {"start": v(47.86, -22.22) * mm, "end": v(48.6, -22.1) * mm});
            skLineSegment(sketch, "E1290", {"start": v(47.37, -20.86) * mm, "end": v(48.11, -20.74) * mm});
            skLineSegment(sketch, "E1291", {"start": v(48.6, -22.1) * mm, "end": v(49.35, -21.97) * mm});
            skLineSegment(sketch, "E1292", {"start": v(48.11, -20.74) * mm, "end": v(48.86, -20.61) * mm});
            skLineSegment(sketch, "E1293", {"start": v(49.35, -21.97) * mm, "end": v(50.09, -21.84) * mm});
            skLineSegment(sketch, "E1294", {"start": v(48.86, -20.61) * mm, "end": v(49.6, -20.5) * mm});
            skLineSegment(sketch, "E1295", {"start": v(50.09, -21.84) * mm, "end": v(50.83, -21.72) * mm});
            skLineSegment(sketch, "E1296", {"start": v(49.6, -20.5) * mm, "end": v(50.34, -20.37) * mm});
            skLineSegment(sketch, "E1297", {"start": v(50.83, -21.72) * mm, "end": v(51.56, -21.6) * mm});
            skLineSegment(sketch, "E1298", {"start": v(50.34, -20.37) * mm, "end": v(51.08, -20.24) * mm});
            skLineSegment(sketch, "E1299", {"start": v(51.56, -21.6) * mm, "end": v(52.3, -21.47) * mm});
            skLineSegment(sketch, "E1300", {"start": v(51.08, -20.24) * mm, "end": v(51.82, -20.11) * mm});
            skLineSegment(sketch, "E1301", {"start": v(52.3, -21.47) * mm, "end": v(53.03, -21.34) * mm});
            skLineSegment(sketch, "E1302", {"start": v(51.82, -20.11) * mm, "end": v(52.55, -19.99) * mm});
            skLineSegment(sketch, "E1303", {"start": v(53.03, -21.34) * mm, "end": v(53.77, -21.22) * mm});
            skLineSegment(sketch, "E1304", {"start": v(52.55, -19.99) * mm, "end": v(53.29, -19.86) * mm});
            skLineSegment(sketch, "E1305", {"start": v(53.77, -21.22) * mm, "end": v(54.5, -21.09) * mm});
            skLineSegment(sketch, "E1306", {"start": v(53.29, -19.86) * mm, "end": v(54.02, -19.74) * mm});
            skLineSegment(sketch, "E1307", {"start": v(54.5, -21.09) * mm, "end": v(55.23, -20.96) * mm});
            skLineSegment(sketch, "E1308", {"start": v(54.02, -19.74) * mm, "end": v(54.75, -19.61) * mm});
            skLineSegment(sketch, "E1309", {"start": v(55.23, -20.96) * mm, "end": v(55.96, -20.84) * mm});
            skLineSegment(sketch, "E1310", {"start": v(54.75, -19.61) * mm, "end": v(55.48, -19.48) * mm});
            skLineSegment(sketch, "E1311", {"start": v(55.96, -20.84) * mm, "end": v(56.68, -20.7) * mm});
            skLineSegment(sketch, "E1312", {"start": v(55.48, -19.48) * mm, "end": v(56.21, -19.36) * mm});
            skLineSegment(sketch, "E1313", {"start": v(56.68, -20.7) * mm, "end": v(57.4, -20.58) * mm});
            skLineSegment(sketch, "E1314", {"start": v(56.21, -19.36) * mm, "end": v(56.94, -19.23) * mm});
            skLineSegment(sketch, "E1315", {"start": v(57.4, -20.58) * mm, "end": v(58.13, -20.45) * mm});
            skLineSegment(sketch, "E1316", {"start": v(56.94, -19.23) * mm, "end": v(57.67, -19.1) * mm});
            skLineSegment(sketch, "E1317", {"start": v(58.13, -20.45) * mm, "end": v(58.85, -20.33) * mm});
            skLineSegment(sketch, "E1318", {"start": v(57.67, -19.1) * mm, "end": v(58.4, -18.98) * mm});
            skLineSegment(sketch, "E1319", {"start": v(58.85, -20.33) * mm, "end": v(59.57, -20.2) * mm});
            skLineSegment(sketch, "E1320", {"start": v(58.4, -18.98) * mm, "end": v(59.11, -18.85) * mm});
            skLineSegment(sketch, "E1321", {"start": v(59.57, -20.2) * mm, "end": v(60.3, -20.07) * mm});
            skLineSegment(sketch, "E1322", {"start": v(59.11, -18.85) * mm, "end": v(59.84, -18.72) * mm});
            skLineSegment(sketch, "E1323", {"start": v(60.3, -20.07) * mm, "end": v(61, -19.94) * mm});
            skLineSegment(sketch, "E1324", {"start": v(59.84, -18.72) * mm, "end": v(60.56, -18.6) * mm});
            skLineSegment(sketch, "E1325", {"start": v(61, -19.94) * mm, "end": v(61.72, -19.81) * mm});
            skLineSegment(sketch, "E1326", {"start": v(60.56, -18.6) * mm, "end": v(61.27, -18.47) * mm});
            skLineSegment(sketch, "E1327", {"start": v(61.72, -19.81) * mm, "end": v(62.44, -19.69) * mm});
            skLineSegment(sketch, "E1328", {"start": v(61.27, -18.47) * mm, "end": v(61.99, -18.34) * mm});
            skLineSegment(sketch, "E1329", {"start": v(62.44, -19.69) * mm, "end": v(63.15, -19.56) * mm});
            skLineSegment(sketch, "E1330", {"start": v(61.99, -18.34) * mm, "end": v(62.7, -18.2) * mm});
            skLineSegment(sketch, "E1331", {"start": v(63.15, -19.56) * mm, "end": v(63.86, -19.43) * mm});
            skLineSegment(sketch, "E1332", {"start": v(62.7, -18.2) * mm, "end": v(63.42, -18.08) * mm});
            skLineSegment(sketch, "E1333", {"start": v(63.86, -19.43) * mm, "end": v(64.57, -19.3) * mm});
            skLineSegment(sketch, "E1334", {"start": v(63.42, -18.08) * mm, "end": v(64.13, -17.95) * mm});
            skLineSegment(sketch, "E1335", {"start": v(64.57, -19.3) * mm, "end": v(65.27, -19.17) * mm});
            skLineSegment(sketch, "E1336", {"start": v(64.13, -17.95) * mm, "end": v(64.84, -17.82) * mm});
            skLineSegment(sketch, "E1337", {"start": v(65.27, -19.17) * mm, "end": v(65.98, -19.04) * mm});
            skLineSegment(sketch, "E1338", {"start": v(64.84, -17.82) * mm, "end": v(65.54, -17.7) * mm});
            skLineSegment(sketch, "E1339", {"start": v(65.98, -19.04) * mm, "end": v(66.68, -18.91) * mm});
            skLineSegment(sketch, "E1340", {"start": v(65.54, -17.7) * mm, "end": v(66.25, -17.57) * mm});
            skLineSegment(sketch, "E1341", {"start": v(66.68, -18.91) * mm, "end": v(67.38, -18.78) * mm});
            skLineSegment(sketch, "E1342", {"start": v(66.25, -17.57) * mm, "end": v(66.95, -17.44) * mm});
            skLineSegment(sketch, "E1343", {"start": v(67.38, -18.78) * mm, "end": v(68.08, -18.65) * mm});
            skLineSegment(sketch, "E1344", {"start": v(66.95, -17.44) * mm, "end": v(67.66, -17.3) * mm});
            skLineSegment(sketch, "E1345", {"start": v(68.08, -18.65) * mm, "end": v(68.78, -18.53) * mm});
            skLineSegment(sketch, "E1346", {"start": v(67.66, -17.3) * mm, "end": v(68.36, -17.18) * mm});
            skLineSegment(sketch, "E1347", {"start": v(68.78, -18.53) * mm, "end": v(69.48, -18.4) * mm});
            skLineSegment(sketch, "E1348", {"start": v(68.36, -17.18) * mm, "end": v(69.06, -17.05) * mm});
            skLineSegment(sketch, "E1349", {"start": v(69.48, -18.4) * mm, "end": v(70.17, -18.27) * mm});
            skLineSegment(sketch, "E1350", {"start": v(69.06, -17.05) * mm, "end": v(69.75, -16.92) * mm});
            skLineSegment(sketch, "E1351", {"start": v(70.17, -18.27) * mm, "end": v(70.86, -18.14) * mm});
            skLineSegment(sketch, "E1352", {"start": v(69.75, -16.92) * mm, "end": v(70.45, -16.8) * mm});
            skLineSegment(sketch, "E1353", {"start": v(70.86, -18.14) * mm, "end": v(71.55, -18) * mm});
            skLineSegment(sketch, "E1354", {"start": v(70.45, -16.8) * mm, "end": v(71.14, -16.66) * mm});
            skLineSegment(sketch, "E1355", {"start": v(71.55, -18) * mm, "end": v(72.24, -17.88) * mm});
            skLineSegment(sketch, "E1356", {"start": v(71.14, -16.66) * mm, "end": v(71.83, -16.53) * mm});
            skLineSegment(sketch, "E1357", {"start": v(72.24, -17.88) * mm, "end": v(72.93, -17.75) * mm});
            skLineSegment(sketch, "E1358", {"start": v(71.83, -16.53) * mm, "end": v(72.52, -16.4) * mm});
            skLineSegment(sketch, "E1359", {"start": v(72.93, -17.75) * mm, "end": v(73.61, -17.62) * mm});
            skLineSegment(sketch, "E1360", {"start": v(72.52, -16.4) * mm, "end": v(73.2, -16.28) * mm});
            skLineSegment(sketch, "E1361", {"start": v(73.61, -17.62) * mm, "end": v(74.3, -17.5) * mm});
            skLineSegment(sketch, "E1362", {"start": v(73.2, -16.28) * mm, "end": v(73.9, -16.15) * mm});
            skLineSegment(sketch, "E1363", {"start": v(74.3, -17.5) * mm, "end": v(74.97, -17.36) * mm});
            skLineSegment(sketch, "E1364", {"start": v(73.9, -16.15) * mm, "end": v(74.57, -16.02) * mm});
            skLineSegment(sketch, "E1365", {"start": v(74.97, -17.36) * mm, "end": v(75.65, -17.23) * mm});
            skLineSegment(sketch, "E1366", {"start": v(74.57, -16.02) * mm, "end": v(75.25, -15.89) * mm});
            skLineSegment(sketch, "E1367", {"start": v(75.65, -17.23) * mm, "end": v(76.33, -17.1) * mm});
            skLineSegment(sketch, "E1368", {"start": v(75.25, -15.89) * mm, "end": v(75.93, -15.76) * mm});
            skLineSegment(sketch, "E1369", {"start": v(76.33, -17.1) * mm, "end": v(77, -16.97) * mm});
            skLineSegment(sketch, "E1370", {"start": v(75.93, -15.76) * mm, "end": v(76.6, -15.63) * mm});
            skLineSegment(sketch, "E1371", {"start": v(77, -16.97) * mm, "end": v(77.67, -16.84) * mm});
            skLineSegment(sketch, "E1372", {"start": v(76.6, -15.63) * mm, "end": v(77.28, -15.5) * mm});
            skLineSegment(sketch, "E1373", {"start": v(77.67, -16.84) * mm, "end": v(78.34, -16.72) * mm});
            skLineSegment(sketch, "E1374", {"start": v(77.28, -15.5) * mm, "end": v(77.96, -15.37) * mm});
            skLineSegment(sketch, "E1375", {"start": v(78.34, -16.72) * mm, "end": v(79, -16.59) * mm});
            skLineSegment(sketch, "E1376", {"start": v(77.96, -15.37) * mm, "end": v(78.63, -15.24) * mm});
            skLineSegment(sketch, "E1377", {"start": v(79, -16.59) * mm, "end": v(79.67, -16.46) * mm});
            skLineSegment(sketch, "E1378", {"start": v(78.63, -15.24) * mm, "end": v(79.3, -15.11) * mm});
            skLineSegment(sketch, "E1379", {"start": v(79.67, -16.46) * mm, "end": v(80.34, -16.33) * mm});
            skLineSegment(sketch, "E1380", {"start": v(79.3, -15.11) * mm, "end": v(79.96, -14.98) * mm});
            skLineSegment(sketch, "E1381", {"start": v(80.34, -16.33) * mm, "end": v(81, -16.2) * mm});
            skLineSegment(sketch, "E1382", {"start": v(79.96, -14.98) * mm, "end": v(80.62, -14.86) * mm});
            skLineSegment(sketch, "E1383", {"start": v(81, -16.2) * mm, "end": v(81.66, -16.07) * mm});
            skLineSegment(sketch, "E1384", {"start": v(80.62, -14.86) * mm, "end": v(81.28, -14.73) * mm});
            skLineSegment(sketch, "E1385", {"start": v(81.66, -16.07) * mm, "end": v(82.31, -15.94) * mm});
            skLineSegment(sketch, "E1386", {"start": v(81.28, -14.73) * mm, "end": v(81.94, -14.6) * mm});
            skLineSegment(sketch, "E1387", {"start": v(82.31, -15.94) * mm, "end": v(82.97, -15.81) * mm});
            skLineSegment(sketch, "E1388", {"start": v(81.94, -14.6) * mm, "end": v(82.6, -14.47) * mm});
            skLineSegment(sketch, "E1389", {"start": v(82.97, -15.81) * mm, "end": v(83.62, -15.68) * mm});
            skLineSegment(sketch, "E1390", {"start": v(82.6, -14.47) * mm, "end": v(83.26, -14.34) * mm});
            skLineSegment(sketch, "E1391", {"start": v(83.62, -15.68) * mm, "end": v(84.27, -15.56) * mm});
            skLineSegment(sketch, "E1392", {"start": v(83.26, -14.34) * mm, "end": v(83.9, -14.21) * mm});
            skLineSegment(sketch, "E1393", {"start": v(84.27, -15.56) * mm, "end": v(84.91, -15.43) * mm});
            skLineSegment(sketch, "E1394", {"start": v(83.9, -14.21) * mm, "end": v(84.56, -14.08) * mm});
            skLineSegment(sketch, "E1395", {"start": v(84.91, -15.43) * mm, "end": v(85.56, -15.3) * mm});
            skLineSegment(sketch, "E1396", {"start": v(84.56, -14.08) * mm, "end": v(85.2, -13.96) * mm});
            skLineSegment(sketch, "E1397", {"start": v(85.56, -15.3) * mm, "end": v(86.2, -15.17) * mm});
            skLineSegment(sketch, "E1398", {"start": v(85.2, -13.96) * mm, "end": v(85.85, -13.83) * mm});
            skLineSegment(sketch, "E1399", {"start": v(86.2, -15.17) * mm, "end": v(86.84, -15.04) * mm});
            skLineSegment(sketch, "E1400", {"start": v(85.85, -13.83) * mm, "end": v(86.5, -13.7) * mm});
            skLineSegment(sketch, "E1401", {"start": v(86.84, -15.04) * mm, "end": v(87.48, -14.91) * mm});
            skLineSegment(sketch, "E1402", {"start": v(86.5, -13.7) * mm, "end": v(87.14, -13.57) * mm});
            skLineSegment(sketch, "E1403", {"start": v(87.48, -14.91) * mm, "end": v(88.11, -14.79) * mm});
            skLineSegment(sketch, "E1404", {"start": v(87.14, -13.57) * mm, "end": v(87.77, -13.44) * mm});
            skLineSegment(sketch, "E1405", {"start": v(88.11, -14.79) * mm, "end": v(88.75, -14.66) * mm});
            skLineSegment(sketch, "E1406", {"start": v(87.77, -13.44) * mm, "end": v(88.41, -13.32) * mm});
            skLineSegment(sketch, "E1407", {"start": v(88.75, -14.66) * mm, "end": v(89.38, -14.53) * mm});
            skLineSegment(sketch, "E1408", {"start": v(88.41, -13.32) * mm, "end": v(89.04, -13.19) * mm});
            skLineSegment(sketch, "E1409", {"start": v(89.38, -14.53) * mm, "end": v(90, -14.4) * mm});
            skLineSegment(sketch, "E1410", {"start": v(89.04, -13.19) * mm, "end": v(89.68, -13.06) * mm});
            skLineSegment(sketch, "E1411", {"start": v(90, -14.4) * mm, "end": v(90.63, -14.28) * mm});
            skLineSegment(sketch, "E1412", {"start": v(89.68, -13.06) * mm, "end": v(90.3, -12.93) * mm});
            skLineSegment(sketch, "E1413", {"start": v(90.63, -14.28) * mm, "end": v(91.25, -14.15) * mm});
            skLineSegment(sketch, "E1414", {"start": v(90.3, -12.93) * mm, "end": v(90.93, -12.8) * mm});
            skLineSegment(sketch, "E1415", {"start": v(91.25, -14.15) * mm, "end": v(91.87, -14.02) * mm});
            skLineSegment(sketch, "E1416", {"start": v(90.93, -12.8) * mm, "end": v(91.55, -12.68) * mm});
            skLineSegment(sketch, "E1417", {"start": v(91.87, -14.02) * mm, "end": v(92.5, -13.9) * mm});
            skLineSegment(sketch, "E1418", {"start": v(91.55, -12.68) * mm, "end": v(92.17, -12.55) * mm});
            skLineSegment(sketch, "E1419", {"start": v(92.5, -13.9) * mm, "end": v(93.1, -13.77) * mm});
            skLineSegment(sketch, "E1420", {"start": v(92.17, -12.55) * mm, "end": v(92.8, -12.43) * mm});
            skLineSegment(sketch, "E1421", {"start": v(93.1, -13.77) * mm, "end": v(93.72, -13.65) * mm});
            skLineSegment(sketch, "E1422", {"start": v(92.8, -12.43) * mm, "end": v(93.4, -12.3) * mm});
            skLineSegment(sketch, "E1423", {"start": v(93.72, -13.65) * mm, "end": v(94.33, -13.52) * mm});
            skLineSegment(sketch, "E1424", {"start": v(93.4, -12.3) * mm, "end": v(94.02, -12.18) * mm});
            skLineSegment(sketch, "E1425", {"start": v(94.33, -13.52) * mm, "end": v(94.94, -13.4) * mm});
            skLineSegment(sketch, "E1426", {"start": v(94.02, -12.18) * mm, "end": v(94.63, -12.05) * mm});
            skLineSegment(sketch, "E1427", {"start": v(94.94, -13.4) * mm, "end": v(95.54, -13.27) * mm});
            skLineSegment(sketch, "E1428", {"start": v(94.63, -12.05) * mm, "end": v(95.24, -11.93) * mm});
            skLineSegment(sketch, "E1429", {"start": v(95.54, -13.27) * mm, "end": v(96.15, -13.14) * mm});
            skLineSegment(sketch, "E1430", {"start": v(95.24, -11.93) * mm, "end": v(95.85, -11.8) * mm});
            skLineSegment(sketch, "E1431", {"start": v(96.15, -13.14) * mm, "end": v(96.75, -13.02) * mm});
            skLineSegment(sketch, "E1432", {"start": v(95.85, -11.8) * mm, "end": v(96.45, -11.68) * mm});
            skLineSegment(sketch, "E1433", {"start": v(96.75, -13.02) * mm, "end": v(97.34, -12.9) * mm});
            skLineSegment(sketch, "E1434", {"start": v(96.45, -11.68) * mm, "end": v(97.05, -11.55) * mm});
            skLineSegment(sketch, "E1435", {"start": v(97.34, -12.9) * mm, "end": v(97.94, -12.77) * mm});
            skLineSegment(sketch, "E1436", {"start": v(97.05, -11.55) * mm, "end": v(97.65, -11.43) * mm});
            skLineSegment(sketch, "E1437", {"start": v(97.94, -12.77) * mm, "end": v(98.53, -12.65) * mm});
            skLineSegment(sketch, "E1438", {"start": v(97.65, -11.43) * mm, "end": v(98.25, -11.3) * mm});
            skLineSegment(sketch, "E1439", {"start": v(98.53, -12.65) * mm, "end": v(99.12, -12.52) * mm});
            skLineSegment(sketch, "E1440", {"start": v(98.25, -11.3) * mm, "end": v(98.84, -11.18) * mm});
            skLineSegment(sketch, "E1441", {"start": v(99.12, -12.52) * mm, "end": v(99.7, -12.4) * mm});
            skLineSegment(sketch, "E1442", {"start": v(98.84, -11.18) * mm, "end": v(99.43, -11.05) * mm});
            skLineSegment(sketch, "E1443", {"start": v(99.7, -12.4) * mm, "end": v(100.29, -12.28) * mm});
            skLineSegment(sketch, "E1444", {"start": v(99.43, -11.05) * mm, "end": v(100.02, -10.93) * mm});
            skLineSegment(sketch, "E1445", {"start": v(100.29, -12.28) * mm, "end": v(100.87, -12.15) * mm});
            skLineSegment(sketch, "E1446", {"start": v(100.02, -10.93) * mm, "end": v(100.6, -10.8) * mm});
            skLineSegment(sketch, "E1447", {"start": v(100.87, -12.15) * mm, "end": v(101.45, -12.03) * mm});
            skLineSegment(sketch, "E1448", {"start": v(100.6, -10.8) * mm, "end": v(101.18, -10.69) * mm});
            skLineSegment(sketch, "E1449", {"start": v(101.45, -12.03) * mm, "end": v(102.02, -11.9) * mm});
            skLineSegment(sketch, "E1450", {"start": v(101.18, -10.69) * mm, "end": v(101.76, -10.56) * mm});
            skLineSegment(sketch, "E1451", {"start": v(102.02, -11.9) * mm, "end": v(102.6, -11.79) * mm});
            skLineSegment(sketch, "E1452", {"start": v(101.76, -10.56) * mm, "end": v(102.34, -10.44) * mm});
            skLineSegment(sketch, "E1453", {"start": v(102.6, -11.79) * mm, "end": v(103.17, -11.66) * mm});
            skLineSegment(sketch, "E1454", {"start": v(102.34, -10.44) * mm, "end": v(102.9, -10.32) * mm});
            skLineSegment(sketch, "E1455", {"start": v(103.17, -11.66) * mm, "end": v(103.73, -11.54) * mm});
            skLineSegment(sketch, "E1456", {"start": v(102.9, -10.32) * mm, "end": v(103.48, -10.2) * mm});
            skLineSegment(sketch, "E1457", {"start": v(103.73, -11.54) * mm, "end": v(104.3, -11.42) * mm});
            skLineSegment(sketch, "E1458", {"start": v(103.48, -10.2) * mm, "end": v(104.05, -10.08) * mm});
            skLineSegment(sketch, "E1459", {"start": v(104.3, -11.42) * mm, "end": v(104.86, -11.3) * mm});
            skLineSegment(sketch, "E1460", {"start": v(104.05, -10.08) * mm, "end": v(104.61, -9.96) * mm});
            skLineSegment(sketch, "E1461", {"start": v(104.86, -11.3) * mm, "end": v(105.42, -11.18) * mm});
            skLineSegment(sketch, "E1462", {"start": v(104.61, -9.96) * mm, "end": v(105.17, -9.84) * mm});
            skLineSegment(sketch, "E1463", {"start": v(105.42, -11.18) * mm, "end": v(105.97, -11.06) * mm});
            skLineSegment(sketch, "E1464", {"start": v(105.17, -9.84) * mm, "end": v(105.73, -9.72) * mm});
            skLineSegment(sketch, "E1465", {"start": v(105.97, -11.06) * mm, "end": v(106.53, -10.94) * mm});
            skLineSegment(sketch, "E1466", {"start": v(105.73, -9.72) * mm, "end": v(106.29, -9.6) * mm});
            skLineSegment(sketch, "E1467", {"start": v(106.53, -10.94) * mm, "end": v(107.07, -10.82) * mm});
            skLineSegment(sketch, "E1468", {"start": v(106.29, -9.6) * mm, "end": v(106.84, -9.48) * mm});
            skLineSegment(sketch, "E1469", {"start": v(107.07, -10.82) * mm, "end": v(107.62, -10.7) * mm});
            skLineSegment(sketch, "E1470", {"start": v(106.84, -9.48) * mm, "end": v(107.4, -9.36) * mm});
            skLineSegment(sketch, "E1471", {"start": v(107.62, -10.7) * mm, "end": v(108.17, -10.59) * mm});
            skLineSegment(sketch, "E1472", {"start": v(107.4, -9.36) * mm, "end": v(107.94, -9.24) * mm});
            skLineSegment(sketch, "E1473", {"start": v(108.17, -10.59) * mm, "end": v(108.7, -10.47) * mm});
            skLineSegment(sketch, "E1474", {"start": v(107.94, -9.24) * mm, "end": v(108.48, -9.12) * mm});
            skLineSegment(sketch, "E1475", {"start": v(108.7, -10.47) * mm, "end": v(109.24, -10.35) * mm});
            skLineSegment(sketch, "E1476", {"start": v(108.48, -9.12) * mm, "end": v(109.03, -9) * mm});
            skLineSegment(sketch, "E1477", {"start": v(109.24, -10.35) * mm, "end": v(109.78, -10.23) * mm});
            skLineSegment(sketch, "E1478", {"start": v(109.03, -9) * mm, "end": v(109.56, -8.89) * mm});
            skLineSegment(sketch, "E1479", {"start": v(109.78, -10.23) * mm, "end": v(110.31, -10.12) * mm});
            skLineSegment(sketch, "E1480", {"start": v(109.56, -8.89) * mm, "end": v(110.1, -8.77) * mm});
            skLineSegment(sketch, "E1481", {"start": v(110.31, -10.12) * mm, "end": v(110.84, -10) * mm});
            skLineSegment(sketch, "E1482", {"start": v(110.1, -8.77) * mm, "end": v(110.63, -8.65) * mm});
            skLineSegment(sketch, "E1483", {"start": v(110.84, -10) * mm, "end": v(111.37, -9.89) * mm});
            skLineSegment(sketch, "E1484", {"start": v(110.63, -8.65) * mm, "end": v(111.16, -8.54) * mm});
            skLineSegment(sketch, "E1485", {"start": v(111.37, -9.89) * mm, "end": v(111.89, -9.77) * mm});
            skLineSegment(sketch, "E1486", {"start": v(111.16, -8.54) * mm, "end": v(111.69, -8.42) * mm});
            skLineSegment(sketch, "E1487", {"start": v(111.89, -9.77) * mm, "end": v(112.4, -9.65) * mm});
            skLineSegment(sketch, "E1488", {"start": v(111.69, -8.42) * mm, "end": v(112.21, -8.3) * mm});
            skLineSegment(sketch, "E1489", {"start": v(112.4, -9.65) * mm, "end": v(112.92, -9.54) * mm});
            skLineSegment(sketch, "E1490", {"start": v(112.21, -8.3) * mm, "end": v(112.73, -8.2) * mm});
            skLineSegment(sketch, "E1491", {"start": v(112.92, -9.54) * mm, "end": v(113.44, -9.43) * mm});
            skLineSegment(sketch, "E1492", {"start": v(112.73, -8.2) * mm, "end": v(113.25, -8.08) * mm});
            skLineSegment(sketch, "E1493", {"start": v(113.44, -9.43) * mm, "end": v(113.95, -9.31) * mm});
            skLineSegment(sketch, "E1494", {"start": v(113.25, -8.08) * mm, "end": v(113.76, -7.96) * mm});
            skLineSegment(sketch, "E1495", {"start": v(113.95, -9.31) * mm, "end": v(114.45, -9.2) * mm});
            skLineSegment(sketch, "E1496", {"start": v(113.76, -7.96) * mm, "end": v(114.27, -7.85) * mm});
            skLineSegment(sketch, "E1497", {"start": v(114.45, -9.2) * mm, "end": v(114.96, -9.09) * mm});
            skLineSegment(sketch, "E1498", {"start": v(114.27, -7.85) * mm, "end": v(114.78, -7.74) * mm});
            skLineSegment(sketch, "E1499", {"start": v(114.96, -9.09) * mm, "end": v(115.46, -8.98) * mm});
            skLineSegment(sketch, "E1500", {"start": v(114.78, -7.74) * mm, "end": v(115.29, -7.62) * mm});
            skLineSegment(sketch, "E1501", {"start": v(115.46, -8.98) * mm, "end": v(115.96, -8.86) * mm});
            skLineSegment(sketch, "E1502", {"start": v(115.29, -7.62) * mm, "end": v(115.79, -7.51) * mm});
            skLineSegment(sketch, "E1503", {"start": v(115.96, -8.86) * mm, "end": v(116.45, -8.75) * mm});
            skLineSegment(sketch, "E1504", {"start": v(115.79, -7.51) * mm, "end": v(116.29, -7.4) * mm});
            skLineSegment(sketch, "E1505", {"start": v(116.45, -8.75) * mm, "end": v(116.94, -8.64) * mm});
            skLineSegment(sketch, "E1506", {"start": v(116.29, -7.4) * mm, "end": v(116.78, -7.29) * mm});
            skLineSegment(sketch, "E1507", {"start": v(116.94, -8.64) * mm, "end": v(117.43, -8.53) * mm});
            skLineSegment(sketch, "E1508", {"start": v(116.78, -7.29) * mm, "end": v(117.27, -7.18) * mm});
            skLineSegment(sketch, "E1509", {"start": v(117.43, -8.53) * mm, "end": v(117.92, -8.42) * mm});
            skLineSegment(sketch, "E1510", {"start": v(117.27, -7.18) * mm, "end": v(117.76, -7.07) * mm});
            skLineSegment(sketch, "E1511", {"start": v(117.92, -8.42) * mm, "end": v(118.4, -8.31) * mm});
            skLineSegment(sketch, "E1512", {"start": v(117.76, -7.07) * mm, "end": v(118.25, -6.96) * mm});
            skLineSegment(sketch, "E1513", {"start": v(118.4, -8.31) * mm, "end": v(118.88, -8.2) * mm});
            skLineSegment(sketch, "E1514", {"start": v(118.25, -6.96) * mm, "end": v(118.73, -6.85) * mm});
            skLineSegment(sketch, "E1515", {"start": v(118.88, -8.2) * mm, "end": v(119.35, -8.1) * mm});
            skLineSegment(sketch, "E1516", {"start": v(118.73, -6.85) * mm, "end": v(119.2, -6.74) * mm});
            skLineSegment(sketch, "E1517", {"start": v(119.35, -8.1) * mm, "end": v(119.82, -7.99) * mm});
            skLineSegment(sketch, "E1518", {"start": v(119.2, -6.74) * mm, "end": v(119.68, -6.63) * mm});
            skLineSegment(sketch, "E1519", {"start": v(119.82, -7.99) * mm, "end": v(120.3, -7.88) * mm});
            skLineSegment(sketch, "E1520", {"start": v(119.68, -6.63) * mm, "end": v(120.16, -6.53) * mm});
            skLineSegment(sketch, "E1521", {"start": v(120.3, -7.88) * mm, "end": v(120.76, -7.78) * mm});
            skLineSegment(sketch, "E1522", {"start": v(120.16, -6.53) * mm, "end": v(120.63, -6.42) * mm});
            skLineSegment(sketch, "E1523", {"start": v(120.76, -7.78) * mm, "end": v(121.22, -7.67) * mm});
            skLineSegment(sketch, "E1524", {"start": v(120.63, -6.42) * mm, "end": v(121.1, -6.31) * mm});
            skLineSegment(sketch, "E1525", {"start": v(121.22, -7.67) * mm, "end": v(121.68, -7.57) * mm});
            skLineSegment(sketch, "E1526", {"start": v(121.1, -6.31) * mm, "end": v(121.55, -6.2) * mm});
            skLineSegment(sketch, "E1527", {"start": v(121.68, -7.57) * mm, "end": v(122.13, -7.46) * mm});
            skLineSegment(sketch, "E1528", {"start": v(121.55, -6.2) * mm, "end": v(122.01, -6.1) * mm});
            skLineSegment(sketch, "E1529", {"start": v(122.13, -7.46) * mm, "end": v(122.59, -7.36) * mm});
            skLineSegment(sketch, "E1530", {"start": v(122.01, -6.1) * mm, "end": v(122.47, -6) * mm});
            skLineSegment(sketch, "E1531", {"start": v(122.59, -7.36) * mm, "end": v(123.03, -7.25) * mm});
            skLineSegment(sketch, "E1532", {"start": v(122.47, -6) * mm, "end": v(122.92, -5.9) * mm});
            skLineSegment(sketch, "E1533", {"start": v(123.03, -7.25) * mm, "end": v(123.48, -7.15) * mm});
            skLineSegment(sketch, "E1534", {"start": v(122.92, -5.9) * mm, "end": v(123.37, -5.8) * mm});
            skLineSegment(sketch, "E1535", {"start": v(123.48, -7.15) * mm, "end": v(123.92, -7.05) * mm});
            skLineSegment(sketch, "E1536", {"start": v(123.37, -5.8) * mm, "end": v(123.82, -5.69) * mm});
            skLineSegment(sketch, "E1537", {"start": v(123.92, -7.05) * mm, "end": v(124.36, -6.95) * mm});
            skLineSegment(sketch, "E1538", {"start": v(123.82, -5.69) * mm, "end": v(124.26, -5.59) * mm});
            skLineSegment(sketch, "E1539", {"start": v(124.36, -6.95) * mm, "end": v(124.8, -6.85) * mm});
            skLineSegment(sketch, "E1540", {"start": v(124.26, -5.59) * mm, "end": v(124.7, -5.49) * mm});
            skLineSegment(sketch, "E1541", {"start": v(124.8, -6.85) * mm, "end": v(125.23, -6.75) * mm});
            skLineSegment(sketch, "E1542", {"start": v(124.7, -5.49) * mm, "end": v(125.13, -5.39) * mm});
            skLineSegment(sketch, "E1543", {"start": v(125.23, -6.75) * mm, "end": v(125.65, -6.65) * mm});
            skLineSegment(sketch, "E1544", {"start": v(125.13, -5.39) * mm, "end": v(125.57, -5.28) * mm});
            skLineSegment(sketch, "E1545", {"start": v(125.65, -6.65) * mm, "end": v(126.08, -6.55) * mm});
            skLineSegment(sketch, "E1546", {"start": v(125.57, -5.28) * mm, "end": v(126, -5.19) * mm});
            skLineSegment(sketch, "E1547", {"start": v(126.08, -6.55) * mm, "end": v(126.5, -6.45) * mm});
            skLineSegment(sketch, "E1548", {"start": v(126, -5.19) * mm, "end": v(126.42, -5.09) * mm});
            skLineSegment(sketch, "E1549", {"start": v(126.5, -6.45) * mm, "end": v(126.92, -6.35) * mm});
            skLineSegment(sketch, "E1550", {"start": v(126.42, -5.09) * mm, "end": v(126.84, -4.99) * mm});
            skLineSegment(sketch, "E1551", {"start": v(126.92, -6.35) * mm, "end": v(127.33, -6.25) * mm});
            skLineSegment(sketch, "E1552", {"start": v(126.84, -4.99) * mm, "end": v(127.26, -4.9) * mm});
            skLineSegment(sketch, "E1553", {"start": v(127.33, -6.25) * mm, "end": v(127.74, -6.16) * mm});
            skLineSegment(sketch, "E1554", {"start": v(127.26, -4.9) * mm, "end": v(127.68, -4.8) * mm});
            skLineSegment(sketch, "E1555", {"start": v(127.74, -6.16) * mm, "end": v(128.15, -6.06) * mm});
            skLineSegment(sketch, "E1556", {"start": v(127.68, -4.8) * mm, "end": v(128.09, -4.7) * mm});
            skLineSegment(sketch, "E1557", {"start": v(128.15, -6.06) * mm, "end": v(128.56, -5.97) * mm});
            skLineSegment(sketch, "E1558", {"start": v(128.09, -4.7) * mm, "end": v(128.5, -4.6) * mm});
            skLineSegment(sketch, "E1559", {"start": v(128.56, -5.97) * mm, "end": v(128.96, -5.87) * mm});
            skLineSegment(sketch, "E1560", {"start": v(128.5, -4.6) * mm, "end": v(128.9, -4.5) * mm});
            skLineSegment(sketch, "E1561", {"start": v(128.96, -5.87) * mm, "end": v(129.35, -5.78) * mm});
            skLineSegment(sketch, "E1562", {"start": v(128.9, -4.5) * mm, "end": v(129.3, -4.41) * mm});
            skLineSegment(sketch, "E1563", {"start": v(129.35, -5.78) * mm, "end": v(129.75, -5.69) * mm});
            skLineSegment(sketch, "E1564", {"start": v(129.3, -4.41) * mm, "end": v(129.7, -4.32) * mm});
            skLineSegment(sketch, "E1565", {"start": v(129.75, -5.69) * mm, "end": v(130.13, -5.6) * mm});
            skLineSegment(sketch, "E1566", {"start": v(129.7, -4.32) * mm, "end": v(130.1, -4.23) * mm});
            skLineSegment(sketch, "E1567", {"start": v(130.13, -5.6) * mm, "end": v(130.52, -5.5) * mm});
            skLineSegment(sketch, "E1568", {"start": v(130.1, -4.23) * mm, "end": v(130.48, -4.13) * mm});
            skLineSegment(sketch, "E1569", {"start": v(130.52, -5.5) * mm, "end": v(130.9, -5.41) * mm});
            skLineSegment(sketch, "E1570", {"start": v(130.48, -4.13) * mm, "end": v(130.87, -4.04) * mm});
            skLineSegment(sketch, "E1571", {"start": v(130.9, -5.41) * mm, "end": v(131.28, -5.32) * mm});
            skLineSegment(sketch, "E1572", {"start": v(130.87, -4.04) * mm, "end": v(131.25, -3.95) * mm});
            skLineSegment(sketch, "E1573", {"start": v(131.28, -5.32) * mm, "end": v(131.66, -5.23) * mm});
            skLineSegment(sketch, "E1574", {"start": v(131.25, -3.95) * mm, "end": v(131.63, -3.86) * mm});
            skLineSegment(sketch, "E1575", {"start": v(131.66, -5.23) * mm, "end": v(132.03, -5.14) * mm});
            skLineSegment(sketch, "E1576", {"start": v(131.63, -3.86) * mm, "end": v(132, -3.77) * mm});
            skLineSegment(sketch, "E1577", {"start": v(132.03, -5.14) * mm, "end": v(132.4, -5.05) * mm});
            skLineSegment(sketch, "E1578", {"start": v(132, -3.77) * mm, "end": v(132.38, -3.68) * mm});
            skLineSegment(sketch, "E1579", {"start": v(132.4, -5.05) * mm, "end": v(132.76, -4.97) * mm});
            skLineSegment(sketch, "E1580", {"start": v(132.38, -3.68) * mm, "end": v(132.75, -3.6) * mm});
            skLineSegment(sketch, "E1581", {"start": v(132.76, -4.97) * mm, "end": v(133.12, -4.88) * mm});
            skLineSegment(sketch, "E1582", {"start": v(132.75, -3.6) * mm, "end": v(133.11, -3.5) * mm});
            skLineSegment(sketch, "E1583", {"start": v(133.12, -4.88) * mm, "end": v(133.48, -4.8) * mm});
            skLineSegment(sketch, "E1584", {"start": v(133.11, -3.5) * mm, "end": v(133.47, -3.42) * mm});
            skLineSegment(sketch, "E1585", {"start": v(133.48, -4.8) * mm, "end": v(133.83, -4.7) * mm});
            skLineSegment(sketch, "E1586", {"start": v(133.47, -3.42) * mm, "end": v(133.83, -3.34) * mm});
            skLineSegment(sketch, "E1587", {"start": v(133.83, -4.7) * mm, "end": v(134.18, -4.63) * mm});
            skLineSegment(sketch, "E1588", {"start": v(134.18, -4.63) * mm, "end": v(134.53, -4.54) * mm});
            skLineSegment(sketch, "E1589", {"start": v(134.53, -4.54) * mm, "end": v(134.87, -4.46) * mm});
            skLineSegment(sketch, "E1590", {"start": v(134.87, -4.46) * mm, "end": v(135.21, -4.38) * mm});
            skLineSegment(sketch, "E1591", {"start": v(135.21, -4.38) * mm, "end": v(135.55, -4.3) * mm});
            skLineSegment(sketch, "E1592", {"start": v(135.55, -4.3) * mm, "end": v(135.88, -4.22) * mm});
            skLineSegment(sketch, "E1593", {"start": v(135.88, -4.22) * mm, "end": v(136.2, -4.14) * mm});
            skLineSegment(sketch, "E1594", {"start": v(136.2, -4.14) * mm, "end": v(136.53, -4.06) * mm});
            skLineSegment(sketch, "E1595", {"start": v(136.53, -4.06) * mm, "end": v(136.85, -3.98) * mm});
            skLineSegment(sketch, "E1596", {"start": v(136.85, -3.98) * mm, "end": v(137.16, -3.9) * mm});
            skLineSegment(sketch, "E1597", {"start": v(137.16, -3.9) * mm, "end": v(137.48, -3.83) * mm});
            skLineSegment(sketch, "E1598", {"start": v(137.48, -3.83) * mm, "end": v(137.79, -3.75) * mm});
            skLineSegment(sketch, "E1599", {"start": v(137.79, -3.75) * mm, "end": v(138.1, -3.68) * mm});
            skLineSegment(sketch, "E1600", {"start": v(138.1, -3.68) * mm, "end": v(138.4, -3.6) * mm});
            skLineSegment(sketch, "E1601", {"start": v(138.4, -3.6) * mm, "end": v(138.69, -3.53) * mm});
            skLineSegment(sketch, "E1602", {"start": v(138.69, -3.53) * mm, "end": v(138.98, -3.46) * mm});
            skLineSegment(sketch, "E1603", {"start": v(138.98, -3.46) * mm, "end": v(139.27, -3.39) * mm});
            skLineSegment(sketch, "E1604", {"start": v(139.27, -3.39) * mm, "end": v(139.56, -3.32) * mm});
            skLineSegment(sketch, "E1605", {"start": v(139.56, -3.32) * mm, "end": v(139.84, -3.25) * mm});
            skLineSegment(sketch, "E1606", {"start": v(139.84, -3.25) * mm, "end": v(140.12, -3.18) * mm});
            skLineSegment(sketch, "E1607", {"start": v(140.12, -3.18) * mm, "end": v(140.4, -3.11) * mm});
            skLineSegment(sketch, "E1608", {"start": v(140.4, -3.11) * mm, "end": v(140.66, -3.04) * mm});
            skLineSegment(sketch, "E1609", {"start": v(140.66, -3.04) * mm, "end": v(140.93, -2.98) * mm});
            skLineSegment(sketch, "E1610", {"start": v(140.93, -2.98) * mm, "end": v(141.2, -2.91) * mm});
            skLineSegment(sketch, "E1611", {"start": v(141.2, -2.91) * mm, "end": v(141.45, -2.85) * mm});
            skLineSegment(sketch, "E1612", {"start": v(141.45, -2.85) * mm, "end": v(141.7, -2.79) * mm});
            skLineSegment(sketch, "E1613", {"start": v(141.7, -2.79) * mm, "end": v(141.96, -2.72) * mm});
            skLineSegment(sketch, "E1614", {"start": v(141.96, -2.72) * mm, "end": v(142.2, -2.66) * mm});
            skLineSegment(sketch, "E1615", {"start": v(142.2, -2.66) * mm, "end": v(142.45, -2.6) * mm});
            skLineSegment(sketch, "E1616", {"start": v(142.45, -2.6) * mm, "end": v(142.69, -2.54) * mm});
            skLineSegment(sketch, "E1617", {"start": v(142.69, -2.54) * mm, "end": v(142.93, -2.48) * mm});
            skLineSegment(sketch, "E1618", {"start": v(142.93, -2.48) * mm, "end": v(143.16, -2.43) * mm});
            skLineSegment(sketch, "E1619", {"start": v(143.16, -2.43) * mm, "end": v(143.39, -2.37) * mm});
            skLineSegment(sketch, "E1620", {"start": v(143.39, -2.37) * mm, "end": v(143.6, -2.31) * mm});
            skLineSegment(sketch, "E1621", {"start": v(143.6, -2.31) * mm, "end": v(143.83, -2.26) * mm});
            skLineSegment(sketch, "E1622", {"start": v(143.83, -2.26) * mm, "end": v(144.04, -2.2) * mm});
            skLineSegment(sketch, "E1623", {"start": v(144.04, -2.2) * mm, "end": v(144.26, -2.15) * mm});
            skLineSegment(sketch, "E1624", {"start": v(144.26, -2.15) * mm, "end": v(144.46, -2.1) * mm});
            skLineSegment(sketch, "E1625", {"start": v(144.46, -2.1) * mm, "end": v(144.67, -2.05) * mm});
            skLineSegment(sketch, "E1626", {"start": v(144.67, -2.05) * mm, "end": v(144.87, -2) * mm});
            skLineSegment(sketch, "E1627", {"start": v(144.87, -2) * mm, "end": v(145.07, -1.95) * mm});
            skLineSegment(sketch, "E1628", {"start": v(145.07, -1.95) * mm, "end": v(145.26, -1.9) * mm});
            skLineSegment(sketch, "E1629", {"start": v(145.26, -1.9) * mm, "end": v(145.45, -1.85) * mm});
            skLineSegment(sketch, "E1630", {"start": v(145.45, -1.85) * mm, "end": v(145.63, -1.8) * mm});
            skLineSegment(sketch, "E1631", {"start": v(145.63, -1.8) * mm, "end": v(145.8, -1.76) * mm});
            skLineSegment(sketch, "E1632", {"start": v(145.8, -1.76) * mm, "end": v(145.99, -1.71) * mm});
            skLineSegment(sketch, "E1633", {"start": v(145.99, -1.71) * mm, "end": v(146.16, -1.67) * mm});
            skLineSegment(sketch, "E1634", {"start": v(146.16, -1.67) * mm, "end": v(146.33, -1.63) * mm});
            skLineSegment(sketch, "E1635", {"start": v(146.33, -1.63) * mm, "end": v(146.5, -1.59) * mm});
            skLineSegment(sketch, "E1636", {"start": v(146.5, -1.59) * mm, "end": v(146.65, -1.55) * mm});
            skLineSegment(sketch, "E1637", {"start": v(146.65, -1.55) * mm, "end": v(146.8, -1.5) * mm});
            skLineSegment(sketch, "E1638", {"start": v(146.8, -1.5) * mm, "end": v(146.96, -1.47) * mm});
            skLineSegment(sketch, "E1639", {"start": v(146.96, -1.47) * mm, "end": v(147.1, -1.43) * mm});
            skLineSegment(sketch, "E1640", {"start": v(147.1, -1.43) * mm, "end": v(147.25, -1.4) * mm});
            skLineSegment(sketch, "E1641", {"start": v(147.25, -1.4) * mm, "end": v(147.39, -1.36) * mm});
            skLineSegment(sketch, "E1642", {"start": v(147.39, -1.36) * mm, "end": v(147.52, -1.33) * mm});
            skLineSegment(sketch, "E1643", {"start": v(147.52, -1.33) * mm, "end": v(147.65, -1.3) * mm});
            skLineSegment(sketch, "E1644", {"start": v(147.65, -1.3) * mm, "end": v(147.77, -1.26) * mm});
            skLineSegment(sketch, "E1645", {"start": v(147.77, -1.26) * mm, "end": v(147.9, -1.23) * mm});
            skLineSegment(sketch, "E1646", {"start": v(147.9, -1.23) * mm, "end": v(148, -1.2) * mm});
            skLineSegment(sketch, "E1647", {"start": v(148, -1.2) * mm, "end": v(148.12, -1.17) * mm});
            skLineSegment(sketch, "E1648", {"start": v(148.12, -1.17) * mm, "end": v(148.22, -1.15) * mm});
            skLineSegment(sketch, "E1649", {"start": v(148.22, -1.15) * mm, "end": v(148.32, -1.12) * mm});
            skLineSegment(sketch, "E1650", {"start": v(148.32, -1.12) * mm, "end": v(148.41, -1.1) * mm});
            skLineSegment(sketch, "E1651", {"start": v(148.41, -1.1) * mm, "end": v(148.5, -1.08) * mm});
            skLineSegment(sketch, "E1652", {"start": v(148.5, -1.08) * mm, "end": v(148.58, -1.06) * mm});
            skLineSegment(sketch, "E1653", {"start": v(148.58, -1.06) * mm, "end": v(148.66, -1.04) * mm});
            skLineSegment(sketch, "E1654", {"start": v(148.66, -1.04) * mm, "end": v(148.73, -1.02) * mm});
            skLineSegment(sketch, "E1655", {"start": v(148.73, -1.02) * mm, "end": v(148.8, -1) * mm});
            skLineSegment(sketch, "E1656", {"start": v(148.8, -1) * mm, "end": v(148.85, -0.99) * mm});
            skLineSegment(sketch, "E1657", {"start": v(148.85, -0.99) * mm, "end": v(148.9, -0.97) * mm});
            skLineSegment(sketch, "E1658", {"start": v(148.9, -0.97) * mm, "end": v(148.95, -0.96) * mm});
            skLineSegment(sketch, "E1659", {"start": v(148.95, -0.96) * mm, "end": v(148.99, -0.95) * mm});
            skLineSegment(sketch, "E1660", {"start": v(148.99, -0.95) * mm, "end": v(149.03, -0.94) * mm});
            skLineSegment(sketch, "E1661", {"start": v(149.03, -0.94) * mm, "end": v(149.06, -0.93) * mm});
            skLineSegment(sketch, "E1662", {"start": v(149.06, -0.93) * mm, "end": v(149.09, -0.93) * mm});
            skLineSegment(sketch, "E1663", {"start": v(149.09, -0.93) * mm, "end": v(149.1, -0.92) * mm});
            skLineSegment(sketch, "E1664", {"start": v(149.1, -0.92) * mm, "end": v(149.13, -0.92) * mm});
            skLineSegment(sketch, "E1665", {"start": v(149.13, -0.92) * mm, "end": v(149.15, -0.91) * mm});
            skLineSegment(sketch, "E1666", {"start": v(149.15, -0.91) * mm, "end": v(149.16, -0.9) * mm});
            skLineSegment(sketch, "E1667", {"start": v(149.16, -0.9) * mm, "end": v(149.17, -0.9) * mm});
            skLineSegment(sketch, "E1668", {"start": v(149.17, -0.9) * mm, "end": v(149.18, -0.9) * mm});
            skLineSegment(sketch, "E1669", {"start": v(149.18, -0.9) * mm, "end": v(149.19, -0.9) * mm});
            skLineSegment(sketch, "E1670", {"start": v(149.19, -0.9) * mm, "end": v(149.2, -0.9) * mm});
            skLineSegment(sketch, "E1671", {"start": v(149.2, -0.9) * mm, "end": v(149.2, -0.9) * mm});
            skLineSegment(sketch, "E1672", {"start": v(149.2, -0.9) * mm, "end": v(150, -0.7) * mm});
            skLineSegment(sketch, "E1673", {"start": v(150, 0.7) * mm, "end": v(150, -0.7) * mm});
            skLineSegment(sketch, "E1674", {"start": v(-60.95, -23.4) * mm, "end": v(-52.95, -23.4) * mm});
            skLineSegment(sketch, "E1675", {"start": v(-60.95, -31.4) * mm, "end": v(-60.95, -23.4) * mm});
            skLineSegment(sketch, "E1676", {"start": v(-52.95, -31.35) * mm, "end": v(-52.95, -23.4) * mm});
            skLineSegment(sketch, "E1677", {"start": v(-140.45, 13.88) * mm, "end": v(-140.2, 14.08) * mm});
            skLineSegment(sketch, "E1678", {"start": v(-140.2, 14.08) * mm, "end": v(-139.94, 14.28) * mm});
            skLineSegment(sketch, "E1679", {"start": v(-139.94, 14.28) * mm, "end": v(-139.69, 14.48) * mm});
            skLineSegment(sketch, "E1680", {"start": v(-139.69, 14.48) * mm, "end": v(-139.43, 14.68) * mm});
            skLineSegment(sketch, "E1681", {"start": v(-139.43, 14.68) * mm, "end": v(-139.16, 14.88) * mm});
            skLineSegment(sketch, "E1682", {"start": v(-139.16, 14.88) * mm, "end": v(-138.9, 15.08) * mm});
            skLineSegment(sketch, "E1683", {"start": v(-138.9, 15.08) * mm, "end": v(-138.62, 15.28) * mm});
            skLineSegment(sketch, "E1684", {"start": v(-138.62, 15.28) * mm, "end": v(-138.34, 15.47) * mm});
            skLineSegment(sketch, "E1685", {"start": v(-138.34, 15.47) * mm, "end": v(-138.06, 15.67) * mm});
            skLineSegment(sketch, "E1686", {"start": v(-138.06, 15.67) * mm, "end": v(-137.78, 15.87) * mm});
            skLineSegment(sketch, "E1687", {"start": v(-137.78, 15.87) * mm, "end": v(-137.5, 16.06) * mm});
            skLineSegment(sketch, "E1688", {"start": v(-137.5, 16.06) * mm, "end": v(-137.2, 16.25) * mm});
            skLineSegment(sketch, "E1689", {"start": v(-137.2, 16.25) * mm, "end": v(-136.9, 16.45) * mm});
            skLineSegment(sketch, "E1690", {"start": v(-136.9, 16.45) * mm, "end": v(-136.6, 16.64) * mm});
            skLineSegment(sketch, "E1691", {"start": v(-136.6, 16.64) * mm, "end": v(-136.3, 16.83) * mm});
            skLineSegment(sketch, "E1692", {"start": v(-136.3, 16.83) * mm, "end": v(-136, 17.02) * mm});
            skLineSegment(sketch, "E1693", {"start": v(-136, 17.02) * mm, "end": v(-135.68, 17.21) * mm});
            skLineSegment(sketch, "E1694", {"start": v(-135.68, 17.21) * mm, "end": v(-135.36, 17.4) * mm});
            skLineSegment(sketch, "E1695", {"start": v(-135.36, 17.4) * mm, "end": v(-135.05, 17.59) * mm});
            skLineSegment(sketch, "E1696", {"start": v(-135.05, 17.59) * mm, "end": v(-134.72, 17.77) * mm});
            skLineSegment(sketch, "E1697", {"start": v(-134.72, 17.77) * mm, "end": v(-134.4, 17.96) * mm});
            skLineSegment(sketch, "E1698", {"start": v(-134.4, 17.96) * mm, "end": v(-134.07, 18.15) * mm});
            skLineSegment(sketch, "E1699", {"start": v(-134.07, 18.15) * mm, "end": v(-133.73, 18.33) * mm});
            skLineSegment(sketch, "E1700", {"start": v(-133.73, 18.33) * mm, "end": v(-133.4, 18.51) * mm});
            skLineSegment(sketch, "E1701", {"start": v(-133.4, 18.51) * mm, "end": v(-133.05, 18.7) * mm});
            skLineSegment(sketch, "E1702", {"start": v(-133.05, 18.7) * mm, "end": v(-132.7, 18.88) * mm});
            skLineSegment(sketch, "E1703", {"start": v(-132.7, 18.88) * mm, "end": v(-132.36, 19.06) * mm});
            skLineSegment(sketch, "E1704", {"start": v(-132.36, 19.06) * mm, "end": v(-132, 19.24) * mm});
            skLineSegment(sketch, "E1705", {"start": v(-132, 19.24) * mm, "end": v(-131.65, 19.42) * mm});
            skLineSegment(sketch, "E1706", {"start": v(-131.65, 19.42) * mm, "end": v(-131.29, 19.6) * mm});
            skLineSegment(sketch, "E1707", {"start": v(-131.29, 19.6) * mm, "end": v(-130.92, 19.77) * mm});
            skLineSegment(sketch, "E1708", {"start": v(-130.92, 19.77) * mm, "end": v(-130.55, 19.94) * mm});
            skLineSegment(sketch, "E1709", {"start": v(-130.55, 19.94) * mm, "end": v(-130.18, 20.12) * mm});
            skLineSegment(sketch, "E1710", {"start": v(-130.18, 20.12) * mm, "end": v(-129.8, 20.3) * mm});
            skLineSegment(sketch, "E1711", {"start": v(-129.8, 20.3) * mm, "end": v(-129.43, 20.46) * mm});
            skLineSegment(sketch, "E1712", {"start": v(-129.43, 20.46) * mm, "end": v(-129.05, 20.64) * mm});
            skLineSegment(sketch, "E1713", {"start": v(-129.05, 20.64) * mm, "end": v(-128.66, 20.8) * mm});
            skLineSegment(sketch, "E1714", {"start": v(-128.66, 20.8) * mm, "end": v(-128.27, 20.97) * mm});
            skLineSegment(sketch, "E1715", {"start": v(-128.27, 20.97) * mm, "end": v(-127.88, 21.14) * mm});
            skLineSegment(sketch, "E1716", {"start": v(-127.88, 21.14) * mm, "end": v(-127.48, 21.3) * mm});
            skLineSegment(sketch, "E1717", {"start": v(-127.48, 21.3) * mm, "end": v(-127.08, 21.47) * mm});
            skLineSegment(sketch, "E1718", {"start": v(-127.08, 21.47) * mm, "end": v(-126.68, 21.64) * mm});
            skLineSegment(sketch, "E1719", {"start": v(-126.68, 21.64) * mm, "end": v(-126.27, 21.8) * mm});
            skLineSegment(sketch, "E1720", {"start": v(-126.27, 21.8) * mm, "end": v(-125.86, 21.96) * mm});
            skLineSegment(sketch, "E1721", {"start": v(-125.86, 21.96) * mm, "end": v(-125.44, 22.13) * mm});
            skLineSegment(sketch, "E1722", {"start": v(-125.44, 22.13) * mm, "end": v(-125.02, 22.29) * mm});
            skLineSegment(sketch, "E1723", {"start": v(-125.02, 22.29) * mm, "end": v(-124.6, 22.44) * mm});
            skLineSegment(sketch, "E1724", {"start": v(-124.6, 22.44) * mm, "end": v(-124.18, 22.6) * mm});
            skLineSegment(sketch, "E1725", {"start": v(-124.18, 22.6) * mm, "end": v(-123.75, 22.76) * mm});
            skLineSegment(sketch, "E1726", {"start": v(-123.75, 22.76) * mm, "end": v(-123.32, 22.91) * mm});
            skLineSegment(sketch, "E1727", {"start": v(-123.32, 22.91) * mm, "end": v(-122.88, 23.07) * mm});
            skLineSegment(sketch, "E1728", {"start": v(-122.88, 23.07) * mm, "end": v(-122.44, 23.22) * mm});
            skLineSegment(sketch, "E1729", {"start": v(-122.44, 23.22) * mm, "end": v(-122, 23.37) * mm});
            skLineSegment(sketch, "E1730", {"start": v(-122, 23.37) * mm, "end": v(-121.55, 23.52) * mm});
            skLineSegment(sketch, "E1731", {"start": v(-121.55, 23.52) * mm, "end": v(-121.1, 23.67) * mm});
            skLineSegment(sketch, "E1732", {"start": v(-121.1, 23.67) * mm, "end": v(-120.65, 23.82) * mm});
            skLineSegment(sketch, "E1733", {"start": v(-120.65, 23.82) * mm, "end": v(-120.2, 23.96) * mm});
            skLineSegment(sketch, "E1734", {"start": v(-120.2, 23.96) * mm, "end": v(-119.73, 24.1) * mm});
            skLineSegment(sketch, "E1735", {"start": v(-119.73, 24.1) * mm, "end": v(-119.27, 24.25) * mm});
            skLineSegment(sketch, "E1736", {"start": v(-119.27, 24.25) * mm, "end": v(-118.8, 24.4) * mm});
            skLineSegment(sketch, "E1737", {"start": v(-118.8, 24.4) * mm, "end": v(-118.34, 24.54) * mm});
            skLineSegment(sketch, "E1738", {"start": v(-118.34, 24.54) * mm, "end": v(-117.86, 24.68) * mm});
            skLineSegment(sketch, "E1739", {"start": v(-117.86, 24.68) * mm, "end": v(-117.39, 24.82) * mm});
            skLineSegment(sketch, "E1740", {"start": v(-117.39, 24.82) * mm, "end": v(-116.9, 24.95) * mm});
            skLineSegment(sketch, "E1741", {"start": v(-116.9, 24.95) * mm, "end": v(-116.42, 25.09) * mm});
            skLineSegment(sketch, "E1742", {"start": v(-116.42, 25.09) * mm, "end": v(-115.94, 25.22) * mm});
            skLineSegment(sketch, "E1743", {"start": v(-115.94, 25.22) * mm, "end": v(-115.45, 25.36) * mm});
            skLineSegment(sketch, "E1744", {"start": v(-115.45, 25.36) * mm, "end": v(-114.96, 25.49) * mm});
            skLineSegment(sketch, "E1745", {"start": v(-114.96, 25.49) * mm, "end": v(-114.46, 25.62) * mm});
            skLineSegment(sketch, "E1746", {"start": v(-114.46, 25.62) * mm, "end": v(-113.96, 25.75) * mm});
            skLineSegment(sketch, "E1747", {"start": v(-113.96, 25.75) * mm, "end": v(-113.46, 25.88) * mm});
            skLineSegment(sketch, "E1748", {"start": v(-113.46, 25.88) * mm, "end": v(-112.95, 26) * mm});
            skLineSegment(sketch, "E1749", {"start": v(-112.95, 26) * mm, "end": v(-112.45, 26.13) * mm});
            skLineSegment(sketch, "E1750", {"start": v(-112.45, 26.13) * mm, "end": v(-111.93, 26.25) * mm});
            skLineSegment(sketch, "E1751", {"start": v(-111.93, 26.25) * mm, "end": v(-111.42, 26.38) * mm});
            skLineSegment(sketch, "E1752", {"start": v(-111.42, 26.38) * mm, "end": v(-110.9, 26.5) * mm});
            skLineSegment(sketch, "E1753", {"start": v(-110.9, 26.5) * mm, "end": v(-110.38, 26.62) * mm});
            skLineSegment(sketch, "E1754", {"start": v(-110.38, 26.62) * mm, "end": v(-109.86, 26.74) * mm});
            skLineSegment(sketch, "E1755", {"start": v(-109.86, 26.74) * mm, "end": v(-109.33, 26.85) * mm});
            skLineSegment(sketch, "E1756", {"start": v(-109.33, 26.85) * mm, "end": v(-108.8, 26.97) * mm});
            skLineSegment(sketch, "E1757", {"start": v(-108.8, 26.97) * mm, "end": v(-108.27, 27.08) * mm});
            skLineSegment(sketch, "E1758", {"start": v(-108.27, 27.08) * mm, "end": v(-107.73, 27.2) * mm});
            skLineSegment(sketch, "E1759", {"start": v(-107.73, 27.2) * mm, "end": v(-107.2, 27.3) * mm});
            skLineSegment(sketch, "E1760", {"start": v(-107.2, 27.3) * mm, "end": v(-106.65, 27.42) * mm});
            skLineSegment(sketch, "E1761", {"start": v(-106.65, 27.42) * mm, "end": v(-106.1, 27.52) * mm});
            skLineSegment(sketch, "E1762", {"start": v(-106.1, 27.52) * mm, "end": v(-105.56, 27.63) * mm});
            skLineSegment(sketch, "E1763", {"start": v(-105.56, 27.63) * mm, "end": v(-105, 27.74) * mm});
            skLineSegment(sketch, "E1764", {"start": v(-105, 27.74) * mm, "end": v(-104.45, 27.84) * mm});
            skLineSegment(sketch, "E1765", {"start": v(-104.45, 27.84) * mm, "end": v(-103.9, 27.94) * mm});
            skLineSegment(sketch, "E1766", {"start": v(-103.9, 27.94) * mm, "end": v(-103.34, 28.04) * mm});
            skLineSegment(sketch, "E1767", {"start": v(-103.34, 28.04) * mm, "end": v(-102.77, 28.14) * mm});
            skLineSegment(sketch, "E1768", {"start": v(-102.77, 28.14) * mm, "end": v(-102.2, 28.24) * mm});
            skLineSegment(sketch, "E1769", {"start": v(-102.2, 28.24) * mm, "end": v(-101.64, 28.34) * mm});
            skLineSegment(sketch, "E1770", {"start": v(-101.64, 28.34) * mm, "end": v(-101.07, 28.43) * mm});
            skLineSegment(sketch, "E1771", {"start": v(-101.07, 28.43) * mm, "end": v(-100.5, 28.53) * mm});
            skLineSegment(sketch, "E1772", {"start": v(-100.5, 28.53) * mm, "end": v(-99.92, 28.62) * mm});
            skLineSegment(sketch, "E1773", {"start": v(-99.92, 28.62) * mm, "end": v(-99.34, 28.71) * mm});
            skLineSegment(sketch, "E1774", {"start": v(-99.34, 28.71) * mm, "end": v(-98.75, 28.8) * mm});
            skLineSegment(sketch, "E1775", {"start": v(-98.75, 28.8) * mm, "end": v(-98.17, 28.89) * mm});
            skLineSegment(sketch, "E1776", {"start": v(-98.17, 28.89) * mm, "end": v(-97.58, 28.97) * mm});
            skLineSegment(sketch, "E1777", {"start": v(-97.58, 28.97) * mm, "end": v(-97, 29.06) * mm});
            skLineSegment(sketch, "E1778", {"start": v(-97, 29.06) * mm, "end": v(-96.4, 29.14) * mm});
            skLineSegment(sketch, "E1779", {"start": v(-96.4, 29.14) * mm, "end": v(-95.8, 29.22) * mm});
            skLineSegment(sketch, "E1780", {"start": v(-95.8, 29.22) * mm, "end": v(-95.2, 29.3) * mm});
            skLineSegment(sketch, "E1781", {"start": v(-95.2, 29.3) * mm, "end": v(-94.6, 29.38) * mm});
            skLineSegment(sketch, "E1782", {"start": v(-94.6, 29.38) * mm, "end": v(-94, 29.46) * mm});
            skLineSegment(sketch, "E1783", {"start": v(-94, 29.46) * mm, "end": v(-93.4, 29.54) * mm});
            skLineSegment(sketch, "E1784", {"start": v(-93.4, 29.54) * mm, "end": v(-92.78, 29.61) * mm});
            skLineSegment(sketch, "E1785", {"start": v(-92.78, 29.61) * mm, "end": v(-92.17, 29.68) * mm});
            skLineSegment(sketch, "E1786", {"start": v(-92.17, 29.68) * mm, "end": v(-91.56, 29.76) * mm});
            skLineSegment(sketch, "E1787", {"start": v(-91.56, 29.76) * mm, "end": v(-90.94, 29.83) * mm});
            skLineSegment(sketch, "E1788", {"start": v(-90.94, 29.83) * mm, "end": v(-90.32, 29.9) * mm});
            skLineSegment(sketch, "E1789", {"start": v(-90.32, 29.9) * mm, "end": v(-89.7, 29.96) * mm});
            skLineSegment(sketch, "E1790", {"start": v(-89.7, 29.96) * mm, "end": v(-89.07, 30.03) * mm});
            skLineSegment(sketch, "E1791", {"start": v(-89.07, 30.03) * mm, "end": v(-88.45, 30.09) * mm});
            skLineSegment(sketch, "E1792", {"start": v(-88.45, 30.09) * mm, "end": v(-87.82, 30.15) * mm});
            skLineSegment(sketch, "E1793", {"start": v(-87.82, 30.15) * mm, "end": v(-87.19, 30.21) * mm});
            skLineSegment(sketch, "E1794", {"start": v(-87.19, 30.21) * mm, "end": v(-86.55, 30.27) * mm});
            skLineSegment(sketch, "E1795", {"start": v(-86.55, 30.27) * mm, "end": v(-85.91, 30.33) * mm});
            skLineSegment(sketch, "E1796", {"start": v(-85.91, 30.33) * mm, "end": v(-85.28, 30.39) * mm});
            skLineSegment(sketch, "E1797", {"start": v(-85.28, 30.39) * mm, "end": v(-84.63, 30.44) * mm});
            skLineSegment(sketch, "E1798", {"start": v(-84.63, 30.44) * mm, "end": v(-84, 30.5) * mm});
            skLineSegment(sketch, "E1799", {"start": v(-84, 30.5) * mm, "end": v(-83.34, 30.55) * mm});
            skLineSegment(sketch, "E1800", {"start": v(-83.34, 30.55) * mm, "end": v(-82.7, 30.6) * mm});
            skLineSegment(sketch, "E1801", {"start": v(-82.7, 30.6) * mm, "end": v(-82.04, 30.64) * mm});
            skLineSegment(sketch, "E1802", {"start": v(-82.04, 30.64) * mm, "end": v(-81.4, 30.7) * mm});
            skLineSegment(sketch, "E1803", {"start": v(-81.4, 30.7) * mm, "end": v(-80.74, 30.74) * mm});
            skLineSegment(sketch, "E1804", {"start": v(-80.74, 30.74) * mm, "end": v(-80.08, 30.78) * mm});
            skLineSegment(sketch, "E1805", {"start": v(-80.08, 30.78) * mm, "end": v(-79.42, 30.82) * mm});
            skLineSegment(sketch, "E1806", {"start": v(-79.42, 30.82) * mm, "end": v(-78.76, 30.87) * mm});
            skLineSegment(sketch, "E1807", {"start": v(-78.76, 30.87) * mm, "end": v(-78.1, 30.9) * mm});
            skLineSegment(sketch, "E1808", {"start": v(-78.1, 30.9) * mm, "end": v(-77.43, 30.94) * mm});
            skLineSegment(sketch, "E1809", {"start": v(-77.43, 30.94) * mm, "end": v(-76.76, 30.98) * mm});
            skLineSegment(sketch, "E1810", {"start": v(-76.76, 30.98) * mm, "end": v(-76.09, 31.01) * mm});
            skLineSegment(sketch, "E1811", {"start": v(-76.09, 31.01) * mm, "end": v(-75.42, 31.05) * mm});
            skLineSegment(sketch, "E1812", {"start": v(-75.42, 31.05) * mm, "end": v(-74.74, 31.08) * mm});
            skLineSegment(sketch, "E1813", {"start": v(-74.74, 31.08) * mm, "end": v(-74.06, 31.11) * mm});
            skLineSegment(sketch, "E1814", {"start": v(-74.06, 31.11) * mm, "end": v(-73.38, 31.14) * mm});
            skLineSegment(sketch, "E1815", {"start": v(-73.38, 31.14) * mm, "end": v(-72.7, 31.17) * mm});
            skLineSegment(sketch, "E1816", {"start": v(-72.7, 31.17) * mm, "end": v(-72.02, 31.2) * mm});
            skLineSegment(sketch, "E1817", {"start": v(-72.02, 31.2) * mm, "end": v(-71.34, 31.22) * mm});
            skLineSegment(sketch, "E1818", {"start": v(-71.34, 31.22) * mm, "end": v(-70.65, 31.24) * mm});
            skLineSegment(sketch, "E1819", {"start": v(-70.65, 31.24) * mm, "end": v(-69.96, 31.26) * mm});
            skLineSegment(sketch, "E1820", {"start": v(-69.96, 31.26) * mm, "end": v(-69.27, 31.28) * mm});
            skLineSegment(sketch, "E1821", {"start": v(-69.27, 31.28) * mm, "end": v(-68.58, 31.3) * mm});
            skLineSegment(sketch, "E1822", {"start": v(-68.58, 31.3) * mm, "end": v(-67.88, 31.32) * mm});
            skLineSegment(sketch, "E1823", {"start": v(-67.88, 31.32) * mm, "end": v(-67.18, 31.34) * mm});
            skLineSegment(sketch, "E1824", {"start": v(-67.18, 31.34) * mm, "end": v(-66.49, 31.35) * mm});
            skLineSegment(sketch, "E1825", {"start": v(-66.49, 31.35) * mm, "end": v(-65.79, 31.36) * mm});
            skLineSegment(sketch, "E1826", {"start": v(-65.79, 31.36) * mm, "end": v(-65.08, 31.37) * mm});
            skLineSegment(sketch, "E1827", {"start": v(-65.08, 31.37) * mm, "end": v(-64.38, 31.38) * mm});
            skLineSegment(sketch, "E1828", {"start": v(-64.38, 31.38) * mm, "end": v(-63.67, 31.4) * mm});
            skLineSegment(sketch, "E1829", {"start": v(-63.67, 31.4) * mm, "end": v(-62.97, 31.4) * mm});
            skLineSegment(sketch, "E1830", {"start": v(-62.97, 31.4) * mm, "end": v(-62.26, 31.4) * mm});
            skLineSegment(sketch, "E1831", {"start": v(-62.26, 31.4) * mm, "end": v(-61.55, 31.4) * mm});
            skLineSegment(sketch, "E1832", {"start": v(-61.55, 31.4) * mm, "end": v(-60.83, 31.41) * mm});
            skLineSegment(sketch, "E1833", {"start": v(-60.83, 31.41) * mm, "end": v(-60.12, 31.41) * mm});
            skLineSegment(sketch, "E1834", {"start": v(-60.12, 31.41) * mm, "end": v(-59.4, 31.41) * mm});
            skLineSegment(sketch, "E1835", {"start": v(-59.4, 31.41) * mm, "end": v(-58.67, 31.41) * mm});
            skLineSegment(sketch, "E1836", {"start": v(-58.67, 31.41) * mm, "end": v(-57.95, 31.4) * mm});
            skLineSegment(sketch, "E1837", {"start": v(-57.95, 31.4) * mm, "end": v(-57.22, 31.4) * mm});
            skLineSegment(sketch, "E1838", {"start": v(-57.22, 31.4) * mm, "end": v(-56.5, 31.4) * mm});
            skLineSegment(sketch, "E1839", {"start": v(-56.5, 31.4) * mm, "end": v(-55.76, 31.4) * mm});
            skLineSegment(sketch, "E1840", {"start": v(-55.76, 31.4) * mm, "end": v(-55.03, 31.38) * mm});
            skLineSegment(sketch, "E1841", {"start": v(-55.03, 31.38) * mm, "end": v(-54.3, 31.37) * mm});
            skLineSegment(sketch, "E1842", {"start": v(-54.3, 31.37) * mm, "end": v(-53.56, 31.36) * mm});
            skLineSegment(sketch, "E1843", {"start": v(-53.56, 31.36) * mm, "end": v(-52.83, 31.35) * mm});
            skLineSegment(sketch, "E1844", {"start": v(-52.83, 31.35) * mm, "end": v(-52.1, 31.34) * mm});
            skLineSegment(sketch, "E1845", {"start": v(-52.1, 31.34) * mm, "end": v(-51.35, 31.32) * mm});
            skLineSegment(sketch, "E1846", {"start": v(-51.35, 31.32) * mm, "end": v(-50.61, 31.3) * mm});
            skLineSegment(sketch, "E1847", {"start": v(-50.61, 31.3) * mm, "end": v(-49.87, 31.29) * mm});
            skLineSegment(sketch, "E1848", {"start": v(-49.87, 31.29) * mm, "end": v(-49.13, 31.27) * mm});
            skLineSegment(sketch, "E1849", {"start": v(-49.13, 31.27) * mm, "end": v(-48.38, 31.25) * mm});
            skLineSegment(sketch, "E1850", {"start": v(-48.38, 31.25) * mm, "end": v(-47.64, 31.22) * mm});
            skLineSegment(sketch, "E1851", {"start": v(-47.64, 31.22) * mm, "end": v(-46.9, 31.2) * mm});
            skLineSegment(sketch, "E1852", {"start": v(-46.9, 31.2) * mm, "end": v(-46.14, 31.18) * mm});
            skLineSegment(sketch, "E1853", {"start": v(-46.14, 31.18) * mm, "end": v(-45.4, 31.15) * mm});
            skLineSegment(sketch, "E1854", {"start": v(-45.4, 31.15) * mm, "end": v(-44.64, 31.12) * mm});
            skLineSegment(sketch, "E1855", {"start": v(-44.64, 31.12) * mm, "end": v(-43.9, 31.1) * mm});
            skLineSegment(sketch, "E1856", {"start": v(-43.9, 31.1) * mm, "end": v(-43.14, 31.06) * mm});
            skLineSegment(sketch, "E1857", {"start": v(-43.14, 31.06) * mm, "end": v(-42.39, 31.03) * mm});
            skLineSegment(sketch, "E1858", {"start": v(-42.39, 31.03) * mm, "end": v(-41.63, 31) * mm});
            skLineSegment(sketch, "E1859", {"start": v(-41.63, 31) * mm, "end": v(-40.87, 30.97) * mm});
            skLineSegment(sketch, "E1860", {"start": v(-40.87, 30.97) * mm, "end": v(-40.12, 30.93) * mm});
            skLineSegment(sketch, "E1861", {"start": v(-40.12, 30.93) * mm, "end": v(-39.36, 30.9) * mm});
            skLineSegment(sketch, "E1862", {"start": v(-39.36, 30.9) * mm, "end": v(-38.6, 30.86) * mm});
            skLineSegment(sketch, "E1863", {"start": v(-38.6, 30.86) * mm, "end": v(-37.84, 30.82) * mm});
            skLineSegment(sketch, "E1864", {"start": v(-37.84, 30.82) * mm, "end": v(-37.08, 30.78) * mm});
            skLineSegment(sketch, "E1865", {"start": v(-37.08, 30.78) * mm, "end": v(-36.31, 30.74) * mm});
            skLineSegment(sketch, "E1866", {"start": v(-36.31, 30.74) * mm, "end": v(-35.55, 30.7) * mm});
            skLineSegment(sketch, "E1867", {"start": v(-35.55, 30.7) * mm, "end": v(-34.79, 30.65) * mm});
            skLineSegment(sketch, "E1868", {"start": v(-34.79, 30.65) * mm, "end": v(-34.02, 30.6) * mm});
            skLineSegment(sketch, "E1869", {"start": v(-34.02, 30.6) * mm, "end": v(-33.25, 30.56) * mm});
            skLineSegment(sketch, "E1870", {"start": v(-33.25, 30.56) * mm, "end": v(-32.49, 30.51) * mm});
            skLineSegment(sketch, "E1871", {"start": v(-32.49, 30.51) * mm, "end": v(-31.72, 30.47) * mm});
            skLineSegment(sketch, "E1872", {"start": v(-31.72, 30.47) * mm, "end": v(-30.95, 30.42) * mm});
            skLineSegment(sketch, "E1873", {"start": v(-30.95, 30.42) * mm, "end": v(-30.18, 30.37) * mm});
            skLineSegment(sketch, "E1874", {"start": v(-30.18, 30.37) * mm, "end": v(-29.4, 30.31) * mm});
            skLineSegment(sketch, "E1875", {"start": v(-29.4, 30.31) * mm, "end": v(-28.64, 30.26) * mm});
            skLineSegment(sketch, "E1876", {"start": v(-28.64, 30.26) * mm, "end": v(-27.87, 30.2) * mm});
            skLineSegment(sketch, "E1877", {"start": v(-27.87, 30.2) * mm, "end": v(-27.1, 30.15) * mm});
            skLineSegment(sketch, "E1878", {"start": v(-27.1, 30.15) * mm, "end": v(-26.32, 30.1) * mm});
            skLineSegment(sketch, "E1879", {"start": v(-26.32, 30.1) * mm, "end": v(-25.55, 30.04) * mm});
            skLineSegment(sketch, "E1880", {"start": v(-25.55, 30.04) * mm, "end": v(-24.77, 29.98) * mm});
            skLineSegment(sketch, "E1881", {"start": v(-24.77, 29.98) * mm, "end": v(-24, 29.92) * mm});
            skLineSegment(sketch, "E1882", {"start": v(-24, 29.92) * mm, "end": v(-23.22, 29.86) * mm});
            skLineSegment(sketch, "E1883", {"start": v(-23.22, 29.86) * mm, "end": v(-22.44, 29.8) * mm});
            skLineSegment(sketch, "E1884", {"start": v(-22.44, 29.8) * mm, "end": v(-21.66, 29.73) * mm});
            skLineSegment(sketch, "E1885", {"start": v(-21.66, 29.73) * mm, "end": v(-20.89, 29.67) * mm});
            skLineSegment(sketch, "E1886", {"start": v(-20.89, 29.67) * mm, "end": v(-20.1, 29.6) * mm});
            skLineSegment(sketch, "E1887", {"start": v(-20.1, 29.6) * mm, "end": v(-19.33, 29.54) * mm});
            skLineSegment(sketch, "E1888", {"start": v(-19.33, 29.54) * mm, "end": v(-18.55, 29.47) * mm});
            skLineSegment(sketch, "E1889", {"start": v(-18.55, 29.47) * mm, "end": v(-17.77, 29.4) * mm});
            skLineSegment(sketch, "E1890", {"start": v(-17.77, 29.4) * mm, "end": v(-16.99, 29.33) * mm});
            skLineSegment(sketch, "E1891", {"start": v(-16.99, 29.33) * mm, "end": v(-16.2, 29.26) * mm});
            skLineSegment(sketch, "E1892", {"start": v(-16.2, 29.26) * mm, "end": v(-15.42, 29.19) * mm});
            skLineSegment(sketch, "E1893", {"start": v(-15.42, 29.19) * mm, "end": v(-14.64, 29.12) * mm});
            skLineSegment(sketch, "E1894", {"start": v(-14.64, 29.12) * mm, "end": v(-13.86, 29.04) * mm});
            skLineSegment(sketch, "E1895", {"start": v(-13.86, 29.04) * mm, "end": v(-13.08, 28.97) * mm});
            skLineSegment(sketch, "E1896", {"start": v(-13.08, 28.97) * mm, "end": v(-12.3, 28.9) * mm});
            skLineSegment(sketch, "E1897", {"start": v(-12.3, 28.9) * mm, "end": v(-11.5, 28.82) * mm});
            skLineSegment(sketch, "E1898", {"start": v(-11.5, 28.82) * mm, "end": v(-10.73, 28.74) * mm});
            skLineSegment(sketch, "E1899", {"start": v(-10.73, 28.74) * mm, "end": v(-9.94, 28.66) * mm});
            skLineSegment(sketch, "E1900", {"start": v(-9.94, 28.66) * mm, "end": v(-9.16, 28.58) * mm});
            skLineSegment(sketch, "E1901", {"start": v(-9.16, 28.58) * mm, "end": v(-8.37, 28.5) * mm});
            skLineSegment(sketch, "E1902", {"start": v(-8.37, 28.5) * mm, "end": v(-7.59, 28.42) * mm});
            skLineSegment(sketch, "E1903", {"start": v(-7.59, 28.42) * mm, "end": v(-6.8, 28.34) * mm});
            skLineSegment(sketch, "E1904", {"start": v(-6.8, 28.34) * mm, "end": v(-6.02, 28.26) * mm});
            skLineSegment(sketch, "E1905", {"start": v(-6.02, 28.26) * mm, "end": v(-5.23, 28.17) * mm});
            skLineSegment(sketch, "E1906", {"start": v(-5.23, 28.17) * mm, "end": v(-4.45, 28.09) * mm});
            skLineSegment(sketch, "E1907", {"start": v(-4.45, 28.09) * mm, "end": v(-3.66, 28) * mm});
            skLineSegment(sketch, "E1908", {"start": v(-3.66, 28) * mm, "end": v(-2.88, 27.92) * mm});
            skLineSegment(sketch, "E1909", {"start": v(-2.88, 27.92) * mm, "end": v(-2.1, 27.83) * mm});
            skLineSegment(sketch, "E1910", {"start": v(-2.1, 27.83) * mm, "end": v(-1.3, 27.74) * mm});
            skLineSegment(sketch, "E1911", {"start": v(-1.3, 27.74) * mm, "end": v(-0.52, 27.65) * mm});
            skLineSegment(sketch, "E1912", {"start": v(-0.52, 27.65) * mm, "end": v(0.27, 27.56) * mm});
            skLineSegment(sketch, "E1913", {"start": v(0.27, 27.56) * mm, "end": v(1.05, 27.47) * mm});
            skLineSegment(sketch, "E1914", {"start": v(1.05, 27.47) * mm, "end": v(1.84, 27.38) * mm});
            skLineSegment(sketch, "E1915", {"start": v(1.84, 27.38) * mm, "end": v(2.62, 27.29) * mm});
            skLineSegment(sketch, "E1916", {"start": v(2.62, 27.29) * mm, "end": v(3.41, 27.2) * mm});
            skLineSegment(sketch, "E1917", {"start": v(3.41, 27.2) * mm, "end": v(4.2, 27.1) * mm});
            skLineSegment(sketch, "E1918", {"start": v(4.2, 27.1) * mm, "end": v(4.98, 27) * mm});
            skLineSegment(sketch, "E1919", {"start": v(4.98, 27) * mm, "end": v(5.77, 26.9) * mm});
            skLineSegment(sketch, "E1920", {"start": v(5.77, 26.9) * mm, "end": v(6.55, 26.81) * mm});
            skLineSegment(sketch, "E1921", {"start": v(6.55, 26.81) * mm, "end": v(7.34, 26.72) * mm});
            skLineSegment(sketch, "E1922", {"start": v(7.34, 26.72) * mm, "end": v(8.12, 26.62) * mm});
            skLineSegment(sketch, "E1923", {"start": v(8.12, 26.62) * mm, "end": v(8.9, 26.52) * mm});
            skLineSegment(sketch, "E1924", {"start": v(8.9, 26.52) * mm, "end": v(9.69, 26.42) * mm});
            skLineSegment(sketch, "E1925", {"start": v(9.69, 26.42) * mm, "end": v(10.47, 26.32) * mm});
            skLineSegment(sketch, "E1926", {"start": v(10.47, 26.32) * mm, "end": v(11.26, 26.22) * mm});
            skLineSegment(sketch, "E1927", {"start": v(11.26, 26.22) * mm, "end": v(12.04, 26.12) * mm});
            skLineSegment(sketch, "E1928", {"start": v(12.04, 26.12) * mm, "end": v(12.82, 26.02) * mm});
            skLineSegment(sketch, "E1929", {"start": v(12.82, 26.02) * mm, "end": v(13.6, 25.92) * mm});
            skLineSegment(sketch, "E1930", {"start": v(13.6, 25.92) * mm, "end": v(14.39, 25.81) * mm});
            skLineSegment(sketch, "E1931", {"start": v(14.39, 25.81) * mm, "end": v(15.17, 25.7) * mm});
            skLineSegment(sketch, "E1932", {"start": v(15.17, 25.7) * mm, "end": v(15.95, 25.6) * mm});
            skLineSegment(sketch, "E1933", {"start": v(15.95, 25.6) * mm, "end": v(16.73, 25.5) * mm});
            skLineSegment(sketch, "E1934", {"start": v(16.73, 25.5) * mm, "end": v(17.51, 25.4) * mm});
            skLineSegment(sketch, "E1935", {"start": v(17.51, 25.4) * mm, "end": v(18.3, 25.29) * mm});
            skLineSegment(sketch, "E1936", {"start": v(18.3, 25.29) * mm, "end": v(19.07, 25.18) * mm});
            skLineSegment(sketch, "E1937", {"start": v(19.07, 25.18) * mm, "end": v(19.85, 25.07) * mm});
            skLineSegment(sketch, "E1938", {"start": v(19.85, 25.07) * mm, "end": v(20.63, 24.96) * mm});
            skLineSegment(sketch, "E1939", {"start": v(20.63, 24.96) * mm, "end": v(21.4, 24.85) * mm});
            skLineSegment(sketch, "E1940", {"start": v(21.4, 24.85) * mm, "end": v(22.19, 24.74) * mm});
            skLineSegment(sketch, "E1941", {"start": v(22.19, 24.74) * mm, "end": v(22.96, 24.63) * mm});
            skLineSegment(sketch, "E1942", {"start": v(22.96, 24.63) * mm, "end": v(23.74, 24.52) * mm});
            skLineSegment(sketch, "E1943", {"start": v(23.74, 24.52) * mm, "end": v(24.51, 24.41) * mm});
            skLineSegment(sketch, "E1944", {"start": v(24.51, 24.41) * mm, "end": v(25.29, 24.3) * mm});
            skLineSegment(sketch, "E1945", {"start": v(25.29, 24.3) * mm, "end": v(26.06, 24.19) * mm});
            skLineSegment(sketch, "E1946", {"start": v(26.06, 24.19) * mm, "end": v(26.84, 24.08) * mm});
            skLineSegment(sketch, "E1947", {"start": v(26.84, 24.08) * mm, "end": v(27.6, 23.96) * mm});
            skLineSegment(sketch, "E1948", {"start": v(27.6, 23.96) * mm, "end": v(28.38, 23.85) * mm});
            skLineSegment(sketch, "E1949", {"start": v(28.38, 23.85) * mm, "end": v(29.15, 23.73) * mm});
            skLineSegment(sketch, "E1950", {"start": v(29.15, 23.73) * mm, "end": v(29.92, 23.62) * mm});
            skLineSegment(sketch, "E1951", {"start": v(29.92, 23.62) * mm, "end": v(30.7, 23.5) * mm});
            skLineSegment(sketch, "E1952", {"start": v(30.7, 23.5) * mm, "end": v(31.46, 23.39) * mm});
            skLineSegment(sketch, "E1953", {"start": v(31.46, 23.39) * mm, "end": v(32.23, 23.27) * mm});
            skLineSegment(sketch, "E1954", {"start": v(32.23, 23.27) * mm, "end": v(33, 23.16) * mm});
            skLineSegment(sketch, "E1955", {"start": v(33, 23.16) * mm, "end": v(33.76, 23.04) * mm});
            skLineSegment(sketch, "E1956", {"start": v(33.76, 23.04) * mm, "end": v(34.53, 22.92) * mm});
            skLineSegment(sketch, "E1957", {"start": v(34.53, 22.92) * mm, "end": v(35.29, 22.8) * mm});
            skLineSegment(sketch, "E1958", {"start": v(35.29, 22.8) * mm, "end": v(36.05, 22.68) * mm});
            skLineSegment(sketch, "E1959", {"start": v(36.05, 22.68) * mm, "end": v(36.81, 22.57) * mm});
            skLineSegment(sketch, "E1960", {"start": v(36.81, 22.57) * mm, "end": v(37.58, 22.45) * mm});
            skLineSegment(sketch, "E1961", {"start": v(37.58, 22.45) * mm, "end": v(38.34, 22.33) * mm});
            skLineSegment(sketch, "E1962", {"start": v(38.34, 22.33) * mm, "end": v(39.1, 22.2) * mm});
            skLineSegment(sketch, "E1963", {"start": v(39.1, 22.2) * mm, "end": v(39.85, 22.09) * mm});
            skLineSegment(sketch, "E1964", {"start": v(39.85, 22.09) * mm, "end": v(40.6, 21.97) * mm});
            skLineSegment(sketch, "E1965", {"start": v(40.6, 21.97) * mm, "end": v(41.36, 21.84) * mm});
            skLineSegment(sketch, "E1966", {"start": v(41.36, 21.84) * mm, "end": v(42.12, 21.72) * mm});
            skLineSegment(sketch, "E1967", {"start": v(42.12, 21.72) * mm, "end": v(42.87, 21.6) * mm});
            skLineSegment(sketch, "E1968", {"start": v(42.87, 21.6) * mm, "end": v(43.63, 21.48) * mm});
            skLineSegment(sketch, "E1969", {"start": v(43.63, 21.48) * mm, "end": v(44.38, 21.36) * mm});
            skLineSegment(sketch, "E1970", {"start": v(44.38, 21.36) * mm, "end": v(45.13, 21.23) * mm});
            skLineSegment(sketch, "E1971", {"start": v(45.13, 21.23) * mm, "end": v(45.87, 21.11) * mm});
            skLineSegment(sketch, "E1972", {"start": v(45.87, 21.11) * mm, "end": v(46.62, 20.99) * mm});
            skLineSegment(sketch, "E1973", {"start": v(46.62, 20.99) * mm, "end": v(47.37, 20.86) * mm});
            skLineSegment(sketch, "E1974", {"start": v(47.37, 20.86) * mm, "end": v(48.11, 20.74) * mm});
            skLineSegment(sketch, "E1975", {"start": v(48.11, 20.74) * mm, "end": v(48.86, 20.61) * mm});
            skLineSegment(sketch, "E1976", {"start": v(48.86, 20.61) * mm, "end": v(49.6, 20.5) * mm});
            skLineSegment(sketch, "E1977", {"start": v(49.6, 20.5) * mm, "end": v(50.34, 20.37) * mm});
            skLineSegment(sketch, "E1978", {"start": v(50.34, 20.37) * mm, "end": v(51.08, 20.24) * mm});
            skLineSegment(sketch, "E1979", {"start": v(51.08, 20.24) * mm, "end": v(51.82, 20.11) * mm});
            skLineSegment(sketch, "E1980", {"start": v(51.82, 20.11) * mm, "end": v(52.55, 19.99) * mm});
            skLineSegment(sketch, "E1981", {"start": v(52.55, 19.99) * mm, "end": v(53.29, 19.86) * mm});
            skLineSegment(sketch, "E1982", {"start": v(53.29, 19.86) * mm, "end": v(54.02, 19.74) * mm});
            skLineSegment(sketch, "E1983", {"start": v(54.02, 19.74) * mm, "end": v(54.75, 19.61) * mm});
            skLineSegment(sketch, "E1984", {"start": v(54.75, 19.61) * mm, "end": v(55.48, 19.48) * mm});
            skLineSegment(sketch, "E1985", {"start": v(55.48, 19.48) * mm, "end": v(56.21, 19.36) * mm});
            skLineSegment(sketch, "E1986", {"start": v(56.21, 19.36) * mm, "end": v(56.94, 19.23) * mm});
            skLineSegment(sketch, "E1987", {"start": v(56.94, 19.23) * mm, "end": v(57.67, 19.1) * mm});
            skLineSegment(sketch, "E1988", {"start": v(57.67, 19.1) * mm, "end": v(58.4, 18.98) * mm});
            skLineSegment(sketch, "E1989", {"start": v(58.4, 18.98) * mm, "end": v(59.11, 18.85) * mm});
            skLineSegment(sketch, "E1990", {"start": v(59.11, 18.85) * mm, "end": v(59.84, 18.72) * mm});
            skLineSegment(sketch, "E1991", {"start": v(59.84, 18.72) * mm, "end": v(60.56, 18.6) * mm});
            skLineSegment(sketch, "E1992", {"start": v(60.56, 18.6) * mm, "end": v(61.27, 18.47) * mm});
            skLineSegment(sketch, "E1993", {"start": v(61.27, 18.47) * mm, "end": v(61.99, 18.34) * mm});
            skLineSegment(sketch, "E1994", {"start": v(61.99, 18.34) * mm, "end": v(62.7, 18.2) * mm});
            skLineSegment(sketch, "E1995", {"start": v(62.7, 18.2) * mm, "end": v(63.42, 18.08) * mm});
            skLineSegment(sketch, "E1996", {"start": v(63.42, 18.08) * mm, "end": v(64.13, 17.95) * mm});
            skLineSegment(sketch, "E1997", {"start": v(64.13, 17.95) * mm, "end": v(64.84, 17.82) * mm});
            skLineSegment(sketch, "E1998", {"start": v(64.84, 17.82) * mm, "end": v(65.54, 17.7) * mm});
            skLineSegment(sketch, "E1999", {"start": v(65.54, 17.7) * mm, "end": v(66.25, 17.57) * mm});
            skLineSegment(sketch, "E2000", {"start": v(66.25, 17.57) * mm, "end": v(66.95, 17.44) * mm});
            skLineSegment(sketch, "E2001", {"start": v(66.95, 17.44) * mm, "end": v(67.66, 17.3) * mm});
            skLineSegment(sketch, "E2002", {"start": v(67.66, 17.3) * mm, "end": v(68.36, 17.18) * mm});
            skLineSegment(sketch, "E2003", {"start": v(68.36, 17.18) * mm, "end": v(69.06, 17.05) * mm});
            skLineSegment(sketch, "E2004", {"start": v(69.06, 17.05) * mm, "end": v(69.75, 16.92) * mm});
            skLineSegment(sketch, "E2005", {"start": v(69.75, 16.92) * mm, "end": v(70.45, 16.8) * mm});
            skLineSegment(sketch, "E2006", {"start": v(70.45, 16.8) * mm, "end": v(71.14, 16.66) * mm});
            skLineSegment(sketch, "E2007", {"start": v(71.14, 16.66) * mm, "end": v(71.83, 16.53) * mm});
            skLineSegment(sketch, "E2008", {"start": v(71.83, 16.53) * mm, "end": v(72.52, 16.4) * mm});
            skLineSegment(sketch, "E2009", {"start": v(72.52, 16.4) * mm, "end": v(73.2, 16.28) * mm});
            skLineSegment(sketch, "E2010", {"start": v(73.2, 16.28) * mm, "end": v(73.9, 16.15) * mm});
            skLineSegment(sketch, "E2011", {"start": v(73.9, 16.15) * mm, "end": v(74.57, 16.02) * mm});
            skLineSegment(sketch, "E2012", {"start": v(74.57, 16.02) * mm, "end": v(75.25, 15.89) * mm});
            skLineSegment(sketch, "E2013", {"start": v(75.25, 15.89) * mm, "end": v(75.93, 15.76) * mm});
            skLineSegment(sketch, "E2014", {"start": v(75.93, 15.76) * mm, "end": v(76.6, 15.63) * mm});
            skLineSegment(sketch, "E2015", {"start": v(76.6, 15.63) * mm, "end": v(77.28, 15.5) * mm});
            skLineSegment(sketch, "E2016", {"start": v(77.28, 15.5) * mm, "end": v(77.96, 15.37) * mm});
            skLineSegment(sketch, "E2017", {"start": v(77.96, 15.37) * mm, "end": v(78.63, 15.24) * mm});
            skLineSegment(sketch, "E2018", {"start": v(78.63, 15.24) * mm, "end": v(79.3, 15.11) * mm});
            skLineSegment(sketch, "E2019", {"start": v(79.3, 15.11) * mm, "end": v(79.96, 14.98) * mm});
            skLineSegment(sketch, "E2020", {"start": v(79.96, 14.98) * mm, "end": v(80.62, 14.86) * mm});
            skLineSegment(sketch, "E2021", {"start": v(80.62, 14.86) * mm, "end": v(81.28, 14.73) * mm});
            skLineSegment(sketch, "E2022", {"start": v(81.28, 14.73) * mm, "end": v(81.94, 14.6) * mm});
            skLineSegment(sketch, "E2023", {"start": v(81.94, 14.6) * mm, "end": v(82.6, 14.47) * mm});
            skLineSegment(sketch, "E2024", {"start": v(82.6, 14.47) * mm, "end": v(83.26, 14.34) * mm});
            skLineSegment(sketch, "E2025", {"start": v(83.26, 14.34) * mm, "end": v(83.9, 14.21) * mm});
            skLineSegment(sketch, "E2026", {"start": v(83.9, 14.21) * mm, "end": v(84.56, 14.08) * mm});
            skLineSegment(sketch, "E2027", {"start": v(84.56, 14.08) * mm, "end": v(85.2, 13.96) * mm});
            skLineSegment(sketch, "E2028", {"start": v(85.2, 13.96) * mm, "end": v(85.85, 13.83) * mm});
            skLineSegment(sketch, "E2029", {"start": v(85.85, 13.83) * mm, "end": v(86.5, 13.7) * mm});
            skLineSegment(sketch, "E2030", {"start": v(86.5, 13.7) * mm, "end": v(87.14, 13.57) * mm});
            skLineSegment(sketch, "E2031", {"start": v(87.14, 13.57) * mm, "end": v(87.77, 13.44) * mm});
            skLineSegment(sketch, "E2032", {"start": v(87.77, 13.44) * mm, "end": v(88.41, 13.32) * mm});
            skLineSegment(sketch, "E2033", {"start": v(88.41, 13.32) * mm, "end": v(89.04, 13.19) * mm});
            skLineSegment(sketch, "E2034", {"start": v(89.04, 13.19) * mm, "end": v(89.68, 13.06) * mm});
            skLineSegment(sketch, "E2035", {"start": v(89.68, 13.06) * mm, "end": v(90.3, 12.93) * mm});
            skLineSegment(sketch, "E2036", {"start": v(90.3, 12.93) * mm, "end": v(90.93, 12.8) * mm});
            skLineSegment(sketch, "E2037", {"start": v(90.93, 12.8) * mm, "end": v(91.55, 12.68) * mm});
            skLineSegment(sketch, "E2038", {"start": v(91.55, 12.68) * mm, "end": v(92.17, 12.55) * mm});
            skLineSegment(sketch, "E2039", {"start": v(92.17, 12.55) * mm, "end": v(92.8, 12.43) * mm});
            skLineSegment(sketch, "E2040", {"start": v(92.8, 12.43) * mm, "end": v(93.4, 12.3) * mm});
            skLineSegment(sketch, "E2041", {"start": v(93.4, 12.3) * mm, "end": v(94.02, 12.18) * mm});
            skLineSegment(sketch, "E2042", {"start": v(94.02, 12.18) * mm, "end": v(94.63, 12.05) * mm});
            skLineSegment(sketch, "E2043", {"start": v(94.63, 12.05) * mm, "end": v(95.24, 11.93) * mm});
            skLineSegment(sketch, "E2044", {"start": v(95.24, 11.93) * mm, "end": v(95.85, 11.8) * mm});
            skLineSegment(sketch, "E2045", {"start": v(95.85, 11.8) * mm, "end": v(96.45, 11.68) * mm});
            skLineSegment(sketch, "E2046", {"start": v(96.45, 11.68) * mm, "end": v(97.05, 11.55) * mm});
            skLineSegment(sketch, "E2047", {"start": v(97.05, 11.55) * mm, "end": v(97.65, 11.43) * mm});
            skLineSegment(sketch, "E2048", {"start": v(97.65, 11.43) * mm, "end": v(98.25, 11.3) * mm});
            skLineSegment(sketch, "E2049", {"start": v(98.25, 11.3) * mm, "end": v(98.84, 11.18) * mm});
            skLineSegment(sketch, "E2050", {"start": v(98.84, 11.18) * mm, "end": v(99.43, 11.05) * mm});
            skLineSegment(sketch, "E2051", {"start": v(99.43, 11.05) * mm, "end": v(100.02, 10.93) * mm});
            skLineSegment(sketch, "E2052", {"start": v(100.02, 10.93) * mm, "end": v(100.6, 10.8) * mm});
            skLineSegment(sketch, "E2053", {"start": v(100.6, 10.8) * mm, "end": v(101.18, 10.69) * mm});
            skLineSegment(sketch, "E2054", {"start": v(101.18, 10.69) * mm, "end": v(101.76, 10.56) * mm});
            skLineSegment(sketch, "E2055", {"start": v(101.76, 10.56) * mm, "end": v(102.34, 10.44) * mm});
            skLineSegment(sketch, "E2056", {"start": v(102.34, 10.44) * mm, "end": v(102.9, 10.32) * mm});
            skLineSegment(sketch, "E2057", {"start": v(102.9, 10.32) * mm, "end": v(103.48, 10.2) * mm});
            skLineSegment(sketch, "E2058", {"start": v(103.48, 10.2) * mm, "end": v(104.05, 10.08) * mm});
            skLineSegment(sketch, "E2059", {"start": v(104.05, 10.08) * mm, "end": v(104.61, 9.96) * mm});
            skLineSegment(sketch, "E2060", {"start": v(104.61, 9.96) * mm, "end": v(105.17, 9.84) * mm});
            skLineSegment(sketch, "E2061", {"start": v(105.17, 9.84) * mm, "end": v(105.73, 9.72) * mm});
            skLineSegment(sketch, "E2062", {"start": v(105.73, 9.72) * mm, "end": v(106.29, 9.6) * mm});
            skLineSegment(sketch, "E2063", {"start": v(106.29, 9.6) * mm, "end": v(106.84, 9.48) * mm});
            skLineSegment(sketch, "E2064", {"start": v(106.84, 9.48) * mm, "end": v(107.4, 9.36) * mm});
            skLineSegment(sketch, "E2065", {"start": v(107.4, 9.36) * mm, "end": v(107.94, 9.24) * mm});
            skLineSegment(sketch, "E2066", {"start": v(107.94, 9.24) * mm, "end": v(108.48, 9.12) * mm});
            skLineSegment(sketch, "E2067", {"start": v(108.48, 9.12) * mm, "end": v(109.03, 9) * mm});
            skLineSegment(sketch, "E2068", {"start": v(109.03, 9) * mm, "end": v(109.56, 8.89) * mm});
            skLineSegment(sketch, "E2069", {"start": v(109.56, 8.89) * mm, "end": v(110.1, 8.77) * mm});
            skLineSegment(sketch, "E2070", {"start": v(110.1, 8.77) * mm, "end": v(110.63, 8.65) * mm});
            skLineSegment(sketch, "E2071", {"start": v(110.63, 8.65) * mm, "end": v(111.16, 8.54) * mm});
            skLineSegment(sketch, "E2072", {"start": v(111.16, 8.54) * mm, "end": v(111.69, 8.42) * mm});
            skLineSegment(sketch, "E2073", {"start": v(111.69, 8.42) * mm, "end": v(112.21, 8.3) * mm});
            skLineSegment(sketch, "E2074", {"start": v(112.21, 8.3) * mm, "end": v(112.73, 8.2) * mm});
            skLineSegment(sketch, "E2075", {"start": v(112.73, 8.2) * mm, "end": v(113.25, 8.08) * mm});
            skLineSegment(sketch, "E2076", {"start": v(113.25, 8.08) * mm, "end": v(113.76, 7.96) * mm});
            skLineSegment(sketch, "E2077", {"start": v(113.76, 7.96) * mm, "end": v(114.27, 7.85) * mm});
            skLineSegment(sketch, "E2078", {"start": v(114.27, 7.85) * mm, "end": v(114.78, 7.74) * mm});
            skLineSegment(sketch, "E2079", {"start": v(114.78, 7.74) * mm, "end": v(115.29, 7.62) * mm});
            skLineSegment(sketch, "E2080", {"start": v(115.29, 7.62) * mm, "end": v(115.79, 7.51) * mm});
            skLineSegment(sketch, "E2081", {"start": v(115.79, 7.51) * mm, "end": v(116.29, 7.4) * mm});
            skLineSegment(sketch, "E2082", {"start": v(116.29, 7.4) * mm, "end": v(116.78, 7.29) * mm});
            skLineSegment(sketch, "E2083", {"start": v(116.78, 7.29) * mm, "end": v(117.27, 7.18) * mm});
            skLineSegment(sketch, "E2084", {"start": v(117.27, 7.18) * mm, "end": v(117.76, 7.07) * mm});
            skLineSegment(sketch, "E2085", {"start": v(117.76, 7.07) * mm, "end": v(118.25, 6.96) * mm});
            skLineSegment(sketch, "E2086", {"start": v(118.25, 6.96) * mm, "end": v(118.73, 6.85) * mm});
            skLineSegment(sketch, "E2087", {"start": v(118.73, 6.85) * mm, "end": v(119.2, 6.74) * mm});
            skLineSegment(sketch, "E2088", {"start": v(119.2, 6.74) * mm, "end": v(119.68, 6.63) * mm});
            skLineSegment(sketch, "E2089", {"start": v(119.68, 6.63) * mm, "end": v(120.16, 6.53) * mm});
            skLineSegment(sketch, "E2090", {"start": v(120.16, 6.53) * mm, "end": v(120.63, 6.42) * mm});
            skLineSegment(sketch, "E2091", {"start": v(120.63, 6.42) * mm, "end": v(121.1, 6.31) * mm});
            skLineSegment(sketch, "E2092", {"start": v(121.1, 6.31) * mm, "end": v(121.55, 6.2) * mm});
            skLineSegment(sketch, "E2093", {"start": v(121.55, 6.2) * mm, "end": v(122.01, 6.1) * mm});
            skLineSegment(sketch, "E2094", {"start": v(122.01, 6.1) * mm, "end": v(122.47, 6) * mm});
            skLineSegment(sketch, "E2095", {"start": v(122.47, 6) * mm, "end": v(122.92, 5.9) * mm});
            skLineSegment(sketch, "E2096", {"start": v(122.92, 5.9) * mm, "end": v(123.37, 5.8) * mm});
            skLineSegment(sketch, "E2097", {"start": v(123.37, 5.8) * mm, "end": v(123.82, 5.69) * mm});
            skLineSegment(sketch, "E2098", {"start": v(123.82, 5.69) * mm, "end": v(124.26, 5.59) * mm});
            skLineSegment(sketch, "E2099", {"start": v(124.26, 5.59) * mm, "end": v(124.7, 5.49) * mm});
            skLineSegment(sketch, "E2100", {"start": v(124.7, 5.49) * mm, "end": v(125.13, 5.39) * mm});
            skLineSegment(sketch, "E2101", {"start": v(125.13, 5.39) * mm, "end": v(125.57, 5.28) * mm});
            skLineSegment(sketch, "E2102", {"start": v(125.57, 5.28) * mm, "end": v(126, 5.19) * mm});
            skLineSegment(sketch, "E2103", {"start": v(126, 5.19) * mm, "end": v(126.42, 5.09) * mm});
            skLineSegment(sketch, "E2104", {"start": v(126.42, 5.09) * mm, "end": v(126.84, 4.99) * mm});
            skLineSegment(sketch, "E2105", {"start": v(126.84, 4.99) * mm, "end": v(127.26, 4.9) * mm});
            skLineSegment(sketch, "E2106", {"start": v(127.26, 4.9) * mm, "end": v(127.68, 4.8) * mm});
            skLineSegment(sketch, "E2107", {"start": v(127.68, 4.8) * mm, "end": v(128.09, 4.7) * mm});
            skLineSegment(sketch, "E2108", {"start": v(128.09, 4.7) * mm, "end": v(128.5, 4.6) * mm});
            skLineSegment(sketch, "E2109", {"start": v(128.5, 4.6) * mm, "end": v(128.9, 4.5) * mm});
            skLineSegment(sketch, "E2110", {"start": v(128.9, 4.5) * mm, "end": v(129.3, 4.41) * mm});
            skLineSegment(sketch, "E2111", {"start": v(129.3, 4.41) * mm, "end": v(129.7, 4.32) * mm});
            skLineSegment(sketch, "E2112", {"start": v(129.7, 4.32) * mm, "end": v(130.1, 4.23) * mm});
            skLineSegment(sketch, "E2113", {"start": v(130.1, 4.23) * mm, "end": v(130.48, 4.13) * mm});
            skLineSegment(sketch, "E2114", {"start": v(130.48, 4.13) * mm, "end": v(130.87, 4.04) * mm});
            skLineSegment(sketch, "E2115", {"start": v(130.87, 4.04) * mm, "end": v(131.25, 3.95) * mm});
            skLineSegment(sketch, "E2116", {"start": v(131.25, 3.95) * mm, "end": v(131.63, 3.86) * mm});
            skLineSegment(sketch, "E2117", {"start": v(131.63, 3.86) * mm, "end": v(132, 3.77) * mm});
            skLineSegment(sketch, "E2118", {"start": v(132, 3.77) * mm, "end": v(132.38, 3.68) * mm});
            skLineSegment(sketch, "E2119", {"start": v(132.38, 3.68) * mm, "end": v(132.75, 3.6) * mm});
            skLineSegment(sketch, "E2120", {"start": v(132.75, 3.6) * mm, "end": v(133.11, 3.5) * mm});
            skLineSegment(sketch, "E2121", {"start": v(133.11, 3.5) * mm, "end": v(133.47, 3.42) * mm});
            skLineSegment(sketch, "E2122", {"start": v(133.47, 3.42) * mm, "end": v(133.83, 3.34) * mm});
            skLineSegment(sketch, "E2123", {"start": v(150, -0.7) * mm, "end": v(150, 0.7) * mm});
            skLineSegment(sketch, "E2124", {"start": v(-60.95, 23.4) * mm, "end": v(-52.95, 23.4) * mm});
            skLineSegment(sketch, "E2125", {"start": v(-60.95, 31.4) * mm, "end": v(-60.95, 23.4) * mm});
            skLineSegment(sketch, "E2126", {"start": v(-52.95, 31.35) * mm, "end": v(-52.95, 23.4) * mm});
            skLineSegment(sketch, "E2127", {"start": v(-140.5, 15.73) * mm, "end": v(-140.5, -15.75) * mm});
            skLineSegment(sketch, "E2128", {"start": v(134, -4.66) * mm, "end": v(134, 4.68) * mm});
            skSolve(sketch);
        }
        {
            var Q0;
            Q0=qCreatedBy(makeId("Right.planeOp"),FACE);
            var sketch = newSketch(context, id + "F1", { "sketchPlane" : qUnion([Q0])});
            skFitSpline(sketch, "E2129", {"points": [v(-150, 0) * mm, v(-148.73, 5.46) * mm, v(-145.21, 11.33) * mm, v(-139.2, 16.7) * mm, v(-132.05, 21.3) * mm, v(-121.57, 25.1) * mm, v(-108.85, 28.66) * mm, v(-94.18, 31.24) * mm, v(-77.94, 32.54) * mm, v(-65.28, 32.97) * mm, v(-47.16, 32.85) * mm, v(-33.01, 32.05) * mm, v(-17.81, 30.71) * mm, v(-2.83, 29.4) * mm, v(23.14, 26.04) * mm, v(57.4, 20.58) * mm, v(98.4, 12.67) * mm, v(132.03, 5.14) * mm, v(150, 0.7) * mm], "startDerivative": vector(26.25, 166.68) * mm, "endDerivative": vector(271.27, -67.74) * mm});
            skLineSegment(sketch, "E2130", {"start": v(-150, 0) * mm, "end": v(150, 0) * mm, "construction": true});
            skLineSegment(sketch, "E2131", {"start": v(150, 0) * mm, "end": v(150, 0.7) * mm});
            skFitSpline(sketch, "E2132.MirrorCS", {"points": [v(-150, 0) * mm, v(-148.73, -5.46) * mm, v(-145.21, -11.33) * mm, v(-139.2, -16.7) * mm, v(-132.05, -21.3) * mm, v(-121.57, -25.1) * mm, v(-108.85, -28.66) * mm, v(-94.18, -31.24) * mm, v(-77.94, -32.54) * mm, v(-65.28, -32.97) * mm, v(-47.16, -32.85) * mm, v(-33.01, -32.05) * mm, v(-17.81, -30.71) * mm, v(-2.83, -29.4) * mm, v(23.14, -26.04) * mm, v(57.4, -20.58) * mm, v(98.4, -12.67) * mm, v(132.03, -5.14) * mm, v(150, -0.7) * mm], "startDerivative": vector(26.25, -166.68) * mm, "endDerivative": vector(271.27, 67.74) * mm});
            skLineSegment(sketch, "E2133", {"start": v(150, 0) * mm, "end": v(150, -0.7) * mm});
            skSolve(sketch);
        }
        {
            var Q0;
            Q0=qCreatedBy(makeId("Right.planeOp"),FACE);
            cPlane(context, id + "F2", {"entities" : qUnion([Q0]), "cplaneType" : CPlaneType.OFFSET, "offset" : 750 * mm, "width" : 150 * mm, "height" : 150 * mm});
        }
        {
            var Q0;
            Q0=qCreatedBy(id+"F2.planeOp",FACE);
            var sketch = newSketch(context, id + "F3", { "sketchPlane" : qUnion([Q0])});
            skFitSpline(sketch, "E2134", {"points": [v(105.82, 20.28) * mm, v(106.5, 23.2) * mm, v(108.37, 26.32) * mm, v(111.58, 29.2) * mm, v(115.4, 31.64) * mm, v(120.98, 33.67) * mm, v(127.77, 35.57) * mm, v(135.6, 36.94) * mm, v(144.25, 37.64) * mm, v(151, 37.86) * mm, v(160.67, 37.8) * mm, v(168.21, 37.37) * mm, v(176.32, 36.66) * mm, v(184.3, 35.96) * mm, v(198.16, 34.17) * mm, v(216.44, 31.26) * mm, v(238.3, 27.04) * mm, v(256.24, 23.02) * mm, v(265.82, 20.65) * mm], "startDerivative": vector(14, 88.9) * mm, "endDerivative": vector(144.68, -36.13) * mm});
            skLineSegment(sketch, "E2135", {"start": v(105.82, 20.28) * mm, "end": v(265.82, 20.28) * mm, "construction": true});
            skLineSegment(sketch, "E2136", {"start": v(265.82, 20.28) * mm, "end": v(265.82, 20.65) * mm});
            skFitSpline(sketch, "E2137.MirrorCS", {"points": [v(105.82, 20.28) * mm, v(106.5, 17.37) * mm, v(108.37, 14.24) * mm, v(111.58, 11.37) * mm, v(115.4, 8.92) * mm, v(120.98, 6.9) * mm, v(127.77, 5) * mm, v(135.6, 3.62) * mm, v(144.25, 2.92) * mm, v(151, 2.7) * mm, v(160.67, 2.76) * mm, v(168.21, 3.2) * mm, v(176.32, 3.9) * mm, v(184.3, 4.6) * mm, v(198.16, 6.4) * mm, v(216.44, 9.3) * mm, v(238.3, 13.52) * mm, v(256.24, 17.54) * mm, v(265.82, 19.91) * mm], "startDerivative": vector(14, -88.9) * mm, "endDerivative": vector(144.68, 36.13) * mm});
            skLineSegment(sketch, "E2138", {"start": v(265.82, 20.28) * mm, "end": v(265.82, 19.91) * mm});
            skSolve(sketch);
        }
        {
            var Q0;
            Q0=makeQuery(id+"F1.imprint","IMPRINT",FACE,{"disambiguationData":[TD([[makeQuery(id+"F1.imprint","IMPRINT",EDGE,{"derivedFrom":sQuery(id+"F1.wireOp",EDGE,"E2129")}),-1.0]])]});
            var Q1;
            Q1=makeQuery(id+"F3.imprint","IMPRINT",FACE,{"disambiguationData":[TD([[makeQuery(id+"F3.imprint","IMPRINT",EDGE,{"derivedFrom":sQuery(id+"F3.wireOp",EDGE,"E2134")}),-1.0]])]});
            loft(context, id + "F4", {"sheetProfilesArray" : [{ "sheetProfileEntities" : qUnion([Q0]) }, { "sheetProfileEntities" : qUnion([Q1]) }]});
        }
    });
